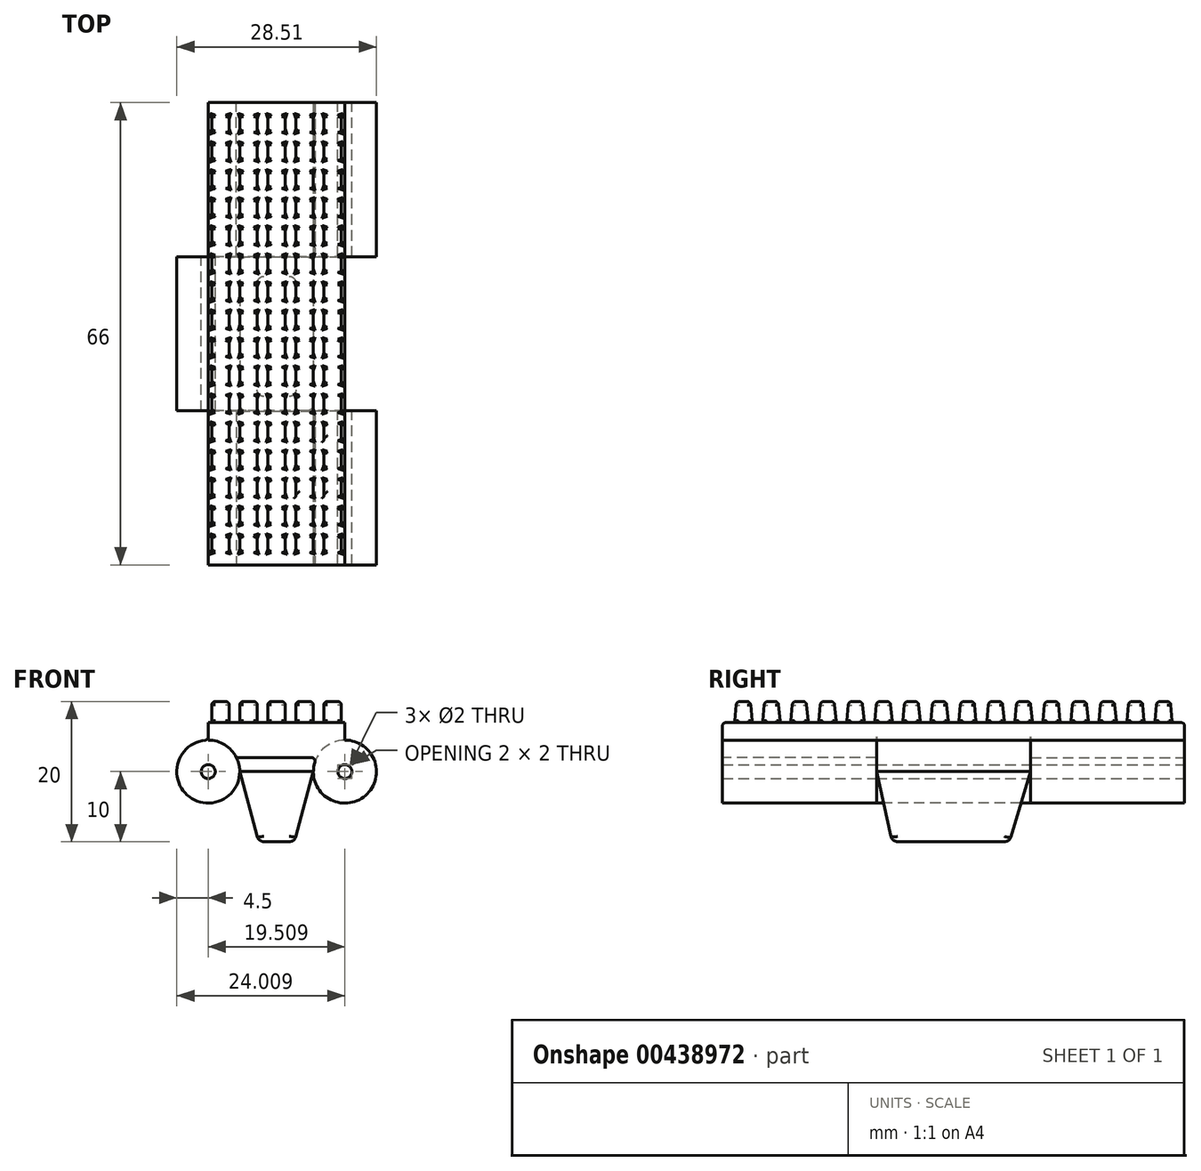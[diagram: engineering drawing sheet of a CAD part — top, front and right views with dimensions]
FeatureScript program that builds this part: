
annotation { "Feature Type Name" : "Feature", "Feature Type Description" : "" }
export const myFeature = defineFeature(function(context is Context, id is Id, definition is map)
    precondition{}
    {
        {
            var Q0;
            Q0=qCreatedBy(makeId("Front.planeOp"),FACE);
            var sketch = newSketch(context, id + "F0", { "sketchPlane" : qUnion([Q0])});
            skCircle(sketch, "E0", {"center": v(0, 0) * mm, "radius": 4.5 * mm});
            skCircle(sketch, "E1", {"center": v(19.5, 0) * mm, "radius": 4.5 * mm});
            skLineSegment(sketch, "E2.bottom", {"start": v(0, 7) * mm, "end": v(19.5, 7) * mm});
            skLineSegment(sketch, "E2.top", {"start": v(4.5, 0) * mm, "end": v(15, 0) * mm});
            skLineSegment(sketch, "E2.left", {"start": v(0, 7) * mm, "end": v(0, 4.5) * mm});
            skLineSegment(sketch, "E2.right", {"start": v(19.5, 7) * mm, "end": v(19.5, 4.5) * mm});
            skSolve(sketch);
        }
        {
            var Q0;
            {var subQ0=sQuery(id+"F0.wireOp",EDGE,"XSPy7m2Q-8Ky5-cPMg-ZX5T-lWh7BPJmsSK1");Q0=makeQuery(id+"F0.imprint","IMPRINT",FACE,{"disambiguationData":[TD([[makeQuery(id+"F0.imprint","IMPRINT",EDGE,{"derivedFrom":subQ0}),-1.0]])]});}
            var Q1;
            {var subQ3=sQuery(id+"F0.wireOp",EDGE,"E2.top");Q1=makeQuery(id+"F0.imprint","IMPRINT",FACE,{"disambiguationData":[TD([[makeQuery(id+"F0.imprint","IMPRINT",EDGE,{"derivedFrom":subQ3}),1.0]])]});}
            var Q2;
            {var subQ0=sQuery(id+"F0.wireOp",EDGE,"E1");var subQ1=makeQuery(id+"F0.imprint","INTERSECT",VERTEX,{"derivedFrom":[subQ0,sQuery(id+"F0.wireOp",EDGE,"E2.top")]});Q2=makeQuery(id+"F0.imprint","IMPRINT",FACE,{"disambiguationData":[TD([[makeQuery(id+"F0.imprint","IMPRINT",EDGE,{"disambiguationData":[TD([[subQ1,1.0]])],"derivedFrom":subQ0}),1.0]])]});}
            var Q3;
            {var subQ0=sQuery(id+"F0.wireOp",EDGE,"E0");var subQ1=makeQuery(id+"F0.imprint","INTERSECT",VERTEX,{"derivedFrom":[subQ0,sQuery(id+"F0.wireOp",EDGE,"E2.top")]});Q3=makeQuery(id+"F0.imprint","IMPRINT",FACE,{"disambiguationData":[TD([[makeQuery(id+"F0.imprint","IMPRINT",EDGE,{"disambiguationData":[TD([[subQ1,-1.0]])],"derivedFrom":subQ0}),1.0]])]});}
            extrude(context, id + "F1", {"entities" : qUnion([Q0, Q1, Q2, Q3]), "oppositeDirection" : true, "depth" : 66 * mm});
        }
        {
            var Q0;
            Q0=makeQuery(id+"F1.opExtrude","SWEPT_FACE",FACE,{"disambiguationData":[OSD([sQuery(id+"F0.wireOp",EDGE,"E2.left")])]});
            var sketch = newSketch(context, id + "F2", { "sketchPlane" : qUnion([Q0])});
            skLineSegment(sketch, "E3", {"start": v(-66, 4.5) * mm, "end": v(-44, 4.5) * mm, "construction": true});
            skLineSegment(sketch, "E4", {"start": v(-22, 4.5) * mm, "end": v(0, 4.5) * mm, "construction": true});
            skSolve(sketch);
        }
        {
            var Q0;
            Q0=makeQuery(id+"F1.opExtrude","CAP_FACE",FACE,{"disambiguationData":[OSD([sQuery(id+"F0.wireOp",EDGE,"E0"),sQuery(id+"F0.wireOp",EDGE,"E1"),sQuery(id+"F0.wireOp",EDGE,"E2.bottom"),sQuery(id+"F0.wireOp",EDGE,"E2.top"),sQuery(id+"F0.wireOp",EDGE,"E2.left"),sQuery(id+"F0.wireOp",EDGE,"E2.right"),sQuery(id+"F0.wireOp",EDGE,"XSPy7m2Q-8Ky5-cPMg-ZX5T-lWh7BPJmsSK1"),sQuery(id+"F0.wireOp",EDGE,"Qv9CYEcz-sdLX-BD8G-fHiO-GuzPuwCw1iiq"),sQuery(id+"F0.wireOp",EDGE,"SLchUEqs-7Prb-pNJw-PFLy-duSCSpJHXW3P")])],"isStart":true});
            var sketch = newSketch(context, id + "F3", { "sketchPlane" : qUnion([Q0])});
            skCircle(sketch, "E5", {"center": v(0, 0) * mm, "radius": 4.5 * mm});
            skSolve(sketch);
        }
        {
            var Q0;
            Q0=makeQuery(id+"F1.opExtrude","CAP_FACE",FACE,{"disambiguationData":[OSD([sQuery(id+"F0.wireOp",EDGE,"E0"),sQuery(id+"F0.wireOp",EDGE,"E1"),sQuery(id+"F0.wireOp",EDGE,"E2.bottom"),sQuery(id+"F0.wireOp",EDGE,"E2.top"),sQuery(id+"F0.wireOp",EDGE,"E2.left"),sQuery(id+"F0.wireOp",EDGE,"E2.right"),sQuery(id+"F0.wireOp",EDGE,"XSPy7m2Q-8Ky5-cPMg-ZX5T-lWh7BPJmsSK1"),sQuery(id+"F0.wireOp",EDGE,"Qv9CYEcz-sdLX-BD8G-fHiO-GuzPuwCw1iiq"),sQuery(id+"F0.wireOp",EDGE,"SLchUEqs-7Prb-pNJw-PFLy-duSCSpJHXW3P")])],"isStart":false});
            var sketch = newSketch(context, id + "F4", { "sketchPlane" : qUnion([Q0])});
            skCircle(sketch, "E6", {"center": v(0, 0) * mm, "radius": 4.5 * mm});
            skSolve(sketch);
        }
        {
            var Q0;
            {var subQ0=sQuery(id+"F4.wireOp",EDGE,"E6");Q0=makeQuery(id+"F4.imprint","IMPRINT",FACE,{"disambiguationData":[TD([[makeQuery(id+"F4.imprint","IMPRINT",EDGE,{"disambiguationData":[OD(0.0)],"derivedFrom":subQ0}),1.0]])]});}
            extrude(context, id + "F5", {"entities" : qUnion([Q0]), "operationType" : NewBodyOperationType.REMOVE, "oppositeDirection" : true, "depth" : 22 * mm});
        }
        {
            var Q0;
            {var subQ0=sQuery(id+"F3.wireOp",EDGE,"E5");var subQ1=makeQuery(id+"F3.imprint","INTERSECT",VERTEX,{"derivedFrom":[makeQuery(id+"F1.opExtrude","CAP_EDGE",EDGE,{"disambiguationData":[OSD([sQuery(id+"F0.wireOp",EDGE,"E2.top")])],"isStart":true}),subQ0]});Q0=makeQuery(id+"F3.imprint","IMPRINT",FACE,{"disambiguationData":[TD([[makeQuery(id+"F3.imprint","IMPRINT",EDGE,{"disambiguationData":[TD([[subQ1,-1.0]])],"derivedFrom":subQ0}),1.0]])]});}
            var Q1;
            Q1=sQuery(id+"F3.wireOp",EDGE,"E5");
            extrude(context, id + "F6", {"entities" : qUnion([Q0]), "operationType" : NewBodyOperationType.REMOVE, "surfaceEntities" : qUnion([Q1]), "oppositeDirection" : true, "depth" : 22 * mm});
        }
        {
            var Q0;
            Q0=makeQuery(id+"F6.boolean.opBoolean","COPY",FACE,{"derivedFrom":makeQuery(id+"F6.opExtrude","CAP_FACE",FACE,{"disambiguationData":[OSD([sQuery(id+"F3.wireOp",EDGE,"E5")])],"isStart":false})});
            var sketch = newSketch(context, id + "F7", { "sketchPlane" : qUnion([Q0])});
            skLineSegment(sketch, "E7", {"start": v(0, 0) * mm, "end": v(26.98, 0) * mm, "construction": true});
            skLineSegment(sketch, "E8", {"start": v(19.5, 7) * mm, "end": v(19.5, -6.27) * mm, "construction": true});
            skPoint(sketch, "E9", {"position": v(19.5, 0) * mm});
            skCircle(sketch, "E10", {"center": v(19.5, 0) * mm, "radius": 4.5 * mm});
            skSolve(sketch);
        }
        {
            var Q0;
            Q0=makeQuery(id+"F7.imprint","IMPRINT",FACE,{"disambiguationData":[TD([[makeQuery(id+"F7.imprint","IMPRINT",EDGE,{"derivedFrom":sQuery(id+"F7.wireOp",EDGE,"E10")}),1.0]])]});
            extrude(context, id + "F8", {"entities" : qUnion([Q0]), "operationType" : NewBodyOperationType.REMOVE, "oppositeDirection" : true, "depth" : 22 * mm});
        }
        {
            var Q0;
            Q0=makeQuery(id+"F1.opExtrude","CAP_FACE",FACE,{"disambiguationData":[OSD([sQuery(id+"F0.wireOp",EDGE,"E0"),sQuery(id+"F0.wireOp",EDGE,"E1"),sQuery(id+"F0.wireOp",EDGE,"E2.bottom"),sQuery(id+"F0.wireOp",EDGE,"E2.top"),sQuery(id+"F0.wireOp",EDGE,"E2.left"),sQuery(id+"F0.wireOp",EDGE,"E2.right"),sQuery(id+"F0.wireOp",EDGE,"XSPy7m2Q-8Ky5-cPMg-ZX5T-lWh7BPJmsSK1"),sQuery(id+"F0.wireOp",EDGE,"Qv9CYEcz-sdLX-BD8G-fHiO-GuzPuwCw1iiq"),sQuery(id+"F0.wireOp",EDGE,"SLchUEqs-7Prb-pNJw-PFLy-duSCSpJHXW3P")])],"isStart":false});
            var sketch = newSketch(context, id + "F9", { "sketchPlane" : qUnion([Q0])});
            skCircle(sketch, "E11", {"center": v(0, 0) * mm, "radius": 1 * mm});
            skLineSegment(sketch, "E12", {"start": v(0, 0) * mm, "end": v(-27.37, 0) * mm, "construction": true});
            skLineSegment(sketch, "E13", {"start": v(-19.5, 7) * mm, "end": v(-19.5, -5.38) * mm, "construction": true});
            skCircle(sketch, "E14", {"center": v(-19.5, 0) * mm, "radius": 1 * mm});
            skSolve(sketch);
        }
        {
            var Q0;
            Q0=makeQuery(id+"F9.imprint","IMPRINT",FACE,{"disambiguationData":[TD([[makeQuery(id+"F9.imprint","IMPRINT",EDGE,{"derivedFrom":sQuery(id+"F9.wireOp",EDGE,"E14")}),1.0]])]});
            var Q1;
            Q1=makeQuery(id+"F9.imprint","IMPRINT",FACE,{"disambiguationData":[TD([[makeQuery(id+"F9.imprint","IMPRINT",EDGE,{"derivedFrom":sQuery(id+"F9.wireOp",EDGE,"E11")}),1.0]])]});
            extrude(context, id + "F10", {"entities" : qUnion([Q0, Q1]), "operationType" : NewBodyOperationType.REMOVE, "oppositeDirection" : true, "depth" : 66 * mm});
        }
        {
            var Q0;
            Q0=makeQuery(id+"F6.boolean.opBoolean","COPY",FACE,{"derivedFrom":makeQuery(id+"F6.opExtrude","CAP_FACE",FACE,{"disambiguationData":[OSD([sQuery(id+"F3.wireOp",EDGE,"E5")])],"isStart":false})});
            var sketch = newSketch(context, id + "F11", { "sketchPlane" : qUnion([Q0])});
            skLineSegment(sketch, "E15", {"start": v(15, 0) * mm, "end": v(30.59, 0) * mm, "construction": true});
            skLineSegment(sketch, "E16", {"start": v(19.5, 6.02) * mm, "end": v(19.5, -8.46) * mm, "construction": true});
            skLineSegment(sketch, "E17", {"start": v(0, 6.05) * mm, "end": v(0, -6.6) * mm, "construction": true});
            skLineSegment(sketch, "E18", {"start": v(15, 0) * mm, "end": v(12.33, -10) * mm});
            skLineSegment(sketch, "E19", {"start": v(15, 0) * mm, "end": v(0, 0) * mm});
            skPoint(sketch, "E20", {"position": v(4.5, 0) * mm});
            skPoint(sketch, "E21", {"position": v(15, 0) * mm});
            skLineSegment(sketch, "E22", {"start": v(4.5, 0) * mm, "end": v(7.18, -10) * mm});
            skLineSegment(sketch, "E23", {"start": v(7.18, -10) * mm, "end": v(12.33, -10) * mm});
            skSolve(sketch);
        }
        {
            var Q0;
            {var subQ0=sQuery(id+"F11.wireOp",EDGE,"E18");Q0=makeQuery(id+"F11.imprint","IMPRINT",FACE,{"disambiguationData":[TD([[makeQuery(id+"F11.imprint","IMPRINT",EDGE,{"derivedFrom":subQ0}),-1.0]])]});}
            extrude(context, id + "F12", {"entities" : qUnion([Q0]), "operationType" : NewBodyOperationType.ADD, "oppositeDirection" : true, "depth" : 22 * mm});
        }
        {
            var Q0;
            {var subQ0=sQuery(id+"F0.wireOp",EDGE,"E2.left");Q0=makeQuery(id+"F2.imprint","IMPRINT",FACE,{"disambiguationData":[TD([[makeQuery(id+"F2.imprint","IMPRINT",EDGE,{"derivedFrom":makeQuery(id+"F1.opExtrude","CAP_EDGE",EDGE,{"disambiguationData":[OSD([subQ0])],"isStart":true})}),-1.0]])]});}
            cPlane(context, id + "F13", {"entities" : qUnion([Q0]), "cplaneType" : CPlaneType.OFFSET, "offset" : 4.5 * mm, "oppositeDirection" : true, "width" : 150 * mm, "height" : 150 * mm});
        }
        {
            var Q0;
            Q0=qCreatedBy(id+"F13.planeOp",FACE);
            var sketch = newSketch(context, id + "F14", { "sketchPlane" : qUnion([Q0])});
            skLineSegment(sketch, "E24", {"start": v(-44, 0) * mm, "end": v(-40.94, -10.27) * mm});
            skLineSegment(sketch, "E25", {"start": v(-22, 0) * mm, "end": v(-24.29, -10.27) * mm});
            skLineSegment(sketch, "E26", {"start": v(-44, 0) * mm, "end": v(-44, -10.27) * mm});
            skLineSegment(sketch, "E27", {"start": v(-22, 0) * mm, "end": v(-22, -10.27) * mm});
            skLineSegment(sketch, "E28", {"start": v(-44, -10.27) * mm, "end": v(-40.94, -10.27) * mm});
            skLineSegment(sketch, "E29.trimOffspring", {"start": v(-24.29, -10.27) * mm, "end": v(-22, -10.27) * mm});
            skSolve(sketch);
        }
        {
            var Q0;
            Q0=makeQuery(id+"F14.imprint","IMPRINT",FACE,{"disambiguationData":[TD([[makeQuery(id+"F14.imprint","IMPRINT",EDGE,{"derivedFrom":sQuery(id+"F14.wireOp",EDGE,"E24")}),-1.0]])]});
            var Q1;
            Q1=makeQuery(id+"F14.imprint","IMPRINT",FACE,{"disambiguationData":[TD([[makeQuery(id+"F14.imprint","IMPRINT",EDGE,{"derivedFrom":sQuery(id+"F14.wireOp",EDGE,"E25")}),1.0]])]});
            extrude(context, id + "F15", {"entities" : qUnion([Q0, Q1]), "operationType" : NewBodyOperationType.REMOVE, "oppositeDirection" : true, "depth" : 13 * mm});
        }
        {
            var Q0;
            Q0=makeQuery(id+"F1.opExtrude","CAP_FACE",FACE,{"disambiguationData":[OSD([sQuery(id+"F0.wireOp",EDGE,"E0"),sQuery(id+"F0.wireOp",EDGE,"E1"),sQuery(id+"F0.wireOp",EDGE,"E2.bottom"),sQuery(id+"F0.wireOp",EDGE,"E2.top"),sQuery(id+"F0.wireOp",EDGE,"E2.left"),sQuery(id+"F0.wireOp",EDGE,"E2.right"),sQuery(id+"F0.wireOp",EDGE,"XSPy7m2Q-8Ky5-cPMg-ZX5T-lWh7BPJmsSK1"),sQuery(id+"F0.wireOp",EDGE,"Qv9CYEcz-sdLX-BD8G-fHiO-GuzPuwCw1iiq"),sQuery(id+"F0.wireOp",EDGE,"SLchUEqs-7Prb-pNJw-PFLy-duSCSpJHXW3P")])],"isStart":false});
            var sketch = newSketch(context, id + "F16", { "sketchPlane" : qUnion([Q0])});
            skArc(sketch, "E30", {"start": v(-15, 0) * mm, "mid": v(-15.13, 1.03) * mm, "end": v(-15.48, 2) * mm});
            skLineSegment(sketch, "E31", {"start": v(-15, 0) * mm, "end": v(-4.5, 0) * mm});
            skLineSegment(sketch, "E32", {"start": v(-4.03, 2) * mm, "end": v(-15.48, 2) * mm});
            skArc(sketch, "E33", {"start": v(-4.03, 2) * mm, "mid": v(-4.38, 1.03) * mm, "end": v(-4.5, 0) * mm});
            skSolve(sketch);
        }
        {
            var Q0;
            Q0=makeQuery(id+"F16.imprint","IMPRINT",FACE,{"disambiguationData":[TD([[makeQuery(id+"F16.imprint","IMPRINT",EDGE,{"derivedFrom":sQuery(id+"F16.wireOp",EDGE,"E30")}),-1.0]])]});
            extrude(context, id + "F17", {"entities" : qUnion([Q0]), "operationType" : NewBodyOperationType.REMOVE, "oppositeDirection" : true, "depth" : 21.99 * mm});
        }
        {
            var Q0;
            Q0=makeQuery(id+"F1.opExtrude","CAP_FACE",FACE,{"disambiguationData":[OSD([sQuery(id+"F0.wireOp",EDGE,"E0"),sQuery(id+"F0.wireOp",EDGE,"E1"),sQuery(id+"F0.wireOp",EDGE,"E2.bottom"),sQuery(id+"F0.wireOp",EDGE,"E2.top"),sQuery(id+"F0.wireOp",EDGE,"E2.left"),sQuery(id+"F0.wireOp",EDGE,"E2.right"),sQuery(id+"F0.wireOp",EDGE,"XSPy7m2Q-8Ky5-cPMg-ZX5T-lWh7BPJmsSK1"),sQuery(id+"F0.wireOp",EDGE,"Qv9CYEcz-sdLX-BD8G-fHiO-GuzPuwCw1iiq"),sQuery(id+"F0.wireOp",EDGE,"SLchUEqs-7Prb-pNJw-PFLy-duSCSpJHXW3P")])],"isStart":true});
            var sketch = newSketch(context, id + "F18", { "sketchPlane" : qUnion([Q0])});
            skArc(sketch, "E34", {"start": v(4.5, 0) * mm, "mid": v(4.38, 1.03) * mm, "end": v(4.03, 2) * mm});
            skArc(sketch, "E35", {"start": v(15.48, 2) * mm, "mid": v(15.13, 1.03) * mm, "end": v(15, 0) * mm});
            skLineSegment(sketch, "E36", {"start": v(4.03, 2) * mm, "end": v(15.48, 2) * mm});
            skLineSegment(sketch, "E37", {"start": v(15, 0) * mm, "end": v(4.5, 0) * mm});
            skSolve(sketch);
        }
        {
            var Q0;
            Q0=makeQuery(id+"F18.imprint","IMPRINT",FACE,{"disambiguationData":[TD([[makeQuery(id+"F18.imprint","IMPRINT",EDGE,{"derivedFrom":sQuery(id+"F18.wireOp",EDGE,"E34")}),-1.0]])]});
            extrude(context, id + "F19", {"entities" : qUnion([Q0]), "operationType" : NewBodyOperationType.REMOVE, "oppositeDirection" : true, "depth" : 21.98 * mm});
        }
        {
            var Q0;
            Q0=makeQuery(id+"FJAbp6d8c6zq0qW_1.boolean.opBoolean","MERGE",FACE,{"derivedFrom":[makeQuery(id+"F1.opExtrude","SWEPT_FACE",FACE,{"disambiguationData":[OSD([sQuery(id+"F0.wireOp",EDGE,"E2.left")])]}),makeQuery(id+"FJAbp6d8c6zq0qW_1.opExtrude","SWEPT_FACE",FACE,{"disambiguationData":[OSD([sQuery(id+"FjXNzUCDF6skfny_1.wireOp",EDGE,"ZpUVPl6h-XxjU-j18W-hNYx-q3vLESmVbvHY")])]})]});
            var sketch = newSketch(context, id + "F20", { "sketchPlane" : qUnion([Q0])});
            skLineSegment(sketch, "E38", {"start": v(-64.23, 7.23) * mm, "end": v(-64.03, 9.54) * mm});
            skLineSegment(sketch, "E39", {"start": v(-61.77, 7.23) * mm, "end": v(-61.97, 9.54) * mm});
            skLineSegment(sketch, "E40", {"start": v(-63.53, 10) * mm, "end": v(-62.47, 10) * mm});
            skPoint(sketch, "E41.visualSharp", {"position": v(-63.99, 10) * mm});
            skArc(sketch, "E41.filletArc", {"start": v(-63.53, 10) * mm, "mid": v(-63.87, 9.87) * mm, "end": v(-64.03, 9.54) * mm});
            skPoint(sketch, "E42.visualSharp", {"position": v(-62.01, 10) * mm});
            skArc(sketch, "E42.filletArc", {"start": v(-61.97, 9.54) * mm, "mid": v(-62.13, 9.87) * mm, "end": v(-62.47, 10) * mm});
            skLineSegment(sketch, "E43", {"start": v(-66, 7) * mm, "end": v(-64.48, 7) * mm});
            skLineSegment(sketch, "E44", {"start": v(-61.52, 7) * mm, "end": v(-60.25, 7) * mm});
            skPoint(sketch, "E45.visualSharp", {"position": v(-64.25, 7) * mm});
            skArc(sketch, "E45.filletArc", {"start": v(-64.48, 7) * mm, "mid": v(-64.31, 7.07) * mm, "end": v(-64.23, 7.23) * mm});
            skPoint(sketch, "E46.visualSharp", {"position": v(-61.75, 7) * mm});
            skArc(sketch, "E46.filletArc", {"start": v(-61.77, 7.23) * mm, "mid": v(-61.69, 7.07) * mm, "end": v(-61.52, 7) * mm});
            skPoint(sketch, "E47.1.0.0", {"position": v(-59.99, 10) * mm});
            skLineSegment(sketch, "E47.1.0.1", {"start": v(-57.52, 7) * mm, "end": v(-56.25, 7) * mm});
            skLineSegment(sketch, "E47.1.0.2", {"start": v(-60.23, 7.23) * mm, "end": v(-60.03, 9.54) * mm});
            skPoint(sketch, "E47.1.0.3", {"position": v(-57.75, 7) * mm});
            skPoint(sketch, "E47.1.0.4", {"position": v(-60.25, 7) * mm});
            skLineSegment(sketch, "E47.1.0.5", {"start": v(-59.53, 10) * mm, "end": v(-58.47, 10) * mm});
            skPoint(sketch, "E47.1.0.6", {"position": v(-58.01, 10) * mm});
            skLineSegment(sketch, "E47.1.0.7", {"start": v(-57.77, 7.23) * mm, "end": v(-57.97, 9.54) * mm});
            skArc(sketch, "E47.1.0.8", {"start": v(-59.53, 10) * mm, "mid": v(-59.87, 9.87) * mm, "end": v(-60.03, 9.54) * mm});
            skArc(sketch, "E47.1.0.9", {"start": v(-57.97, 9.54) * mm, "mid": v(-58.13, 9.87) * mm, "end": v(-58.47, 10) * mm});
            skArc(sketch, "E47.1.0.10", {"start": v(-57.77, 7.23) * mm, "mid": v(-57.69, 7.07) * mm, "end": v(-57.52, 7) * mm});
            skArc(sketch, "E47.1.0.11", {"start": v(-60.48, 7) * mm, "mid": v(-60.31, 7.07) * mm, "end": v(-60.23, 7.23) * mm});
            skPoint(sketch, "E47.2.0.0", {"position": v(-55.99, 10) * mm});
            skLineSegment(sketch, "E47.2.0.1", {"start": v(-53.52, 7) * mm, "end": v(-52.25, 7) * mm});
            skLineSegment(sketch, "E47.2.0.2", {"start": v(-56.23, 7.23) * mm, "end": v(-56.03, 9.54) * mm});
            skPoint(sketch, "E47.2.0.3", {"position": v(-53.75, 7) * mm});
            skPoint(sketch, "E47.2.0.4", {"position": v(-56.25, 7) * mm});
            skLineSegment(sketch, "E47.2.0.5", {"start": v(-55.53, 10) * mm, "end": v(-54.47, 10) * mm});
            skPoint(sketch, "E47.2.0.6", {"position": v(-54.01, 10) * mm});
            skLineSegment(sketch, "E47.2.0.7", {"start": v(-53.77, 7.23) * mm, "end": v(-53.97, 9.54) * mm});
            skArc(sketch, "E47.2.0.8", {"start": v(-55.53, 10) * mm, "mid": v(-55.87, 9.87) * mm, "end": v(-56.03, 9.54) * mm});
            skArc(sketch, "E47.2.0.9", {"start": v(-53.97, 9.54) * mm, "mid": v(-54.13, 9.87) * mm, "end": v(-54.47, 10) * mm});
            skArc(sketch, "E47.2.0.10", {"start": v(-53.77, 7.23) * mm, "mid": v(-53.69, 7.07) * mm, "end": v(-53.52, 7) * mm});
            skArc(sketch, "E47.2.0.11", {"start": v(-56.48, 7) * mm, "mid": v(-56.31, 7.07) * mm, "end": v(-56.23, 7.23) * mm});
            skPoint(sketch, "E47.3.0.0", {"position": v(-51.99, 10) * mm});
            skLineSegment(sketch, "E47.3.0.1", {"start": v(-49.52, 7) * mm, "end": v(-48.25, 7) * mm});
            skLineSegment(sketch, "E47.3.0.2", {"start": v(-52.23, 7.23) * mm, "end": v(-52.03, 9.54) * mm});
            skPoint(sketch, "E47.3.0.3", {"position": v(-49.75, 7) * mm});
            skPoint(sketch, "E47.3.0.4", {"position": v(-52.25, 7) * mm});
            skLineSegment(sketch, "E47.3.0.5", {"start": v(-51.53, 10) * mm, "end": v(-50.47, 10) * mm});
            skPoint(sketch, "E47.3.0.6", {"position": v(-50.01, 10) * mm});
            skLineSegment(sketch, "E47.3.0.7", {"start": v(-49.77, 7.23) * mm, "end": v(-49.97, 9.54) * mm});
            skArc(sketch, "E47.3.0.8", {"start": v(-51.53, 10) * mm, "mid": v(-51.87, 9.87) * mm, "end": v(-52.03, 9.54) * mm});
            skArc(sketch, "E47.3.0.9", {"start": v(-49.97, 9.54) * mm, "mid": v(-50.13, 9.87) * mm, "end": v(-50.47, 10) * mm});
            skArc(sketch, "E47.3.0.10", {"start": v(-49.77, 7.23) * mm, "mid": v(-49.69, 7.07) * mm, "end": v(-49.52, 7) * mm});
            skArc(sketch, "E47.3.0.11", {"start": v(-52.48, 7) * mm, "mid": v(-52.31, 7.07) * mm, "end": v(-52.23, 7.23) * mm});
            skPoint(sketch, "E47.4.0.0", {"position": v(-47.99, 10) * mm});
            skLineSegment(sketch, "E47.4.0.1", {"start": v(-45.52, 7) * mm, "end": v(-44.25, 7) * mm});
            skLineSegment(sketch, "E47.4.0.2", {"start": v(-48.23, 7.23) * mm, "end": v(-48.03, 9.54) * mm});
            skPoint(sketch, "E47.4.0.3", {"position": v(-45.75, 7) * mm});
            skPoint(sketch, "E47.4.0.4", {"position": v(-48.25, 7) * mm});
            skLineSegment(sketch, "E47.4.0.5", {"start": v(-47.53, 10) * mm, "end": v(-46.47, 10) * mm});
            skPoint(sketch, "E47.4.0.6", {"position": v(-46.01, 10) * mm});
            skLineSegment(sketch, "E47.4.0.7", {"start": v(-45.77, 7.23) * mm, "end": v(-45.97, 9.54) * mm});
            skArc(sketch, "E47.4.0.8", {"start": v(-47.53, 10) * mm, "mid": v(-47.87, 9.87) * mm, "end": v(-48.03, 9.54) * mm});
            skArc(sketch, "E47.4.0.9", {"start": v(-45.97, 9.54) * mm, "mid": v(-46.13, 9.87) * mm, "end": v(-46.47, 10) * mm});
            skArc(sketch, "E47.4.0.10", {"start": v(-45.77, 7.23) * mm, "mid": v(-45.69, 7.07) * mm, "end": v(-45.52, 7) * mm});
            skArc(sketch, "E47.4.0.11", {"start": v(-48.48, 7) * mm, "mid": v(-48.31, 7.07) * mm, "end": v(-48.23, 7.23) * mm});
            skPoint(sketch, "E47.5.0.0", {"position": v(-43.99, 10) * mm});
            skLineSegment(sketch, "E47.5.0.1", {"start": v(-41.52, 7) * mm, "end": v(-40.25, 7) * mm});
            skLineSegment(sketch, "E47.5.0.2", {"start": v(-44.23, 7.23) * mm, "end": v(-44.03, 9.54) * mm});
            skPoint(sketch, "E47.5.0.3", {"position": v(-41.75, 7) * mm});
            skPoint(sketch, "E47.5.0.4", {"position": v(-44.25, 7) * mm});
            skLineSegment(sketch, "E47.5.0.5", {"start": v(-43.53, 10) * mm, "end": v(-42.47, 10) * mm});
            skPoint(sketch, "E47.5.0.6", {"position": v(-42.01, 10) * mm});
            skLineSegment(sketch, "E47.5.0.7", {"start": v(-41.77, 7.23) * mm, "end": v(-41.97, 9.54) * mm});
            skArc(sketch, "E47.5.0.8", {"start": v(-43.53, 10) * mm, "mid": v(-43.87, 9.87) * mm, "end": v(-44.03, 9.54) * mm});
            skArc(sketch, "E47.5.0.9", {"start": v(-41.97, 9.54) * mm, "mid": v(-42.13, 9.87) * mm, "end": v(-42.47, 10) * mm});
            skArc(sketch, "E47.5.0.10", {"start": v(-41.77, 7.23) * mm, "mid": v(-41.69, 7.07) * mm, "end": v(-41.52, 7) * mm});
            skArc(sketch, "E47.5.0.11", {"start": v(-44.48, 7) * mm, "mid": v(-44.31, 7.07) * mm, "end": v(-44.23, 7.23) * mm});
            skPoint(sketch, "E47.6.0.0", {"position": v(-39.99, 10) * mm});
            skLineSegment(sketch, "E47.6.0.1", {"start": v(-37.52, 7) * mm, "end": v(-36.25, 7) * mm});
            skLineSegment(sketch, "E47.6.0.2", {"start": v(-40.23, 7.23) * mm, "end": v(-40.03, 9.54) * mm});
            skPoint(sketch, "E47.6.0.3", {"position": v(-37.75, 7) * mm});
            skPoint(sketch, "E47.6.0.4", {"position": v(-40.25, 7) * mm});
            skLineSegment(sketch, "E47.6.0.5", {"start": v(-39.53, 10) * mm, "end": v(-38.47, 10) * mm});
            skPoint(sketch, "E47.6.0.6", {"position": v(-38.01, 10) * mm});
            skLineSegment(sketch, "E47.6.0.7", {"start": v(-37.77, 7.23) * mm, "end": v(-37.97, 9.54) * mm});
            skArc(sketch, "E47.6.0.8", {"start": v(-39.53, 10) * mm, "mid": v(-39.87, 9.87) * mm, "end": v(-40.03, 9.54) * mm});
            skArc(sketch, "E47.6.0.9", {"start": v(-37.97, 9.54) * mm, "mid": v(-38.13, 9.87) * mm, "end": v(-38.47, 10) * mm});
            skArc(sketch, "E47.6.0.10", {"start": v(-37.77, 7.23) * mm, "mid": v(-37.69, 7.07) * mm, "end": v(-37.52, 7) * mm});
            skArc(sketch, "E47.6.0.11", {"start": v(-40.48, 7) * mm, "mid": v(-40.31, 7.07) * mm, "end": v(-40.23, 7.23) * mm});
            skPoint(sketch, "E47.7.0.0", {"position": v(-35.99, 10) * mm});
            skLineSegment(sketch, "E47.7.0.1", {"start": v(-33.52, 7) * mm, "end": v(-32.25, 7) * mm});
            skLineSegment(sketch, "E47.7.0.2", {"start": v(-36.23, 7.23) * mm, "end": v(-36.03, 9.54) * mm});
            skPoint(sketch, "E47.7.0.3", {"position": v(-33.75, 7) * mm});
            skPoint(sketch, "E47.7.0.4", {"position": v(-36.25, 7) * mm});
            skLineSegment(sketch, "E47.7.0.5", {"start": v(-35.53, 10) * mm, "end": v(-34.47, 10) * mm});
            skPoint(sketch, "E47.7.0.6", {"position": v(-34.01, 10) * mm});
            skLineSegment(sketch, "E47.7.0.7", {"start": v(-33.77, 7.23) * mm, "end": v(-33.97, 9.54) * mm});
            skArc(sketch, "E47.7.0.8", {"start": v(-35.53, 10) * mm, "mid": v(-35.87, 9.87) * mm, "end": v(-36.03, 9.54) * mm});
            skArc(sketch, "E47.7.0.9", {"start": v(-33.97, 9.54) * mm, "mid": v(-34.13, 9.87) * mm, "end": v(-34.47, 10) * mm});
            skArc(sketch, "E47.7.0.10", {"start": v(-33.77, 7.23) * mm, "mid": v(-33.69, 7.07) * mm, "end": v(-33.52, 7) * mm});
            skArc(sketch, "E47.7.0.11", {"start": v(-36.48, 7) * mm, "mid": v(-36.31, 7.07) * mm, "end": v(-36.23, 7.23) * mm});
            skPoint(sketch, "E47.8.0.0", {"position": v(-31.99, 10) * mm});
            skLineSegment(sketch, "E47.8.0.1", {"start": v(-29.52, 7) * mm, "end": v(-28.25, 7) * mm});
            skLineSegment(sketch, "E47.8.0.2", {"start": v(-32.23, 7.23) * mm, "end": v(-32.03, 9.54) * mm});
            skPoint(sketch, "E47.8.0.3", {"position": v(-29.75, 7) * mm});
            skPoint(sketch, "E47.8.0.4", {"position": v(-32.25, 7) * mm});
            skLineSegment(sketch, "E47.8.0.5", {"start": v(-31.53, 10) * mm, "end": v(-30.47, 10) * mm});
            skPoint(sketch, "E47.8.0.6", {"position": v(-30.01, 10) * mm});
            skLineSegment(sketch, "E47.8.0.7", {"start": v(-29.77, 7.23) * mm, "end": v(-29.97, 9.54) * mm});
            skArc(sketch, "E47.8.0.8", {"start": v(-31.53, 10) * mm, "mid": v(-31.87, 9.87) * mm, "end": v(-32.03, 9.54) * mm});
            skArc(sketch, "E47.8.0.9", {"start": v(-29.97, 9.54) * mm, "mid": v(-30.13, 9.87) * mm, "end": v(-30.47, 10) * mm});
            skArc(sketch, "E47.8.0.10", {"start": v(-29.77, 7.23) * mm, "mid": v(-29.69, 7.07) * mm, "end": v(-29.52, 7) * mm});
            skArc(sketch, "E47.8.0.11", {"start": v(-32.48, 7) * mm, "mid": v(-32.31, 7.07) * mm, "end": v(-32.23, 7.23) * mm});
            skPoint(sketch, "E47.9.0.0", {"position": v(-27.99, 10) * mm});
            skLineSegment(sketch, "E47.9.0.1", {"start": v(-25.52, 7) * mm, "end": v(-24.25, 7) * mm});
            skLineSegment(sketch, "E47.9.0.2", {"start": v(-28.23, 7.23) * mm, "end": v(-28.03, 9.54) * mm});
            skPoint(sketch, "E47.9.0.3", {"position": v(-25.75, 7) * mm});
            skPoint(sketch, "E47.9.0.4", {"position": v(-28.25, 7) * mm});
            skLineSegment(sketch, "E47.9.0.5", {"start": v(-27.53, 10) * mm, "end": v(-26.47, 10) * mm});
            skPoint(sketch, "E47.9.0.6", {"position": v(-26.01, 10) * mm});
            skLineSegment(sketch, "E47.9.0.7", {"start": v(-25.77, 7.23) * mm, "end": v(-25.97, 9.54) * mm});
            skArc(sketch, "E47.9.0.8", {"start": v(-27.53, 10) * mm, "mid": v(-27.87, 9.87) * mm, "end": v(-28.03, 9.54) * mm});
            skArc(sketch, "E47.9.0.9", {"start": v(-25.97, 9.54) * mm, "mid": v(-26.13, 9.87) * mm, "end": v(-26.47, 10) * mm});
            skArc(sketch, "E47.9.0.10", {"start": v(-25.77, 7.23) * mm, "mid": v(-25.69, 7.07) * mm, "end": v(-25.52, 7) * mm});
            skArc(sketch, "E47.9.0.11", {"start": v(-28.48, 7) * mm, "mid": v(-28.31, 7.07) * mm, "end": v(-28.23, 7.23) * mm});
            skPoint(sketch, "E47.10.0.0", {"position": v(-23.99, 10) * mm});
            skLineSegment(sketch, "E47.10.0.1", {"start": v(-21.52, 7) * mm, "end": v(-20.25, 7) * mm});
            skLineSegment(sketch, "E47.10.0.2", {"start": v(-24.23, 7.23) * mm, "end": v(-24.03, 9.54) * mm});
            skPoint(sketch, "E47.10.0.3", {"position": v(-21.75, 7) * mm});
            skPoint(sketch, "E47.10.0.4", {"position": v(-24.25, 7) * mm});
            skLineSegment(sketch, "E47.10.0.5", {"start": v(-23.53, 10) * mm, "end": v(-22.47, 10) * mm});
            skPoint(sketch, "E47.10.0.6", {"position": v(-22.01, 10) * mm});
            skLineSegment(sketch, "E47.10.0.7", {"start": v(-21.77, 7.23) * mm, "end": v(-21.97, 9.54) * mm});
            skArc(sketch, "E47.10.0.8", {"start": v(-23.53, 10) * mm, "mid": v(-23.87, 9.87) * mm, "end": v(-24.03, 9.54) * mm});
            skArc(sketch, "E47.10.0.9", {"start": v(-21.97, 9.54) * mm, "mid": v(-22.13, 9.87) * mm, "end": v(-22.47, 10) * mm});
            skArc(sketch, "E47.10.0.10", {"start": v(-21.77, 7.23) * mm, "mid": v(-21.69, 7.07) * mm, "end": v(-21.52, 7) * mm});
            skArc(sketch, "E47.10.0.11", {"start": v(-24.48, 7) * mm, "mid": v(-24.31, 7.07) * mm, "end": v(-24.23, 7.23) * mm});
            skPoint(sketch, "E47.11.0.0", {"position": v(-19.99, 10) * mm});
            skLineSegment(sketch, "E47.11.0.1", {"start": v(-17.52, 7) * mm, "end": v(-16.25, 7) * mm});
            skLineSegment(sketch, "E47.11.0.2", {"start": v(-20.23, 7.23) * mm, "end": v(-20.03, 9.54) * mm});
            skPoint(sketch, "E47.11.0.3", {"position": v(-17.75, 7) * mm});
            skPoint(sketch, "E47.11.0.4", {"position": v(-20.25, 7) * mm});
            skLineSegment(sketch, "E47.11.0.5", {"start": v(-19.53, 10) * mm, "end": v(-18.47, 10) * mm});
            skPoint(sketch, "E47.11.0.6", {"position": v(-18.01, 10) * mm});
            skLineSegment(sketch, "E47.11.0.7", {"start": v(-17.77, 7.23) * mm, "end": v(-17.97, 9.54) * mm});
            skArc(sketch, "E47.11.0.8", {"start": v(-19.53, 10) * mm, "mid": v(-19.87, 9.87) * mm, "end": v(-20.03, 9.54) * mm});
            skArc(sketch, "E47.11.0.9", {"start": v(-17.97, 9.54) * mm, "mid": v(-18.13, 9.87) * mm, "end": v(-18.47, 10) * mm});
            skArc(sketch, "E47.11.0.10", {"start": v(-17.77, 7.23) * mm, "mid": v(-17.69, 7.07) * mm, "end": v(-17.52, 7) * mm});
            skArc(sketch, "E47.11.0.11", {"start": v(-20.48, 7) * mm, "mid": v(-20.31, 7.07) * mm, "end": v(-20.23, 7.23) * mm});
            skPoint(sketch, "E47.12.0.0", {"position": v(-15.99, 10) * mm});
            skLineSegment(sketch, "E47.12.0.1", {"start": v(-13.52, 7) * mm, "end": v(-12.25, 7) * mm});
            skLineSegment(sketch, "E47.12.0.2", {"start": v(-16.23, 7.23) * mm, "end": v(-16.03, 9.54) * mm});
            skPoint(sketch, "E47.12.0.3", {"position": v(-13.75, 7) * mm});
            skPoint(sketch, "E47.12.0.4", {"position": v(-16.25, 7) * mm});
            skLineSegment(sketch, "E47.12.0.5", {"start": v(-15.53, 10) * mm, "end": v(-14.47, 10) * mm});
            skPoint(sketch, "E47.12.0.6", {"position": v(-14.01, 10) * mm});
            skLineSegment(sketch, "E47.12.0.7", {"start": v(-13.77, 7.23) * mm, "end": v(-13.97, 9.54) * mm});
            skArc(sketch, "E47.12.0.8", {"start": v(-15.53, 10) * mm, "mid": v(-15.87, 9.87) * mm, "end": v(-16.03, 9.54) * mm});
            skArc(sketch, "E47.12.0.9", {"start": v(-13.97, 9.54) * mm, "mid": v(-14.13, 9.87) * mm, "end": v(-14.47, 10) * mm});
            skArc(sketch, "E47.12.0.10", {"start": v(-13.77, 7.23) * mm, "mid": v(-13.69, 7.07) * mm, "end": v(-13.52, 7) * mm});
            skArc(sketch, "E47.12.0.11", {"start": v(-16.48, 7) * mm, "mid": v(-16.31, 7.07) * mm, "end": v(-16.23, 7.23) * mm});
            skPoint(sketch, "E47.13.0.0", {"position": v(-11.99, 10) * mm});
            skLineSegment(sketch, "E47.13.0.1", {"start": v(-9.52, 7) * mm, "end": v(-8.25, 7) * mm});
            skLineSegment(sketch, "E47.13.0.2", {"start": v(-12.23, 7.23) * mm, "end": v(-12.03, 9.54) * mm});
            skPoint(sketch, "E47.13.0.3", {"position": v(-9.75, 7) * mm});
            skPoint(sketch, "E47.13.0.4", {"position": v(-12.25, 7) * mm});
            skLineSegment(sketch, "E47.13.0.5", {"start": v(-11.53, 10) * mm, "end": v(-10.47, 10) * mm});
            skPoint(sketch, "E47.13.0.6", {"position": v(-10.01, 10) * mm});
            skLineSegment(sketch, "E47.13.0.7", {"start": v(-9.77, 7.23) * mm, "end": v(-9.97, 9.54) * mm});
            skArc(sketch, "E47.13.0.8", {"start": v(-11.53, 10) * mm, "mid": v(-11.87, 9.87) * mm, "end": v(-12.03, 9.54) * mm});
            skArc(sketch, "E47.13.0.9", {"start": v(-9.97, 9.54) * mm, "mid": v(-10.13, 9.87) * mm, "end": v(-10.47, 10) * mm});
            skArc(sketch, "E47.13.0.10", {"start": v(-9.77, 7.23) * mm, "mid": v(-9.69, 7.07) * mm, "end": v(-9.52, 7) * mm});
            skArc(sketch, "E47.13.0.11", {"start": v(-12.48, 7) * mm, "mid": v(-12.31, 7.07) * mm, "end": v(-12.23, 7.23) * mm});
            skPoint(sketch, "E47.14.0.0", {"position": v(-7.99, 10) * mm});
            skLineSegment(sketch, "E47.14.0.1", {"start": v(-5.52, 7) * mm, "end": v(-4.25, 7) * mm});
            skLineSegment(sketch, "E47.14.0.2", {"start": v(-8.23, 7.23) * mm, "end": v(-8.03, 9.54) * mm});
            skPoint(sketch, "E47.14.0.3", {"position": v(-5.75, 7) * mm});
            skPoint(sketch, "E47.14.0.4", {"position": v(-8.25, 7) * mm});
            skLineSegment(sketch, "E47.14.0.5", {"start": v(-7.53, 10) * mm, "end": v(-6.47, 10) * mm});
            skPoint(sketch, "E47.14.0.6", {"position": v(-6.01, 10) * mm});
            skLineSegment(sketch, "E47.14.0.7", {"start": v(-5.77, 7.23) * mm, "end": v(-5.97, 9.54) * mm});
            skArc(sketch, "E47.14.0.8", {"start": v(-7.53, 10) * mm, "mid": v(-7.87, 9.87) * mm, "end": v(-8.03, 9.54) * mm});
            skArc(sketch, "E47.14.0.9", {"start": v(-5.97, 9.54) * mm, "mid": v(-6.13, 9.87) * mm, "end": v(-6.47, 10) * mm});
            skArc(sketch, "E47.14.0.10", {"start": v(-5.77, 7.23) * mm, "mid": v(-5.69, 7.07) * mm, "end": v(-5.52, 7) * mm});
            skArc(sketch, "E47.14.0.11", {"start": v(-8.48, 7) * mm, "mid": v(-8.31, 7.07) * mm, "end": v(-8.23, 7.23) * mm});
            skPoint(sketch, "E47.15.0.0", {"position": v(-3.99, 10) * mm});
            skLineSegment(sketch, "E47.15.0.2", {"start": v(-4.23, 7.23) * mm, "end": v(-4.03, 9.54) * mm});
            skPoint(sketch, "E47.15.0.3", {"position": v(-1.75, 7) * mm});
            skPoint(sketch, "E47.15.0.4", {"position": v(-4.25, 7) * mm});
            skLineSegment(sketch, "E47.15.0.5", {"start": v(-3.53, 10) * mm, "end": v(-2.47, 10) * mm});
            skPoint(sketch, "E47.15.0.6", {"position": v(-2.01, 10) * mm});
            skLineSegment(sketch, "E47.15.0.7", {"start": v(-1.77, 7.23) * mm, "end": v(-1.97, 9.54) * mm});
            skArc(sketch, "E47.15.0.8", {"start": v(-3.53, 10) * mm, "mid": v(-3.87, 9.87) * mm, "end": v(-4.03, 9.54) * mm});
            skArc(sketch, "E47.15.0.9", {"start": v(-1.97, 9.54) * mm, "mid": v(-2.13, 9.87) * mm, "end": v(-2.47, 10) * mm});
            skArc(sketch, "E47.15.0.10", {"start": v(-1.77, 7.23) * mm, "mid": v(-1.69, 7.07) * mm, "end": v(-1.52, 7) * mm});
            skArc(sketch, "E47.15.0.11", {"start": v(-4.48, 7) * mm, "mid": v(-4.31, 7.07) * mm, "end": v(-4.23, 7.23) * mm});
            skLineSegment(sketch, "E47.direction1", {"start": v(-64.48, 7) * mm, "end": v(-60.48, 7) * mm, "construction": true});
            skSolve(sketch);
        }
        {
            var Q0;
            Q0=makeQuery(id+"F20.imprint","IMPRINT",FACE,{"disambiguationData":[TD([[makeQuery(id+"F20.imprint","IMPRINT",EDGE,{"derivedFrom":sQuery(id+"F20.wireOp",EDGE,"E38")}),-1.0]])]});
            var Q1;
            Q1=makeQuery(id+"F20.imprint","IMPRINT",FACE,{"disambiguationData":[TD([[makeQuery(id+"F20.imprint","IMPRINT",EDGE,{"derivedFrom":sQuery(id+"F20.wireOp",EDGE,"E47.1.0.2")}),-1.0]])]});
            var Q2;
            Q2=makeQuery(id+"F20.imprint","IMPRINT",FACE,{"disambiguationData":[TD([[makeQuery(id+"F20.imprint","IMPRINT",EDGE,{"derivedFrom":sQuery(id+"F20.wireOp",EDGE,"E47.2.0.2")}),-1.0]])]});
            var Q3;
            Q3=makeQuery(id+"F20.imprint","IMPRINT",FACE,{"disambiguationData":[TD([[makeQuery(id+"F20.imprint","IMPRINT",EDGE,{"derivedFrom":sQuery(id+"F20.wireOp",EDGE,"E47.3.0.2")}),-1.0]])]});
            var Q4;
            Q4=makeQuery(id+"F20.imprint","IMPRINT",FACE,{"disambiguationData":[TD([[makeQuery(id+"F20.imprint","IMPRINT",EDGE,{"derivedFrom":sQuery(id+"F20.wireOp",EDGE,"E47.4.0.2")}),-1.0]])]});
            var Q5;
            Q5=makeQuery(id+"F20.imprint","IMPRINT",FACE,{"disambiguationData":[TD([[makeQuery(id+"F20.imprint","IMPRINT",EDGE,{"derivedFrom":sQuery(id+"F20.wireOp",EDGE,"E47.5.0.2")}),-1.0]])]});
            var Q6;
            Q6=makeQuery(id+"F20.imprint","IMPRINT",FACE,{"disambiguationData":[TD([[makeQuery(id+"F20.imprint","IMPRINT",EDGE,{"derivedFrom":sQuery(id+"F20.wireOp",EDGE,"E47.6.0.2")}),-1.0]])]});
            var Q7;
            Q7=makeQuery(id+"F20.imprint","IMPRINT",FACE,{"disambiguationData":[TD([[makeQuery(id+"F20.imprint","IMPRINT",EDGE,{"derivedFrom":sQuery(id+"F20.wireOp",EDGE,"E47.7.0.2")}),-1.0]])]});
            var Q8;
            Q8=makeQuery(id+"F20.imprint","IMPRINT",FACE,{"disambiguationData":[TD([[makeQuery(id+"F20.imprint","IMPRINT",EDGE,{"derivedFrom":sQuery(id+"F20.wireOp",EDGE,"E47.8.0.2")}),-1.0]])]});
            var Q9;
            Q9=makeQuery(id+"F20.imprint","IMPRINT",FACE,{"disambiguationData":[TD([[makeQuery(id+"F20.imprint","IMPRINT",EDGE,{"derivedFrom":sQuery(id+"F20.wireOp",EDGE,"E47.9.0.2")}),-1.0]])]});
            var Q10;
            Q10=makeQuery(id+"F20.imprint","IMPRINT",FACE,{"disambiguationData":[TD([[makeQuery(id+"F20.imprint","IMPRINT",EDGE,{"derivedFrom":sQuery(id+"F20.wireOp",EDGE,"E47.10.0.2")}),-1.0]])]});
            var Q11;
            Q11=makeQuery(id+"F20.imprint","IMPRINT",FACE,{"disambiguationData":[TD([[makeQuery(id+"F20.imprint","IMPRINT",EDGE,{"derivedFrom":sQuery(id+"F20.wireOp",EDGE,"E47.11.0.2")}),-1.0]])]});
            var Q12;
            Q12=makeQuery(id+"F20.imprint","IMPRINT",FACE,{"disambiguationData":[TD([[makeQuery(id+"F20.imprint","IMPRINT",EDGE,{"derivedFrom":sQuery(id+"F20.wireOp",EDGE,"E47.12.0.2")}),-1.0]])]});
            var Q13;
            Q13=makeQuery(id+"F20.imprint","IMPRINT",FACE,{"disambiguationData":[TD([[makeQuery(id+"F20.imprint","IMPRINT",EDGE,{"derivedFrom":sQuery(id+"F20.wireOp",EDGE,"E47.13.0.2")}),-1.0]])]});
            var Q14;
            Q14=makeQuery(id+"F20.imprint","IMPRINT",FACE,{"disambiguationData":[TD([[makeQuery(id+"F20.imprint","IMPRINT",EDGE,{"derivedFrom":sQuery(id+"F20.wireOp",EDGE,"E47.14.0.2")}),-1.0]])]});
            var Q15;
            Q15=makeQuery(id+"F20.imprint","IMPRINT",FACE,{"disambiguationData":[TD([[makeQuery(id+"F20.imprint","IMPRINT",EDGE,{"derivedFrom":sQuery(id+"F20.wireOp",EDGE,"E47.15.0.2")}),-1.0]])]});
            extrude(context, id + "F21", {"entities" : qUnion([Q0, Q1, Q2, Q3, Q4, Q5, Q6, Q7, Q8, Q9, Q10, Q11, Q12, Q13, Q14, Q15]), "operationType" : NewBodyOperationType.ADD, "oppositeDirection" : true, "depth" : 19.5 * mm});
        }
        {
            var Q0;
            Q0=makeQuery(id+"F1.opExtrude","CAP_FACE",FACE,{"disambiguationData":[OSD([sQuery(id+"F0.wireOp",EDGE,"E0"),sQuery(id+"F0.wireOp",EDGE,"E1"),sQuery(id+"F0.wireOp",EDGE,"E2.bottom"),sQuery(id+"F0.wireOp",EDGE,"E2.top"),sQuery(id+"F0.wireOp",EDGE,"E2.left"),sQuery(id+"F0.wireOp",EDGE,"E2.right")])],"isStart":true});
            var sketch = newSketch(context, id + "F22", { "sketchPlane" : qUnion([Q0])});
            skLineSegment(sketch, "E48", {"start": v(0.5, 7.25) * mm, "end": v(0.5, 9.5) * mm});
            skLineSegment(sketch, "E49", {"start": v(3, 7.25) * mm, "end": v(3, 9.5) * mm});
            skPoint(sketch, "E50.visualSharp", {"position": v(0.5, 10) * mm});
            skArc(sketch, "E50.filletArc", {"start": v(1, 10) * mm, "mid": v(0.65, 9.85) * mm, "end": v(0.5, 9.5) * mm});
            skPoint(sketch, "E51.visualSharp", {"position": v(3, 10) * mm});
            skArc(sketch, "E51.filletArc", {"start": v(3, 9.5) * mm, "mid": v(2.86, 9.85) * mm, "end": v(2.5, 10) * mm});
            skPoint(sketch, "E52.visualSharp", {"position": v(0.5, 7) * mm});
            skArc(sketch, "E52.filletArc", {"start": v(0.25, 7) * mm, "mid": v(0.43, 7.07) * mm, "end": v(0.5, 7.25) * mm});
            skPoint(sketch, "E53.visualSharp", {"position": v(3, 7) * mm});
            skArc(sketch, "E53.filletArc", {"start": v(3, 7.25) * mm, "mid": v(3.08, 7.07) * mm, "end": v(3.25, 7) * mm});
            skLineSegment(sketch, "E54", {"start": v(1, 10) * mm, "end": v(0, 10) * mm});
            skLineSegment(sketch, "E55", {"start": v(0, 10) * mm, "end": v(0, 7) * mm});
            skLineSegment(sketch, "E56", {"start": v(4.5, 7.25) * mm, "end": v(4.5, 9.5) * mm});
            skLineSegment(sketch, "E57", {"start": v(7, 7.25) * mm, "end": v(7, 9.5) * mm});
            skArc(sketch, "E58.filletArc", {"start": v(5, 10) * mm, "mid": v(4.65, 9.85) * mm, "end": v(4.5, 9.5) * mm});
            skArc(sketch, "E59.filletArc", {"start": v(7, 9.5) * mm, "mid": v(6.86, 9.85) * mm, "end": v(6.5, 10) * mm});
            skArc(sketch, "E60.filletArc", {"start": v(7, 7.25) * mm, "mid": v(7.08, 7.07) * mm, "end": v(7.25, 7) * mm});
            skLineSegment(sketch, "E61", {"start": v(8.5, 7.25) * mm, "end": v(8.5, 9.5) * mm});
            skLineSegment(sketch, "E62", {"start": v(11, 7.25) * mm, "end": v(11, 9.5) * mm});
            skArc(sketch, "E63.filletArc", {"start": v(9, 10) * mm, "mid": v(8.65, 9.85) * mm, "end": v(8.5, 9.5) * mm});
            skArc(sketch, "E64.filletArc", {"start": v(11, 9.5) * mm, "mid": v(10.86, 9.85) * mm, "end": v(10.5, 10) * mm});
            skArc(sketch, "E65.filletArc", {"start": v(8.25, 7) * mm, "mid": v(8.43, 7.07) * mm, "end": v(8.5, 7.25) * mm});
            skArc(sketch, "E66.filletArc", {"start": v(11, 7.25) * mm, "mid": v(11.08, 7.07) * mm, "end": v(11.25, 7) * mm});
            skLineSegment(sketch, "E67", {"start": v(12.5, 7.25) * mm, "end": v(12.5, 9.5) * mm});
            skLineSegment(sketch, "E68", {"start": v(15, 7.25) * mm, "end": v(15, 9.5) * mm});
            skArc(sketch, "E69.filletArc", {"start": v(13, 10) * mm, "mid": v(12.65, 9.85) * mm, "end": v(12.5, 9.5) * mm});
            skArc(sketch, "E70.filletArc", {"start": v(15, 9.5) * mm, "mid": v(14.86, 9.85) * mm, "end": v(14.5, 10) * mm});
            skArc(sketch, "E71.filletArc", {"start": v(12.25, 7) * mm, "mid": v(12.43, 7.07) * mm, "end": v(12.5, 7.25) * mm});
            skArc(sketch, "E72.filletArc", {"start": v(15, 7.25) * mm, "mid": v(15.08, 7.07) * mm, "end": v(15.25, 7) * mm});
            skLineSegment(sketch, "E73", {"start": v(16.5, 7.25) * mm, "end": v(16.5, 9.5) * mm});
            skLineSegment(sketch, "E74", {"start": v(19, 7.25) * mm, "end": v(19, 9.5) * mm});
            skArc(sketch, "E75.filletArc", {"start": v(17, 10) * mm, "mid": v(16.65, 9.85) * mm, "end": v(16.5, 9.5) * mm});
            skArc(sketch, "E76.filletArc", {"start": v(19, 9.5) * mm, "mid": v(18.86, 9.85) * mm, "end": v(18.5, 10) * mm});
            skArc(sketch, "E77.filletArc", {"start": v(16.25, 7) * mm, "mid": v(16.43, 7.07) * mm, "end": v(16.5, 7.25) * mm});
            skArc(sketch, "E78.filletArc", {"start": v(19, 7.25) * mm, "mid": v(19.08, 7.07) * mm, "end": v(19.25, 7) * mm});
            skLineSegment(sketch, "E79", {"start": v(2.5, 10) * mm, "end": v(5, 10) * mm});
            skLineSegment(sketch, "E80", {"start": v(6.5, 10) * mm, "end": v(9, 10) * mm});
            skLineSegment(sketch, "E81", {"start": v(10.5, 10) * mm, "end": v(13, 10) * mm});
            skLineSegment(sketch, "E82", {"start": v(14.5, 10) * mm, "end": v(17, 10) * mm});
            skLineSegment(sketch, "E83", {"start": v(19.5, 7) * mm, "end": v(19.5, 10) * mm});
            skLineSegment(sketch, "E84", {"start": v(18.5, 10) * mm, "end": v(19.5, 10) * mm});
            skLineSegment(sketch, "E85", {"start": v(-1.4, 7.25) * mm, "end": v(21.71, 7.25) * mm, "construction": true});
            skLineSegment(sketch, "E86", {"start": v(-1.48, 9.75) * mm, "end": v(21.6, 9.75) * mm, "construction": true});
            skLineSegment(sketch, "E87", {"start": v(-1.56, 9.5) * mm, "end": v(21.61, 9.5) * mm, "construction": true});
            skArc(sketch, "E88.filletArc", {"start": v(4.25, 7) * mm, "mid": v(4.43, 7.07) * mm, "end": v(4.5, 7.25) * mm});
            skLineSegment(sketch, "E89", {"start": v(-3.66, 10) * mm, "end": v(23.53, 10) * mm, "construction": true});
            skSolve(sketch);
        }
        {
            var Q0;
            Q0=makeQuery(id+"F22.imprint","IMPRINT",FACE,{"disambiguationData":[TD([[makeQuery(id+"F22.imprint","IMPRINT",EDGE,{"derivedFrom":sQuery(id+"F22.wireOp",EDGE,"E48")}),1.0]])]});
            var Q1;
            Q1=makeQuery(id+"F22.imprint","IMPRINT",FACE,{"disambiguationData":[TD([[makeQuery(id+"F22.imprint","IMPRINT",EDGE,{"derivedFrom":sQuery(id+"F22.wireOp",EDGE,"E49")}),-1.0]])]});
            var Q2;
            {var subQ1=sQuery(id+"F22.wireOp",EDGE,"E57");Q2=makeQuery(id+"F22.imprint","IMPRINT",FACE,{"disambiguationData":[TD([[makeQuery(id+"F22.imprint","IMPRINT",EDGE,{"derivedFrom":subQ1}),-1.0]])]});}
            var Q3;
            Q3=makeQuery(id+"F22.imprint","IMPRINT",FACE,{"disambiguationData":[TD([[makeQuery(id+"F22.imprint","IMPRINT",EDGE,{"derivedFrom":sQuery(id+"F22.wireOp",EDGE,"E62")}),-1.0]])]});
            var Q4;
            Q4=makeQuery(id+"F22.imprint","IMPRINT",FACE,{"disambiguationData":[TD([[makeQuery(id+"F22.imprint","IMPRINT",EDGE,{"derivedFrom":sQuery(id+"F22.wireOp",EDGE,"E68")}),-1.0]])]});
            var Q5;
            Q5=makeQuery(id+"F22.imprint","IMPRINT",FACE,{"disambiguationData":[TD([[makeQuery(id+"F22.imprint","IMPRINT",EDGE,{"derivedFrom":sQuery(id+"F22.wireOp",EDGE,"E74")}),-1.0]])]});
            extrude(context, id + "F23", {"entities" : qUnion([Q0, Q1, Q2, Q3, Q4, Q5]), "operationType" : NewBodyOperationType.REMOVE, "oppositeDirection" : true, "depth" : 66 * mm});
        }
        {
            var Q0;
            Q0=makeQuery(id+"F23.boolean.opBoolean","INTERSECT",EDGE,{"derivedFrom":[makeQuery(id+"F21.opExtrude","SWEPT_FACE",FACE,{"disambiguationData":[OSD([sQuery(id+"F20.wireOp",EDGE,"E47.15.0.7")])]}),makeQuery(id+"F23.opExtrude","SWEPT_FACE",FACE,{"disambiguationData":[OSD([sQuery(id+"F22.wireOp",EDGE,"E48")])]})]});
            var Q1;
            Q1=makeQuery(id+"F23.boolean.opBoolean","INTERSECT",EDGE,{"derivedFrom":[makeQuery(id+"F21.opExtrude","SWEPT_FACE",FACE,{"disambiguationData":[OSD([sQuery(id+"F20.wireOp",EDGE,"E47.15.0.7")])]}),makeQuery(id+"F23.opExtrude","SWEPT_FACE",FACE,{"disambiguationData":[OSD([sQuery(id+"F22.wireOp",EDGE,"E49")])]})]});
            var Q2;
            Q2=makeQuery(id+"F23.boolean.opBoolean","INTERSECT",EDGE,{"derivedFrom":[makeQuery(id+"F21.opExtrude","SWEPT_FACE",FACE,{"disambiguationData":[OSD([sQuery(id+"F20.wireOp",EDGE,"E47.15.0.7")])]}),makeQuery(id+"F23.opExtrude","SWEPT_FACE",FACE,{"disambiguationData":[OSD([sQuery(id+"F22.wireOp",EDGE,"E56")])]})]});
            var Q3;
            Q3=makeQuery(id+"F23.boolean.opBoolean","INTERSECT",EDGE,{"derivedFrom":[makeQuery(id+"F21.opExtrude","SWEPT_FACE",FACE,{"disambiguationData":[OSD([sQuery(id+"F20.wireOp",EDGE,"E47.15.0.7")])]}),makeQuery(id+"F23.opExtrude","SWEPT_FACE",FACE,{"disambiguationData":[OSD([sQuery(id+"F22.wireOp",EDGE,"E57")])]})]});
            var Q4;
            Q4=makeQuery(id+"F23.boolean.opBoolean","INTERSECT",EDGE,{"derivedFrom":[makeQuery(id+"F21.opExtrude","SWEPT_FACE",FACE,{"disambiguationData":[OSD([sQuery(id+"F20.wireOp",EDGE,"E47.15.0.7")])]}),makeQuery(id+"F23.opExtrude","SWEPT_FACE",FACE,{"disambiguationData":[OSD([sQuery(id+"F22.wireOp",EDGE,"E61")])]})]});
            var Q5;
            Q5=makeQuery(id+"F23.boolean.opBoolean","INTERSECT",EDGE,{"derivedFrom":[makeQuery(id+"F21.opExtrude","SWEPT_FACE",FACE,{"disambiguationData":[OSD([sQuery(id+"F20.wireOp",EDGE,"E47.15.0.7")])]}),makeQuery(id+"F23.opExtrude","SWEPT_FACE",FACE,{"disambiguationData":[OSD([sQuery(id+"F22.wireOp",EDGE,"E62")])]})]});
            var Q6;
            Q6=makeQuery(id+"F23.boolean.opBoolean","INTERSECT",EDGE,{"derivedFrom":[makeQuery(id+"F21.opExtrude","SWEPT_FACE",FACE,{"disambiguationData":[OSD([sQuery(id+"F20.wireOp",EDGE,"E47.15.0.7")])]}),makeQuery(id+"F23.opExtrude","SWEPT_FACE",FACE,{"disambiguationData":[OSD([sQuery(id+"F22.wireOp",EDGE,"E67")])]})]});
            var Q7;
            Q7=makeQuery(id+"F23.boolean.opBoolean","INTERSECT",EDGE,{"derivedFrom":[makeQuery(id+"F21.opExtrude","SWEPT_FACE",FACE,{"disambiguationData":[OSD([sQuery(id+"F20.wireOp",EDGE,"E47.15.0.7")])]}),makeQuery(id+"F23.opExtrude","SWEPT_FACE",FACE,{"disambiguationData":[OSD([sQuery(id+"F22.wireOp",EDGE,"E68")])]})]});
            var Q8;
            Q8=makeQuery(id+"F23.boolean.opBoolean","INTERSECT",EDGE,{"derivedFrom":[makeQuery(id+"F21.opExtrude","SWEPT_FACE",FACE,{"disambiguationData":[OSD([sQuery(id+"F20.wireOp",EDGE,"E47.15.0.7")])]}),makeQuery(id+"F23.opExtrude","SWEPT_FACE",FACE,{"disambiguationData":[OSD([sQuery(id+"F22.wireOp",EDGE,"E73")])]})]});
            var Q9;
            Q9=makeQuery(id+"F23.boolean.opBoolean","INTERSECT",EDGE,{"derivedFrom":[makeQuery(id+"F21.opExtrude","SWEPT_FACE",FACE,{"disambiguationData":[OSD([sQuery(id+"F20.wireOp",EDGE,"E47.15.0.7")])]}),makeQuery(id+"F23.opExtrude","SWEPT_FACE",FACE,{"disambiguationData":[OSD([sQuery(id+"F22.wireOp",EDGE,"E74")])]})]});
            var Q10;
            Q10=makeQuery(id+"F23.boolean.opBoolean","INTERSECT",EDGE,{"derivedFrom":[makeQuery(id+"F21.opExtrude","SWEPT_FACE",FACE,{"disambiguationData":[OSD([sQuery(id+"F20.wireOp",EDGE,"E47.15.0.2")])]}),makeQuery(id+"F23.opExtrude","SWEPT_FACE",FACE,{"disambiguationData":[OSD([sQuery(id+"F22.wireOp",EDGE,"E48")])]})]});
            var Q11;
            Q11=makeQuery(id+"F23.boolean.opBoolean","INTERSECT",EDGE,{"derivedFrom":[makeQuery(id+"F21.opExtrude","SWEPT_FACE",FACE,{"disambiguationData":[OSD([sQuery(id+"F20.wireOp",EDGE,"E47.15.0.2")])]}),makeQuery(id+"F23.opExtrude","SWEPT_FACE",FACE,{"disambiguationData":[OSD([sQuery(id+"F22.wireOp",EDGE,"E56")])]})]});
            var Q12;
            Q12=makeQuery(id+"F23.boolean.opBoolean","INTERSECT",EDGE,{"derivedFrom":[makeQuery(id+"F21.opExtrude","SWEPT_FACE",FACE,{"disambiguationData":[OSD([sQuery(id+"F20.wireOp",EDGE,"E47.15.0.2")])]}),makeQuery(id+"F23.opExtrude","SWEPT_FACE",FACE,{"disambiguationData":[OSD([sQuery(id+"F22.wireOp",EDGE,"E61")])]})]});
            var Q13;
            Q13=makeQuery(id+"F23.boolean.opBoolean","INTERSECT",EDGE,{"derivedFrom":[makeQuery(id+"F21.opExtrude","SWEPT_FACE",FACE,{"disambiguationData":[OSD([sQuery(id+"F20.wireOp",EDGE,"E47.15.0.2")])]}),makeQuery(id+"F23.opExtrude","SWEPT_FACE",FACE,{"disambiguationData":[OSD([sQuery(id+"F22.wireOp",EDGE,"E67")])]})]});
            var Q14;
            Q14=makeQuery(id+"F23.boolean.opBoolean","INTERSECT",EDGE,{"derivedFrom":[makeQuery(id+"F21.opExtrude","SWEPT_FACE",FACE,{"disambiguationData":[OSD([sQuery(id+"F20.wireOp",EDGE,"E47.15.0.2")])]}),makeQuery(id+"F23.opExtrude","SWEPT_FACE",FACE,{"disambiguationData":[OSD([sQuery(id+"F22.wireOp",EDGE,"E73")])]})]});
            var Q15;
            Q15=makeQuery(id+"F23.boolean.opBoolean","INTERSECT",EDGE,{"derivedFrom":[makeQuery(id+"F21.opExtrude","SWEPT_FACE",FACE,{"disambiguationData":[OSD([sQuery(id+"F20.wireOp",EDGE,"E47.15.0.2")])]}),makeQuery(id+"F23.opExtrude","SWEPT_FACE",FACE,{"disambiguationData":[OSD([sQuery(id+"F22.wireOp",EDGE,"E74")])]})]});
            var Q16;
            Q16=makeQuery(id+"F23.boolean.opBoolean","INTERSECT",EDGE,{"derivedFrom":[makeQuery(id+"F21.opExtrude","SWEPT_FACE",FACE,{"disambiguationData":[OSD([sQuery(id+"F20.wireOp",EDGE,"E47.15.0.2")])]}),makeQuery(id+"F23.opExtrude","SWEPT_FACE",FACE,{"disambiguationData":[OSD([sQuery(id+"F22.wireOp",EDGE,"E68")])]})]});
            var Q17;
            Q17=makeQuery(id+"F23.boolean.opBoolean","INTERSECT",EDGE,{"derivedFrom":[makeQuery(id+"F21.opExtrude","SWEPT_FACE",FACE,{"disambiguationData":[OSD([sQuery(id+"F20.wireOp",EDGE,"E47.15.0.2")])]}),makeQuery(id+"F23.opExtrude","SWEPT_FACE",FACE,{"disambiguationData":[OSD([sQuery(id+"F22.wireOp",EDGE,"E62")])]})]});
            var Q18;
            Q18=makeQuery(id+"F23.boolean.opBoolean","INTERSECT",EDGE,{"derivedFrom":[makeQuery(id+"F21.opExtrude","SWEPT_FACE",FACE,{"disambiguationData":[OSD([sQuery(id+"F20.wireOp",EDGE,"E47.15.0.2")])]}),makeQuery(id+"F23.opExtrude","SWEPT_FACE",FACE,{"disambiguationData":[OSD([sQuery(id+"F22.wireOp",EDGE,"E57")])]})]});
            var Q19;
            Q19=makeQuery(id+"F23.boolean.opBoolean","INTERSECT",EDGE,{"derivedFrom":[makeQuery(id+"F21.opExtrude","SWEPT_FACE",FACE,{"disambiguationData":[OSD([sQuery(id+"F20.wireOp",EDGE,"E47.15.0.2")])]}),makeQuery(id+"F23.opExtrude","SWEPT_FACE",FACE,{"disambiguationData":[OSD([sQuery(id+"F22.wireOp",EDGE,"E49")])]})]});
            var Q20;
            Q20=makeQuery(id+"F23.boolean.opBoolean","INTERSECT",EDGE,{"derivedFrom":[makeQuery(id+"F21.opExtrude","SWEPT_FACE",FACE,{"disambiguationData":[OSD([sQuery(id+"F20.wireOp",EDGE,"E47.14.0.7")])]}),makeQuery(id+"F23.opExtrude","SWEPT_FACE",FACE,{"disambiguationData":[OSD([sQuery(id+"F22.wireOp",EDGE,"E74")])]})]});
            var Q21;
            Q21=makeQuery(id+"F23.boolean.opBoolean","INTERSECT",EDGE,{"derivedFrom":[makeQuery(id+"F21.opExtrude","SWEPT_FACE",FACE,{"disambiguationData":[OSD([sQuery(id+"F20.wireOp",EDGE,"E47.14.0.7")])]}),makeQuery(id+"F23.opExtrude","SWEPT_FACE",FACE,{"disambiguationData":[OSD([sQuery(id+"F22.wireOp",EDGE,"E73")])]})]});
            var Q22;
            Q22=makeQuery(id+"F23.boolean.opBoolean","INTERSECT",EDGE,{"derivedFrom":[makeQuery(id+"F21.opExtrude","SWEPT_FACE",FACE,{"disambiguationData":[OSD([sQuery(id+"F20.wireOp",EDGE,"E47.14.0.7")])]}),makeQuery(id+"F23.opExtrude","SWEPT_FACE",FACE,{"disambiguationData":[OSD([sQuery(id+"F22.wireOp",EDGE,"E68")])]})]});
            var Q23;
            Q23=makeQuery(id+"F23.boolean.opBoolean","INTERSECT",EDGE,{"derivedFrom":[makeQuery(id+"F21.opExtrude","SWEPT_FACE",FACE,{"disambiguationData":[OSD([sQuery(id+"F20.wireOp",EDGE,"E47.14.0.7")])]}),makeQuery(id+"F23.opExtrude","SWEPT_FACE",FACE,{"disambiguationData":[OSD([sQuery(id+"F22.wireOp",EDGE,"E67")])]})]});
            var Q24;
            Q24=makeQuery(id+"F23.boolean.opBoolean","INTERSECT",EDGE,{"derivedFrom":[makeQuery(id+"F21.opExtrude","SWEPT_FACE",FACE,{"disambiguationData":[OSD([sQuery(id+"F20.wireOp",EDGE,"E47.14.0.7")])]}),makeQuery(id+"F23.opExtrude","SWEPT_FACE",FACE,{"disambiguationData":[OSD([sQuery(id+"F22.wireOp",EDGE,"E62")])]})]});
            var Q25;
            Q25=makeQuery(id+"F23.boolean.opBoolean","INTERSECT",EDGE,{"derivedFrom":[makeQuery(id+"F21.opExtrude","SWEPT_FACE",FACE,{"disambiguationData":[OSD([sQuery(id+"F20.wireOp",EDGE,"E47.14.0.7")])]}),makeQuery(id+"F23.opExtrude","SWEPT_FACE",FACE,{"disambiguationData":[OSD([sQuery(id+"F22.wireOp",EDGE,"E61")])]})]});
            var Q26;
            Q26=makeQuery(id+"F23.boolean.opBoolean","INTERSECT",EDGE,{"derivedFrom":[makeQuery(id+"F21.opExtrude","SWEPT_FACE",FACE,{"disambiguationData":[OSD([sQuery(id+"F20.wireOp",EDGE,"E47.14.0.7")])]}),makeQuery(id+"F23.opExtrude","SWEPT_FACE",FACE,{"disambiguationData":[OSD([sQuery(id+"F22.wireOp",EDGE,"E57")])]})]});
            var Q27;
            Q27=makeQuery(id+"F23.boolean.opBoolean","INTERSECT",EDGE,{"derivedFrom":[makeQuery(id+"F21.opExtrude","SWEPT_FACE",FACE,{"disambiguationData":[OSD([sQuery(id+"F20.wireOp",EDGE,"E47.14.0.7")])]}),makeQuery(id+"F23.opExtrude","SWEPT_FACE",FACE,{"disambiguationData":[OSD([sQuery(id+"F22.wireOp",EDGE,"E56")])]})]});
            var Q28;
            Q28=makeQuery(id+"F23.boolean.opBoolean","INTERSECT",EDGE,{"derivedFrom":[makeQuery(id+"F21.opExtrude","SWEPT_FACE",FACE,{"disambiguationData":[OSD([sQuery(id+"F20.wireOp",EDGE,"E47.14.0.7")])]}),makeQuery(id+"F23.opExtrude","SWEPT_FACE",FACE,{"disambiguationData":[OSD([sQuery(id+"F22.wireOp",EDGE,"E49")])]})]});
            var Q29;
            Q29=makeQuery(id+"F23.boolean.opBoolean","INTERSECT",EDGE,{"derivedFrom":[makeQuery(id+"F21.opExtrude","SWEPT_FACE",FACE,{"disambiguationData":[OSD([sQuery(id+"F20.wireOp",EDGE,"E47.14.0.7")])]}),makeQuery(id+"F23.opExtrude","SWEPT_FACE",FACE,{"disambiguationData":[OSD([sQuery(id+"F22.wireOp",EDGE,"E48")])]})]});
            var Q30;
            Q30=makeQuery(id+"F23.boolean.opBoolean","INTERSECT",EDGE,{"derivedFrom":[makeQuery(id+"F21.opExtrude","SWEPT_FACE",FACE,{"disambiguationData":[OSD([sQuery(id+"F20.wireOp",EDGE,"E47.13.0.7")])]}),makeQuery(id+"F23.opExtrude","SWEPT_FACE",FACE,{"disambiguationData":[OSD([sQuery(id+"F22.wireOp",EDGE,"E74")])]})]});
            var Q31;
            Q31=makeQuery(id+"F23.boolean.opBoolean","INTERSECT",EDGE,{"derivedFrom":[makeQuery(id+"F21.opExtrude","SWEPT_FACE",FACE,{"disambiguationData":[OSD([sQuery(id+"F20.wireOp",EDGE,"E47.13.0.7")])]}),makeQuery(id+"F23.opExtrude","SWEPT_FACE",FACE,{"disambiguationData":[OSD([sQuery(id+"F22.wireOp",EDGE,"E68")])]})]});
            var Q32;
            Q32=makeQuery(id+"F23.boolean.opBoolean","INTERSECT",EDGE,{"derivedFrom":[makeQuery(id+"F21.opExtrude","SWEPT_FACE",FACE,{"disambiguationData":[OSD([sQuery(id+"F20.wireOp",EDGE,"E47.13.0.7")])]}),makeQuery(id+"F23.opExtrude","SWEPT_FACE",FACE,{"disambiguationData":[OSD([sQuery(id+"F22.wireOp",EDGE,"E62")])]})]});
            var Q33;
            Q33=makeQuery(id+"F23.boolean.opBoolean","INTERSECT",EDGE,{"derivedFrom":[makeQuery(id+"F21.opExtrude","SWEPT_FACE",FACE,{"disambiguationData":[OSD([sQuery(id+"F20.wireOp",EDGE,"E47.13.0.7")])]}),makeQuery(id+"F23.opExtrude","SWEPT_FACE",FACE,{"disambiguationData":[OSD([sQuery(id+"F22.wireOp",EDGE,"E61")])]})]});
            var Q34;
            Q34=makeQuery(id+"F23.boolean.opBoolean","INTERSECT",EDGE,{"derivedFrom":[makeQuery(id+"F21.opExtrude","SWEPT_FACE",FACE,{"disambiguationData":[OSD([sQuery(id+"F20.wireOp",EDGE,"E47.13.0.7")])]}),makeQuery(id+"F23.opExtrude","SWEPT_FACE",FACE,{"disambiguationData":[OSD([sQuery(id+"F22.wireOp",EDGE,"E57")])]})]});
            var Q35;
            Q35=makeQuery(id+"F23.boolean.opBoolean","INTERSECT",EDGE,{"derivedFrom":[makeQuery(id+"F21.opExtrude","SWEPT_FACE",FACE,{"disambiguationData":[OSD([sQuery(id+"F20.wireOp",EDGE,"E47.13.0.7")])]}),makeQuery(id+"F23.opExtrude","SWEPT_FACE",FACE,{"disambiguationData":[OSD([sQuery(id+"F22.wireOp",EDGE,"E56")])]})]});
            var Q36;
            Q36=makeQuery(id+"F23.boolean.opBoolean","INTERSECT",EDGE,{"derivedFrom":[makeQuery(id+"F21.opExtrude","SWEPT_FACE",FACE,{"disambiguationData":[OSD([sQuery(id+"F20.wireOp",EDGE,"E47.13.0.7")])]}),makeQuery(id+"F23.opExtrude","SWEPT_FACE",FACE,{"disambiguationData":[OSD([sQuery(id+"F22.wireOp",EDGE,"E49")])]})]});
            var Q37;
            Q37=makeQuery(id+"F23.boolean.opBoolean","INTERSECT",EDGE,{"derivedFrom":[makeQuery(id+"F21.opExtrude","SWEPT_FACE",FACE,{"disambiguationData":[OSD([sQuery(id+"F20.wireOp",EDGE,"E47.13.0.7")])]}),makeQuery(id+"F23.opExtrude","SWEPT_FACE",FACE,{"disambiguationData":[OSD([sQuery(id+"F22.wireOp",EDGE,"E48")])]})]});
            var Q38;
            Q38=makeQuery(id+"F23.boolean.opBoolean","INTERSECT",EDGE,{"derivedFrom":[makeQuery(id+"F21.opExtrude","SWEPT_FACE",FACE,{"disambiguationData":[OSD([sQuery(id+"F20.wireOp",EDGE,"E47.12.0.7")])]}),makeQuery(id+"F23.opExtrude","SWEPT_FACE",FACE,{"disambiguationData":[OSD([sQuery(id+"F22.wireOp",EDGE,"E48")])]})]});
            var Q39;
            Q39=makeQuery(id+"F23.boolean.opBoolean","INTERSECT",EDGE,{"derivedFrom":[makeQuery(id+"F21.opExtrude","SWEPT_FACE",FACE,{"disambiguationData":[OSD([sQuery(id+"F20.wireOp",EDGE,"E47.12.0.7")])]}),makeQuery(id+"F23.opExtrude","SWEPT_FACE",FACE,{"disambiguationData":[OSD([sQuery(id+"F22.wireOp",EDGE,"E49")])]})]});
            var Q40;
            Q40=makeQuery(id+"F23.boolean.opBoolean","INTERSECT",EDGE,{"derivedFrom":[makeQuery(id+"F21.opExtrude","SWEPT_FACE",FACE,{"disambiguationData":[OSD([sQuery(id+"F20.wireOp",EDGE,"E47.12.0.7")])]}),makeQuery(id+"F23.opExtrude","SWEPT_FACE",FACE,{"disambiguationData":[OSD([sQuery(id+"F22.wireOp",EDGE,"E56")])]})]});
            var Q41;
            Q41=makeQuery(id+"F23.boolean.opBoolean","INTERSECT",EDGE,{"derivedFrom":[makeQuery(id+"F21.opExtrude","SWEPT_FACE",FACE,{"disambiguationData":[OSD([sQuery(id+"F20.wireOp",EDGE,"E47.12.0.7")])]}),makeQuery(id+"F23.opExtrude","SWEPT_FACE",FACE,{"disambiguationData":[OSD([sQuery(id+"F22.wireOp",EDGE,"E57")])]})]});
            var Q42;
            Q42=makeQuery(id+"F23.boolean.opBoolean","INTERSECT",EDGE,{"derivedFrom":[makeQuery(id+"F21.opExtrude","SWEPT_FACE",FACE,{"disambiguationData":[OSD([sQuery(id+"F20.wireOp",EDGE,"E47.12.0.7")])]}),makeQuery(id+"F23.opExtrude","SWEPT_FACE",FACE,{"disambiguationData":[OSD([sQuery(id+"F22.wireOp",EDGE,"E61")])]})]});
            var Q43;
            Q43=makeQuery(id+"F23.boolean.opBoolean","INTERSECT",EDGE,{"derivedFrom":[makeQuery(id+"F21.opExtrude","SWEPT_FACE",FACE,{"disambiguationData":[OSD([sQuery(id+"F20.wireOp",EDGE,"E47.12.0.7")])]}),makeQuery(id+"F23.opExtrude","SWEPT_FACE",FACE,{"disambiguationData":[OSD([sQuery(id+"F22.wireOp",EDGE,"E62")])]})]});
            var Q44;
            Q44=makeQuery(id+"F23.boolean.opBoolean","INTERSECT",EDGE,{"derivedFrom":[makeQuery(id+"F21.opExtrude","SWEPT_FACE",FACE,{"disambiguationData":[OSD([sQuery(id+"F20.wireOp",EDGE,"E47.12.0.7")])]}),makeQuery(id+"F23.opExtrude","SWEPT_FACE",FACE,{"disambiguationData":[OSD([sQuery(id+"F22.wireOp",EDGE,"E67")])]})]});
            var Q45;
            Q45=makeQuery(id+"F23.boolean.opBoolean","INTERSECT",EDGE,{"derivedFrom":[makeQuery(id+"F21.opExtrude","SWEPT_FACE",FACE,{"disambiguationData":[OSD([sQuery(id+"F20.wireOp",EDGE,"E47.12.0.7")])]}),makeQuery(id+"F23.opExtrude","SWEPT_FACE",FACE,{"disambiguationData":[OSD([sQuery(id+"F22.wireOp",EDGE,"E68")])]})]});
            var Q46;
            Q46=makeQuery(id+"F23.boolean.opBoolean","INTERSECT",EDGE,{"derivedFrom":[makeQuery(id+"F21.opExtrude","SWEPT_FACE",FACE,{"disambiguationData":[OSD([sQuery(id+"F20.wireOp",EDGE,"E47.12.0.7")])]}),makeQuery(id+"F23.opExtrude","SWEPT_FACE",FACE,{"disambiguationData":[OSD([sQuery(id+"F22.wireOp",EDGE,"E73")])]})]});
            var Q47;
            Q47=makeQuery(id+"F23.boolean.opBoolean","INTERSECT",EDGE,{"derivedFrom":[makeQuery(id+"F21.opExtrude","SWEPT_FACE",FACE,{"disambiguationData":[OSD([sQuery(id+"F20.wireOp",EDGE,"E47.12.0.7")])]}),makeQuery(id+"F23.opExtrude","SWEPT_FACE",FACE,{"disambiguationData":[OSD([sQuery(id+"F22.wireOp",EDGE,"E74")])]})]});
            var Q48;
            Q48=makeQuery(id+"F23.boolean.opBoolean","INTERSECT",EDGE,{"derivedFrom":[makeQuery(id+"F21.opExtrude","SWEPT_FACE",FACE,{"disambiguationData":[OSD([sQuery(id+"F20.wireOp",EDGE,"E47.11.0.7")])]}),makeQuery(id+"F23.opExtrude","SWEPT_FACE",FACE,{"disambiguationData":[OSD([sQuery(id+"F22.wireOp",EDGE,"E74")])]})]});
            var Q49;
            Q49=makeQuery(id+"F23.boolean.opBoolean","INTERSECT",EDGE,{"derivedFrom":[makeQuery(id+"F21.opExtrude","SWEPT_FACE",FACE,{"disambiguationData":[OSD([sQuery(id+"F20.wireOp",EDGE,"E47.11.0.7")])]}),makeQuery(id+"F23.opExtrude","SWEPT_FACE",FACE,{"disambiguationData":[OSD([sQuery(id+"F22.wireOp",EDGE,"E68")])]})]});
            var Q50;
            Q50=makeQuery(id+"F23.boolean.opBoolean","INTERSECT",EDGE,{"derivedFrom":[makeQuery(id+"F21.opExtrude","SWEPT_FACE",FACE,{"disambiguationData":[OSD([sQuery(id+"F20.wireOp",EDGE,"E47.11.0.7")])]}),makeQuery(id+"F23.opExtrude","SWEPT_FACE",FACE,{"disambiguationData":[OSD([sQuery(id+"F22.wireOp",EDGE,"E67")])]})]});
            var Q51;
            Q51=makeQuery(id+"F23.boolean.opBoolean","INTERSECT",EDGE,{"derivedFrom":[makeQuery(id+"F21.opExtrude","SWEPT_FACE",FACE,{"disambiguationData":[OSD([sQuery(id+"F20.wireOp",EDGE,"E47.11.0.7")])]}),makeQuery(id+"F23.opExtrude","SWEPT_FACE",FACE,{"disambiguationData":[OSD([sQuery(id+"F22.wireOp",EDGE,"E62")])]})]});
            var Q52;
            Q52=makeQuery(id+"F23.boolean.opBoolean","INTERSECT",EDGE,{"derivedFrom":[makeQuery(id+"F21.opExtrude","SWEPT_FACE",FACE,{"disambiguationData":[OSD([sQuery(id+"F20.wireOp",EDGE,"E47.11.0.7")])]}),makeQuery(id+"F23.opExtrude","SWEPT_FACE",FACE,{"disambiguationData":[OSD([sQuery(id+"F22.wireOp",EDGE,"E61")])]})]});
            var Q53;
            Q53=makeQuery(id+"F23.boolean.opBoolean","INTERSECT",EDGE,{"derivedFrom":[makeQuery(id+"F21.opExtrude","SWEPT_FACE",FACE,{"disambiguationData":[OSD([sQuery(id+"F20.wireOp",EDGE,"E47.11.0.7")])]}),makeQuery(id+"F23.opExtrude","SWEPT_FACE",FACE,{"disambiguationData":[OSD([sQuery(id+"F22.wireOp",EDGE,"E57")])]})]});
            var Q54;
            Q54=makeQuery(id+"F23.boolean.opBoolean","INTERSECT",EDGE,{"derivedFrom":[makeQuery(id+"F21.opExtrude","SWEPT_FACE",FACE,{"disambiguationData":[OSD([sQuery(id+"F20.wireOp",EDGE,"E47.11.0.7")])]}),makeQuery(id+"F23.opExtrude","SWEPT_FACE",FACE,{"disambiguationData":[OSD([sQuery(id+"F22.wireOp",EDGE,"E56")])]})]});
            var Q55;
            Q55=makeQuery(id+"F23.boolean.opBoolean","INTERSECT",EDGE,{"derivedFrom":[makeQuery(id+"F21.opExtrude","SWEPT_FACE",FACE,{"disambiguationData":[OSD([sQuery(id+"F20.wireOp",EDGE,"E47.11.0.7")])]}),makeQuery(id+"F23.opExtrude","SWEPT_FACE",FACE,{"disambiguationData":[OSD([sQuery(id+"F22.wireOp",EDGE,"E49")])]})]});
            var Q56;
            Q56=makeQuery(id+"F23.boolean.opBoolean","INTERSECT",EDGE,{"derivedFrom":[makeQuery(id+"F21.opExtrude","SWEPT_FACE",FACE,{"disambiguationData":[OSD([sQuery(id+"F20.wireOp",EDGE,"E47.11.0.7")])]}),makeQuery(id+"F23.opExtrude","SWEPT_FACE",FACE,{"disambiguationData":[OSD([sQuery(id+"F22.wireOp",EDGE,"E48")])]})]});
            var Q57;
            Q57=makeQuery(id+"F23.boolean.opBoolean","INTERSECT",EDGE,{"derivedFrom":[makeQuery(id+"F21.opExtrude","SWEPT_FACE",FACE,{"disambiguationData":[OSD([sQuery(id+"F20.wireOp",EDGE,"E47.10.0.7")])]}),makeQuery(id+"F23.opExtrude","SWEPT_FACE",FACE,{"disambiguationData":[OSD([sQuery(id+"F22.wireOp",EDGE,"E48")])]})]});
            var Q58;
            Q58=makeQuery(id+"F23.boolean.opBoolean","INTERSECT",EDGE,{"derivedFrom":[makeQuery(id+"F21.opExtrude","SWEPT_FACE",FACE,{"disambiguationData":[OSD([sQuery(id+"F20.wireOp",EDGE,"E47.10.0.7")])]}),makeQuery(id+"F23.opExtrude","SWEPT_FACE",FACE,{"disambiguationData":[OSD([sQuery(id+"F22.wireOp",EDGE,"E49")])]})]});
            var Q59;
            Q59=makeQuery(id+"F23.boolean.opBoolean","INTERSECT",EDGE,{"derivedFrom":[makeQuery(id+"F21.opExtrude","SWEPT_FACE",FACE,{"disambiguationData":[OSD([sQuery(id+"F20.wireOp",EDGE,"E47.10.0.7")])]}),makeQuery(id+"F23.opExtrude","SWEPT_FACE",FACE,{"disambiguationData":[OSD([sQuery(id+"F22.wireOp",EDGE,"E56")])]})]});
            var Q60;
            Q60=makeQuery(id+"F23.boolean.opBoolean","INTERSECT",EDGE,{"derivedFrom":[makeQuery(id+"F21.opExtrude","SWEPT_FACE",FACE,{"disambiguationData":[OSD([sQuery(id+"F20.wireOp",EDGE,"E47.10.0.7")])]}),makeQuery(id+"F23.opExtrude","SWEPT_FACE",FACE,{"disambiguationData":[OSD([sQuery(id+"F22.wireOp",EDGE,"E57")])]})]});
            var Q61;
            Q61=makeQuery(id+"F23.boolean.opBoolean","INTERSECT",EDGE,{"derivedFrom":[makeQuery(id+"F21.opExtrude","SWEPT_FACE",FACE,{"disambiguationData":[OSD([sQuery(id+"F20.wireOp",EDGE,"E47.10.0.7")])]}),makeQuery(id+"F23.opExtrude","SWEPT_FACE",FACE,{"disambiguationData":[OSD([sQuery(id+"F22.wireOp",EDGE,"E61")])]})]});
            var Q62;
            Q62=makeQuery(id+"F23.boolean.opBoolean","INTERSECT",EDGE,{"derivedFrom":[makeQuery(id+"F21.opExtrude","SWEPT_FACE",FACE,{"disambiguationData":[OSD([sQuery(id+"F20.wireOp",EDGE,"E47.10.0.7")])]}),makeQuery(id+"F23.opExtrude","SWEPT_FACE",FACE,{"disambiguationData":[OSD([sQuery(id+"F22.wireOp",EDGE,"E62")])]})]});
            var Q63;
            Q63=makeQuery(id+"F23.boolean.opBoolean","INTERSECT",EDGE,{"derivedFrom":[makeQuery(id+"F21.opExtrude","SWEPT_FACE",FACE,{"disambiguationData":[OSD([sQuery(id+"F20.wireOp",EDGE,"E47.10.0.7")])]}),makeQuery(id+"F23.opExtrude","SWEPT_FACE",FACE,{"disambiguationData":[OSD([sQuery(id+"F22.wireOp",EDGE,"E67")])]})]});
            var Q64;
            Q64=makeQuery(id+"F23.boolean.opBoolean","INTERSECT",EDGE,{"derivedFrom":[makeQuery(id+"F21.opExtrude","SWEPT_FACE",FACE,{"disambiguationData":[OSD([sQuery(id+"F20.wireOp",EDGE,"E47.10.0.7")])]}),makeQuery(id+"F23.opExtrude","SWEPT_FACE",FACE,{"disambiguationData":[OSD([sQuery(id+"F22.wireOp",EDGE,"E68")])]})]});
            var Q65;
            Q65=makeQuery(id+"F23.boolean.opBoolean","INTERSECT",EDGE,{"derivedFrom":[makeQuery(id+"F21.opExtrude","SWEPT_FACE",FACE,{"disambiguationData":[OSD([sQuery(id+"F20.wireOp",EDGE,"E47.10.0.7")])]}),makeQuery(id+"F23.opExtrude","SWEPT_FACE",FACE,{"disambiguationData":[OSD([sQuery(id+"F22.wireOp",EDGE,"E73")])]})]});
            var Q66;
            Q66=makeQuery(id+"F23.boolean.opBoolean","INTERSECT",EDGE,{"derivedFrom":[makeQuery(id+"F21.opExtrude","SWEPT_FACE",FACE,{"disambiguationData":[OSD([sQuery(id+"F20.wireOp",EDGE,"E47.10.0.7")])]}),makeQuery(id+"F23.opExtrude","SWEPT_FACE",FACE,{"disambiguationData":[OSD([sQuery(id+"F22.wireOp",EDGE,"E74")])]})]});
            var Q67;
            Q67=makeQuery(id+"F23.boolean.opBoolean","INTERSECT",EDGE,{"derivedFrom":[makeQuery(id+"F21.opExtrude","SWEPT_FACE",FACE,{"disambiguationData":[OSD([sQuery(id+"F20.wireOp",EDGE,"E47.9.0.7")])]}),makeQuery(id+"F23.opExtrude","SWEPT_FACE",FACE,{"disambiguationData":[OSD([sQuery(id+"F22.wireOp",EDGE,"E74")])]})]});
            var Q68;
            Q68=makeQuery(id+"F23.boolean.opBoolean","INTERSECT",EDGE,{"derivedFrom":[makeQuery(id+"F21.opExtrude","SWEPT_FACE",FACE,{"disambiguationData":[OSD([sQuery(id+"F20.wireOp",EDGE,"E47.9.0.7")])]}),makeQuery(id+"F23.opExtrude","SWEPT_FACE",FACE,{"disambiguationData":[OSD([sQuery(id+"F22.wireOp",EDGE,"E73")])]})]});
            var Q69;
            Q69=makeQuery(id+"F23.boolean.opBoolean","INTERSECT",EDGE,{"derivedFrom":[makeQuery(id+"F21.opExtrude","SWEPT_FACE",FACE,{"disambiguationData":[OSD([sQuery(id+"F20.wireOp",EDGE,"E47.9.0.7")])]}),makeQuery(id+"F23.opExtrude","SWEPT_FACE",FACE,{"disambiguationData":[OSD([sQuery(id+"F22.wireOp",EDGE,"E68")])]})]});
            var Q70;
            Q70=makeQuery(id+"F23.boolean.opBoolean","INTERSECT",EDGE,{"derivedFrom":[makeQuery(id+"F21.opExtrude","SWEPT_FACE",FACE,{"disambiguationData":[OSD([sQuery(id+"F20.wireOp",EDGE,"E47.9.0.7")])]}),makeQuery(id+"F23.opExtrude","SWEPT_FACE",FACE,{"disambiguationData":[OSD([sQuery(id+"F22.wireOp",EDGE,"E67")])]})]});
            var Q71;
            Q71=makeQuery(id+"F23.boolean.opBoolean","INTERSECT",EDGE,{"derivedFrom":[makeQuery(id+"F21.opExtrude","SWEPT_FACE",FACE,{"disambiguationData":[OSD([sQuery(id+"F20.wireOp",EDGE,"E47.9.0.7")])]}),makeQuery(id+"F23.opExtrude","SWEPT_FACE",FACE,{"disambiguationData":[OSD([sQuery(id+"F22.wireOp",EDGE,"E62")])]})]});
            var Q72;
            Q72=makeQuery(id+"F23.boolean.opBoolean","INTERSECT",EDGE,{"derivedFrom":[makeQuery(id+"F21.opExtrude","SWEPT_FACE",FACE,{"disambiguationData":[OSD([sQuery(id+"F20.wireOp",EDGE,"E47.9.0.7")])]}),makeQuery(id+"F23.opExtrude","SWEPT_FACE",FACE,{"disambiguationData":[OSD([sQuery(id+"F22.wireOp",EDGE,"E61")])]})]});
            var Q73;
            Q73=makeQuery(id+"F23.boolean.opBoolean","INTERSECT",EDGE,{"derivedFrom":[makeQuery(id+"F21.opExtrude","SWEPT_FACE",FACE,{"disambiguationData":[OSD([sQuery(id+"F20.wireOp",EDGE,"E47.9.0.7")])]}),makeQuery(id+"F23.opExtrude","SWEPT_FACE",FACE,{"disambiguationData":[OSD([sQuery(id+"F22.wireOp",EDGE,"E57")])]})]});
            var Q74;
            Q74=makeQuery(id+"F23.boolean.opBoolean","INTERSECT",EDGE,{"derivedFrom":[makeQuery(id+"F21.opExtrude","SWEPT_FACE",FACE,{"disambiguationData":[OSD([sQuery(id+"F20.wireOp",EDGE,"E47.9.0.7")])]}),makeQuery(id+"F23.opExtrude","SWEPT_FACE",FACE,{"disambiguationData":[OSD([sQuery(id+"F22.wireOp",EDGE,"E56")])]})]});
            var Q75;
            Q75=makeQuery(id+"F23.boolean.opBoolean","INTERSECT",EDGE,{"derivedFrom":[makeQuery(id+"F21.opExtrude","SWEPT_FACE",FACE,{"disambiguationData":[OSD([sQuery(id+"F20.wireOp",EDGE,"E47.9.0.7")])]}),makeQuery(id+"F23.opExtrude","SWEPT_FACE",FACE,{"disambiguationData":[OSD([sQuery(id+"F22.wireOp",EDGE,"E49")])]})]});
            var Q76;
            Q76=makeQuery(id+"F23.boolean.opBoolean","INTERSECT",EDGE,{"derivedFrom":[makeQuery(id+"F21.opExtrude","SWEPT_FACE",FACE,{"disambiguationData":[OSD([sQuery(id+"F20.wireOp",EDGE,"E47.9.0.7")])]}),makeQuery(id+"F23.opExtrude","SWEPT_FACE",FACE,{"disambiguationData":[OSD([sQuery(id+"F22.wireOp",EDGE,"E48")])]})]});
            var Q77;
            Q77=makeQuery(id+"F23.boolean.opBoolean","INTERSECT",EDGE,{"derivedFrom":[makeQuery(id+"F21.opExtrude","SWEPT_FACE",FACE,{"disambiguationData":[OSD([sQuery(id+"F20.wireOp",EDGE,"E47.8.0.7")])]}),makeQuery(id+"F23.opExtrude","SWEPT_FACE",FACE,{"disambiguationData":[OSD([sQuery(id+"F22.wireOp",EDGE,"E48")])]})]});
            var Q78;
            Q78=makeQuery(id+"F23.boolean.opBoolean","INTERSECT",EDGE,{"derivedFrom":[makeQuery(id+"F21.opExtrude","SWEPT_FACE",FACE,{"disambiguationData":[OSD([sQuery(id+"F20.wireOp",EDGE,"E47.8.0.7")])]}),makeQuery(id+"F23.opExtrude","SWEPT_FACE",FACE,{"disambiguationData":[OSD([sQuery(id+"F22.wireOp",EDGE,"E49")])]})]});
            var Q79;
            Q79=makeQuery(id+"F23.boolean.opBoolean","INTERSECT",EDGE,{"derivedFrom":[makeQuery(id+"F21.opExtrude","SWEPT_FACE",FACE,{"disambiguationData":[OSD([sQuery(id+"F20.wireOp",EDGE,"E47.8.0.7")])]}),makeQuery(id+"F23.opExtrude","SWEPT_FACE",FACE,{"disambiguationData":[OSD([sQuery(id+"F22.wireOp",EDGE,"E56")])]})]});
            var Q80;
            Q80=makeQuery(id+"F23.boolean.opBoolean","INTERSECT",EDGE,{"derivedFrom":[makeQuery(id+"F21.opExtrude","SWEPT_FACE",FACE,{"disambiguationData":[OSD([sQuery(id+"F20.wireOp",EDGE,"E47.8.0.7")])]}),makeQuery(id+"F23.opExtrude","SWEPT_FACE",FACE,{"disambiguationData":[OSD([sQuery(id+"F22.wireOp",EDGE,"E57")])]})]});
            var Q81;
            Q81=makeQuery(id+"F23.boolean.opBoolean","INTERSECT",EDGE,{"derivedFrom":[makeQuery(id+"F21.opExtrude","SWEPT_FACE",FACE,{"disambiguationData":[OSD([sQuery(id+"F20.wireOp",EDGE,"E47.8.0.7")])]}),makeQuery(id+"F23.opExtrude","SWEPT_FACE",FACE,{"disambiguationData":[OSD([sQuery(id+"F22.wireOp",EDGE,"E61")])]})]});
            var Q82;
            Q82=makeQuery(id+"F23.boolean.opBoolean","INTERSECT",EDGE,{"derivedFrom":[makeQuery(id+"F21.opExtrude","SWEPT_FACE",FACE,{"disambiguationData":[OSD([sQuery(id+"F20.wireOp",EDGE,"E47.8.0.7")])]}),makeQuery(id+"F23.opExtrude","SWEPT_FACE",FACE,{"disambiguationData":[OSD([sQuery(id+"F22.wireOp",EDGE,"E62")])]})]});
            var Q83;
            Q83=makeQuery(id+"F23.boolean.opBoolean","INTERSECT",EDGE,{"derivedFrom":[makeQuery(id+"F21.opExtrude","SWEPT_FACE",FACE,{"disambiguationData":[OSD([sQuery(id+"F20.wireOp",EDGE,"E47.8.0.7")])]}),makeQuery(id+"F23.opExtrude","SWEPT_FACE",FACE,{"disambiguationData":[OSD([sQuery(id+"F22.wireOp",EDGE,"E67")])]})]});
            var Q84;
            Q84=makeQuery(id+"F23.boolean.opBoolean","INTERSECT",EDGE,{"derivedFrom":[makeQuery(id+"F21.opExtrude","SWEPT_FACE",FACE,{"disambiguationData":[OSD([sQuery(id+"F20.wireOp",EDGE,"E47.8.0.7")])]}),makeQuery(id+"F23.opExtrude","SWEPT_FACE",FACE,{"disambiguationData":[OSD([sQuery(id+"F22.wireOp",EDGE,"E68")])]})]});
            var Q85;
            Q85=makeQuery(id+"F23.boolean.opBoolean","INTERSECT",EDGE,{"derivedFrom":[makeQuery(id+"F21.opExtrude","SWEPT_FACE",FACE,{"disambiguationData":[OSD([sQuery(id+"F20.wireOp",EDGE,"E47.8.0.7")])]}),makeQuery(id+"F23.opExtrude","SWEPT_FACE",FACE,{"disambiguationData":[OSD([sQuery(id+"F22.wireOp",EDGE,"E73")])]})]});
            var Q86;
            Q86=makeQuery(id+"F23.boolean.opBoolean","INTERSECT",EDGE,{"derivedFrom":[makeQuery(id+"F21.opExtrude","SWEPT_FACE",FACE,{"disambiguationData":[OSD([sQuery(id+"F20.wireOp",EDGE,"E47.8.0.7")])]}),makeQuery(id+"F23.opExtrude","SWEPT_FACE",FACE,{"disambiguationData":[OSD([sQuery(id+"F22.wireOp",EDGE,"E74")])]})]});
            var Q87;
            Q87=makeQuery(id+"F23.boolean.opBoolean","INTERSECT",EDGE,{"derivedFrom":[makeQuery(id+"F21.opExtrude","SWEPT_FACE",FACE,{"disambiguationData":[OSD([sQuery(id+"F20.wireOp",EDGE,"E47.7.0.7")])]}),makeQuery(id+"F23.opExtrude","SWEPT_FACE",FACE,{"disambiguationData":[OSD([sQuery(id+"F22.wireOp",EDGE,"E74")])]})]});
            var Q88;
            Q88=makeQuery(id+"F23.boolean.opBoolean","INTERSECT",EDGE,{"derivedFrom":[makeQuery(id+"F21.opExtrude","SWEPT_FACE",FACE,{"disambiguationData":[OSD([sQuery(id+"F20.wireOp",EDGE,"E47.7.0.7")])]}),makeQuery(id+"F23.opExtrude","SWEPT_FACE",FACE,{"disambiguationData":[OSD([sQuery(id+"F22.wireOp",EDGE,"E73")])]})]});
            var Q89;
            Q89=makeQuery(id+"F23.boolean.opBoolean","INTERSECT",EDGE,{"derivedFrom":[makeQuery(id+"F21.opExtrude","SWEPT_FACE",FACE,{"disambiguationData":[OSD([sQuery(id+"F20.wireOp",EDGE,"E47.7.0.7")])]}),makeQuery(id+"F23.opExtrude","SWEPT_FACE",FACE,{"disambiguationData":[OSD([sQuery(id+"F22.wireOp",EDGE,"E68")])]})]});
            var Q90;
            Q90=makeQuery(id+"F23.boolean.opBoolean","INTERSECT",EDGE,{"derivedFrom":[makeQuery(id+"F21.opExtrude","SWEPT_FACE",FACE,{"disambiguationData":[OSD([sQuery(id+"F20.wireOp",EDGE,"E47.7.0.7")])]}),makeQuery(id+"F23.opExtrude","SWEPT_FACE",FACE,{"disambiguationData":[OSD([sQuery(id+"F22.wireOp",EDGE,"E67")])]})]});
            var Q91;
            Q91=makeQuery(id+"F23.boolean.opBoolean","INTERSECT",EDGE,{"derivedFrom":[makeQuery(id+"F21.opExtrude","SWEPT_FACE",FACE,{"disambiguationData":[OSD([sQuery(id+"F20.wireOp",EDGE,"E47.7.0.7")])]}),makeQuery(id+"F23.opExtrude","SWEPT_FACE",FACE,{"disambiguationData":[OSD([sQuery(id+"F22.wireOp",EDGE,"E62")])]})]});
            var Q92;
            Q92=makeQuery(id+"F23.boolean.opBoolean","INTERSECT",EDGE,{"derivedFrom":[makeQuery(id+"F21.opExtrude","SWEPT_FACE",FACE,{"disambiguationData":[OSD([sQuery(id+"F20.wireOp",EDGE,"E47.7.0.7")])]}),makeQuery(id+"F23.opExtrude","SWEPT_FACE",FACE,{"disambiguationData":[OSD([sQuery(id+"F22.wireOp",EDGE,"E61")])]})]});
            var Q93;
            Q93=makeQuery(id+"F23.boolean.opBoolean","INTERSECT",EDGE,{"derivedFrom":[makeQuery(id+"F21.opExtrude","SWEPT_FACE",FACE,{"disambiguationData":[OSD([sQuery(id+"F20.wireOp",EDGE,"E47.7.0.7")])]}),makeQuery(id+"F23.opExtrude","SWEPT_FACE",FACE,{"disambiguationData":[OSD([sQuery(id+"F22.wireOp",EDGE,"E57")])]})]});
            var Q94;
            Q94=makeQuery(id+"F23.boolean.opBoolean","INTERSECT",EDGE,{"derivedFrom":[makeQuery(id+"F21.opExtrude","SWEPT_FACE",FACE,{"disambiguationData":[OSD([sQuery(id+"F20.wireOp",EDGE,"E47.7.0.7")])]}),makeQuery(id+"F23.opExtrude","SWEPT_FACE",FACE,{"disambiguationData":[OSD([sQuery(id+"F22.wireOp",EDGE,"E56")])]})]});
            var Q95;
            Q95=makeQuery(id+"F23.boolean.opBoolean","INTERSECT",EDGE,{"derivedFrom":[makeQuery(id+"F21.opExtrude","SWEPT_FACE",FACE,{"disambiguationData":[OSD([sQuery(id+"F20.wireOp",EDGE,"E47.7.0.7")])]}),makeQuery(id+"F23.opExtrude","SWEPT_FACE",FACE,{"disambiguationData":[OSD([sQuery(id+"F22.wireOp",EDGE,"E49")])]})]});
            var Q96;
            Q96=makeQuery(id+"F23.boolean.opBoolean","INTERSECT",EDGE,{"derivedFrom":[makeQuery(id+"F21.opExtrude","SWEPT_FACE",FACE,{"disambiguationData":[OSD([sQuery(id+"F20.wireOp",EDGE,"E47.7.0.7")])]}),makeQuery(id+"F23.opExtrude","SWEPT_FACE",FACE,{"disambiguationData":[OSD([sQuery(id+"F22.wireOp",EDGE,"E48")])]})]});
            var Q97;
            Q97=makeQuery(id+"F23.boolean.opBoolean","INTERSECT",EDGE,{"derivedFrom":[makeQuery(id+"F21.opExtrude","SWEPT_FACE",FACE,{"disambiguationData":[OSD([sQuery(id+"F20.wireOp",EDGE,"E47.6.0.7")])]}),makeQuery(id+"F23.opExtrude","SWEPT_FACE",FACE,{"disambiguationData":[OSD([sQuery(id+"F22.wireOp",EDGE,"E48")])]})]});
            var Q98;
            Q98=makeQuery(id+"F23.boolean.opBoolean","INTERSECT",EDGE,{"derivedFrom":[makeQuery(id+"F21.opExtrude","SWEPT_FACE",FACE,{"disambiguationData":[OSD([sQuery(id+"F20.wireOp",EDGE,"E47.6.0.7")])]}),makeQuery(id+"F23.opExtrude","SWEPT_FACE",FACE,{"disambiguationData":[OSD([sQuery(id+"F22.wireOp",EDGE,"E49")])]})]});
            var Q99;
            Q99=makeQuery(id+"F23.boolean.opBoolean","INTERSECT",EDGE,{"derivedFrom":[makeQuery(id+"F21.opExtrude","SWEPT_FACE",FACE,{"disambiguationData":[OSD([sQuery(id+"F20.wireOp",EDGE,"E47.6.0.7")])]}),makeQuery(id+"F23.opExtrude","SWEPT_FACE",FACE,{"disambiguationData":[OSD([sQuery(id+"F22.wireOp",EDGE,"E56")])]})]});
            var Q100;
            Q100=makeQuery(id+"F23.boolean.opBoolean","INTERSECT",EDGE,{"derivedFrom":[makeQuery(id+"F21.opExtrude","SWEPT_FACE",FACE,{"disambiguationData":[OSD([sQuery(id+"F20.wireOp",EDGE,"E47.6.0.7")])]}),makeQuery(id+"F23.opExtrude","SWEPT_FACE",FACE,{"disambiguationData":[OSD([sQuery(id+"F22.wireOp",EDGE,"E57")])]})]});
            var Q101;
            Q101=makeQuery(id+"F23.boolean.opBoolean","INTERSECT",EDGE,{"derivedFrom":[makeQuery(id+"F21.opExtrude","SWEPT_FACE",FACE,{"disambiguationData":[OSD([sQuery(id+"F20.wireOp",EDGE,"E47.6.0.7")])]}),makeQuery(id+"F23.opExtrude","SWEPT_FACE",FACE,{"disambiguationData":[OSD([sQuery(id+"F22.wireOp",EDGE,"E61")])]})]});
            var Q102;
            Q102=makeQuery(id+"F23.boolean.opBoolean","INTERSECT",EDGE,{"derivedFrom":[makeQuery(id+"F21.opExtrude","SWEPT_FACE",FACE,{"disambiguationData":[OSD([sQuery(id+"F20.wireOp",EDGE,"E47.6.0.7")])]}),makeQuery(id+"F23.opExtrude","SWEPT_FACE",FACE,{"disambiguationData":[OSD([sQuery(id+"F22.wireOp",EDGE,"E62")])]})]});
            var Q103;
            Q103=makeQuery(id+"F23.boolean.opBoolean","INTERSECT",EDGE,{"derivedFrom":[makeQuery(id+"F21.opExtrude","SWEPT_FACE",FACE,{"disambiguationData":[OSD([sQuery(id+"F20.wireOp",EDGE,"E47.6.0.7")])]}),makeQuery(id+"F23.opExtrude","SWEPT_FACE",FACE,{"disambiguationData":[OSD([sQuery(id+"F22.wireOp",EDGE,"E67")])]})]});
            var Q104;
            Q104=makeQuery(id+"F23.boolean.opBoolean","INTERSECT",EDGE,{"derivedFrom":[makeQuery(id+"F21.opExtrude","SWEPT_FACE",FACE,{"disambiguationData":[OSD([sQuery(id+"F20.wireOp",EDGE,"E47.6.0.7")])]}),makeQuery(id+"F23.opExtrude","SWEPT_FACE",FACE,{"disambiguationData":[OSD([sQuery(id+"F22.wireOp",EDGE,"E68")])]})]});
            var Q105;
            Q105=makeQuery(id+"F23.boolean.opBoolean","INTERSECT",EDGE,{"derivedFrom":[makeQuery(id+"F21.opExtrude","SWEPT_FACE",FACE,{"disambiguationData":[OSD([sQuery(id+"F20.wireOp",EDGE,"E47.6.0.7")])]}),makeQuery(id+"F23.opExtrude","SWEPT_FACE",FACE,{"disambiguationData":[OSD([sQuery(id+"F22.wireOp",EDGE,"E73")])]})]});
            var Q106;
            Q106=makeQuery(id+"F23.boolean.opBoolean","INTERSECT",EDGE,{"derivedFrom":[makeQuery(id+"F21.opExtrude","SWEPT_FACE",FACE,{"disambiguationData":[OSD([sQuery(id+"F20.wireOp",EDGE,"E47.6.0.7")])]}),makeQuery(id+"F23.opExtrude","SWEPT_FACE",FACE,{"disambiguationData":[OSD([sQuery(id+"F22.wireOp",EDGE,"E74")])]})]});
            var Q107;
            Q107=makeQuery(id+"F23.boolean.opBoolean","INTERSECT",EDGE,{"derivedFrom":[makeQuery(id+"F21.opExtrude","SWEPT_FACE",FACE,{"disambiguationData":[OSD([sQuery(id+"F20.wireOp",EDGE,"E47.5.0.7")])]}),makeQuery(id+"F23.opExtrude","SWEPT_FACE",FACE,{"disambiguationData":[OSD([sQuery(id+"F22.wireOp",EDGE,"E74")])]})]});
            var Q108;
            Q108=makeQuery(id+"F23.boolean.opBoolean","INTERSECT",EDGE,{"derivedFrom":[makeQuery(id+"F21.opExtrude","SWEPT_FACE",FACE,{"disambiguationData":[OSD([sQuery(id+"F20.wireOp",EDGE,"E47.5.0.7")])]}),makeQuery(id+"F23.opExtrude","SWEPT_FACE",FACE,{"disambiguationData":[OSD([sQuery(id+"F22.wireOp",EDGE,"E73")])]})]});
            var Q109;
            Q109=makeQuery(id+"F23.boolean.opBoolean","INTERSECT",EDGE,{"derivedFrom":[makeQuery(id+"F21.opExtrude","SWEPT_FACE",FACE,{"disambiguationData":[OSD([sQuery(id+"F20.wireOp",EDGE,"E47.5.0.7")])]}),makeQuery(id+"F23.opExtrude","SWEPT_FACE",FACE,{"disambiguationData":[OSD([sQuery(id+"F22.wireOp",EDGE,"E68")])]})]});
            var Q110;
            Q110=makeQuery(id+"F23.boolean.opBoolean","INTERSECT",EDGE,{"derivedFrom":[makeQuery(id+"F21.opExtrude","SWEPT_FACE",FACE,{"disambiguationData":[OSD([sQuery(id+"F20.wireOp",EDGE,"E47.5.0.7")])]}),makeQuery(id+"F23.opExtrude","SWEPT_FACE",FACE,{"disambiguationData":[OSD([sQuery(id+"F22.wireOp",EDGE,"E67")])]})]});
            var Q111;
            Q111=makeQuery(id+"F23.boolean.opBoolean","INTERSECT",EDGE,{"derivedFrom":[makeQuery(id+"F21.opExtrude","SWEPT_FACE",FACE,{"disambiguationData":[OSD([sQuery(id+"F20.wireOp",EDGE,"E47.5.0.7")])]}),makeQuery(id+"F23.opExtrude","SWEPT_FACE",FACE,{"disambiguationData":[OSD([sQuery(id+"F22.wireOp",EDGE,"E62")])]})]});
            var Q112;
            Q112=makeQuery(id+"F23.boolean.opBoolean","INTERSECT",EDGE,{"derivedFrom":[makeQuery(id+"F21.opExtrude","SWEPT_FACE",FACE,{"disambiguationData":[OSD([sQuery(id+"F20.wireOp",EDGE,"E47.5.0.7")])]}),makeQuery(id+"F23.opExtrude","SWEPT_FACE",FACE,{"disambiguationData":[OSD([sQuery(id+"F22.wireOp",EDGE,"E61")])]})]});
            var Q113;
            Q113=makeQuery(id+"F23.boolean.opBoolean","INTERSECT",EDGE,{"derivedFrom":[makeQuery(id+"F21.opExtrude","SWEPT_FACE",FACE,{"disambiguationData":[OSD([sQuery(id+"F20.wireOp",EDGE,"E47.5.0.7")])]}),makeQuery(id+"F23.opExtrude","SWEPT_FACE",FACE,{"disambiguationData":[OSD([sQuery(id+"F22.wireOp",EDGE,"E57")])]})]});
            var Q114;
            Q114=makeQuery(id+"F23.boolean.opBoolean","INTERSECT",EDGE,{"derivedFrom":[makeQuery(id+"F21.opExtrude","SWEPT_FACE",FACE,{"disambiguationData":[OSD([sQuery(id+"F20.wireOp",EDGE,"E47.5.0.7")])]}),makeQuery(id+"F23.opExtrude","SWEPT_FACE",FACE,{"disambiguationData":[OSD([sQuery(id+"F22.wireOp",EDGE,"E56")])]})]});
            var Q115;
            Q115=makeQuery(id+"F23.boolean.opBoolean","INTERSECT",EDGE,{"derivedFrom":[makeQuery(id+"F21.opExtrude","SWEPT_FACE",FACE,{"disambiguationData":[OSD([sQuery(id+"F20.wireOp",EDGE,"E47.5.0.7")])]}),makeQuery(id+"F23.opExtrude","SWEPT_FACE",FACE,{"disambiguationData":[OSD([sQuery(id+"F22.wireOp",EDGE,"E49")])]})]});
            var Q116;
            Q116=makeQuery(id+"F23.boolean.opBoolean","INTERSECT",EDGE,{"derivedFrom":[makeQuery(id+"F21.opExtrude","SWEPT_FACE",FACE,{"disambiguationData":[OSD([sQuery(id+"F20.wireOp",EDGE,"E47.5.0.7")])]}),makeQuery(id+"F23.opExtrude","SWEPT_FACE",FACE,{"disambiguationData":[OSD([sQuery(id+"F22.wireOp",EDGE,"E48")])]})]});
            var Q117;
            Q117=makeQuery(id+"F23.boolean.opBoolean","INTERSECT",EDGE,{"derivedFrom":[makeQuery(id+"F21.opExtrude","SWEPT_FACE",FACE,{"disambiguationData":[OSD([sQuery(id+"F20.wireOp",EDGE,"E47.4.0.7")])]}),makeQuery(id+"F23.opExtrude","SWEPT_FACE",FACE,{"disambiguationData":[OSD([sQuery(id+"F22.wireOp",EDGE,"E48")])]})]});
            var Q118;
            Q118=makeQuery(id+"F23.boolean.opBoolean","INTERSECT",EDGE,{"derivedFrom":[makeQuery(id+"F21.opExtrude","SWEPT_FACE",FACE,{"disambiguationData":[OSD([sQuery(id+"F20.wireOp",EDGE,"E47.4.0.7")])]}),makeQuery(id+"F23.opExtrude","SWEPT_FACE",FACE,{"disambiguationData":[OSD([sQuery(id+"F22.wireOp",EDGE,"E49")])]})]});
            var Q119;
            Q119=makeQuery(id+"F23.boolean.opBoolean","INTERSECT",EDGE,{"derivedFrom":[makeQuery(id+"F21.opExtrude","SWEPT_FACE",FACE,{"disambiguationData":[OSD([sQuery(id+"F20.wireOp",EDGE,"E47.4.0.7")])]}),makeQuery(id+"F23.opExtrude","SWEPT_FACE",FACE,{"disambiguationData":[OSD([sQuery(id+"F22.wireOp",EDGE,"E56")])]})]});
            var Q120;
            Q120=makeQuery(id+"F23.boolean.opBoolean","INTERSECT",EDGE,{"derivedFrom":[makeQuery(id+"F21.opExtrude","SWEPT_FACE",FACE,{"disambiguationData":[OSD([sQuery(id+"F20.wireOp",EDGE,"E47.4.0.7")])]}),makeQuery(id+"F23.opExtrude","SWEPT_FACE",FACE,{"disambiguationData":[OSD([sQuery(id+"F22.wireOp",EDGE,"E57")])]})]});
            var Q121;
            Q121=makeQuery(id+"F23.boolean.opBoolean","INTERSECT",EDGE,{"derivedFrom":[makeQuery(id+"F21.opExtrude","SWEPT_FACE",FACE,{"disambiguationData":[OSD([sQuery(id+"F20.wireOp",EDGE,"E47.4.0.7")])]}),makeQuery(id+"F23.opExtrude","SWEPT_FACE",FACE,{"disambiguationData":[OSD([sQuery(id+"F22.wireOp",EDGE,"E61")])]})]});
            var Q122;
            Q122=makeQuery(id+"F23.boolean.opBoolean","INTERSECT",EDGE,{"derivedFrom":[makeQuery(id+"F21.opExtrude","SWEPT_FACE",FACE,{"disambiguationData":[OSD([sQuery(id+"F20.wireOp",EDGE,"E47.4.0.7")])]}),makeQuery(id+"F23.opExtrude","SWEPT_FACE",FACE,{"disambiguationData":[OSD([sQuery(id+"F22.wireOp",EDGE,"E62")])]})]});
            var Q123;
            Q123=makeQuery(id+"F23.boolean.opBoolean","INTERSECT",EDGE,{"derivedFrom":[makeQuery(id+"F21.opExtrude","SWEPT_FACE",FACE,{"disambiguationData":[OSD([sQuery(id+"F20.wireOp",EDGE,"E47.4.0.7")])]}),makeQuery(id+"F23.opExtrude","SWEPT_FACE",FACE,{"disambiguationData":[OSD([sQuery(id+"F22.wireOp",EDGE,"E67")])]})]});
            var Q124;
            Q124=makeQuery(id+"F23.boolean.opBoolean","INTERSECT",EDGE,{"derivedFrom":[makeQuery(id+"F21.opExtrude","SWEPT_FACE",FACE,{"disambiguationData":[OSD([sQuery(id+"F20.wireOp",EDGE,"E47.4.0.7")])]}),makeQuery(id+"F23.opExtrude","SWEPT_FACE",FACE,{"disambiguationData":[OSD([sQuery(id+"F22.wireOp",EDGE,"E68")])]})]});
            var Q125;
            Q125=makeQuery(id+"F23.boolean.opBoolean","INTERSECT",EDGE,{"derivedFrom":[makeQuery(id+"F21.opExtrude","SWEPT_FACE",FACE,{"disambiguationData":[OSD([sQuery(id+"F20.wireOp",EDGE,"E47.4.0.7")])]}),makeQuery(id+"F23.opExtrude","SWEPT_FACE",FACE,{"disambiguationData":[OSD([sQuery(id+"F22.wireOp",EDGE,"E73")])]})]});
            var Q126;
            Q126=makeQuery(id+"F23.boolean.opBoolean","INTERSECT",EDGE,{"derivedFrom":[makeQuery(id+"F21.opExtrude","SWEPT_FACE",FACE,{"disambiguationData":[OSD([sQuery(id+"F20.wireOp",EDGE,"E47.4.0.7")])]}),makeQuery(id+"F23.opExtrude","SWEPT_FACE",FACE,{"disambiguationData":[OSD([sQuery(id+"F22.wireOp",EDGE,"E74")])]})]});
            var Q127;
            Q127=makeQuery(id+"F23.boolean.opBoolean","INTERSECT",EDGE,{"derivedFrom":[makeQuery(id+"F21.opExtrude","SWEPT_FACE",FACE,{"disambiguationData":[OSD([sQuery(id+"F20.wireOp",EDGE,"E47.3.0.7")])]}),makeQuery(id+"F23.opExtrude","SWEPT_FACE",FACE,{"disambiguationData":[OSD([sQuery(id+"F22.wireOp",EDGE,"E48")])]})]});
            var Q128;
            Q128=makeQuery(id+"F23.boolean.opBoolean","INTERSECT",EDGE,{"derivedFrom":[makeQuery(id+"F21.opExtrude","SWEPT_FACE",FACE,{"disambiguationData":[OSD([sQuery(id+"F20.wireOp",EDGE,"E47.3.0.7")])]}),makeQuery(id+"F23.opExtrude","SWEPT_FACE",FACE,{"disambiguationData":[OSD([sQuery(id+"F22.wireOp",EDGE,"E49")])]})]});
            var Q129;
            Q129=makeQuery(id+"F23.boolean.opBoolean","INTERSECT",EDGE,{"derivedFrom":[makeQuery(id+"F21.opExtrude","SWEPT_FACE",FACE,{"disambiguationData":[OSD([sQuery(id+"F20.wireOp",EDGE,"E47.3.0.7")])]}),makeQuery(id+"F23.opExtrude","SWEPT_FACE",FACE,{"disambiguationData":[OSD([sQuery(id+"F22.wireOp",EDGE,"E56")])]})]});
            var Q130;
            Q130=makeQuery(id+"F23.boolean.opBoolean","INTERSECT",EDGE,{"derivedFrom":[makeQuery(id+"F21.opExtrude","SWEPT_FACE",FACE,{"disambiguationData":[OSD([sQuery(id+"F20.wireOp",EDGE,"E47.3.0.7")])]}),makeQuery(id+"F23.opExtrude","SWEPT_FACE",FACE,{"disambiguationData":[OSD([sQuery(id+"F22.wireOp",EDGE,"E57")])]})]});
            var Q131;
            Q131=makeQuery(id+"F23.boolean.opBoolean","INTERSECT",EDGE,{"derivedFrom":[makeQuery(id+"F21.opExtrude","SWEPT_FACE",FACE,{"disambiguationData":[OSD([sQuery(id+"F20.wireOp",EDGE,"E47.3.0.7")])]}),makeQuery(id+"F23.opExtrude","SWEPT_FACE",FACE,{"disambiguationData":[OSD([sQuery(id+"F22.wireOp",EDGE,"E61")])]})]});
            var Q132;
            Q132=makeQuery(id+"F23.boolean.opBoolean","INTERSECT",EDGE,{"derivedFrom":[makeQuery(id+"F21.opExtrude","SWEPT_FACE",FACE,{"disambiguationData":[OSD([sQuery(id+"F20.wireOp",EDGE,"E47.3.0.7")])]}),makeQuery(id+"F23.opExtrude","SWEPT_FACE",FACE,{"disambiguationData":[OSD([sQuery(id+"F22.wireOp",EDGE,"E62")])]})]});
            var Q133;
            Q133=makeQuery(id+"F23.boolean.opBoolean","INTERSECT",EDGE,{"derivedFrom":[makeQuery(id+"F21.opExtrude","SWEPT_FACE",FACE,{"disambiguationData":[OSD([sQuery(id+"F20.wireOp",EDGE,"E47.3.0.7")])]}),makeQuery(id+"F23.opExtrude","SWEPT_FACE",FACE,{"disambiguationData":[OSD([sQuery(id+"F22.wireOp",EDGE,"E67")])]})]});
            var Q134;
            Q134=makeQuery(id+"F23.boolean.opBoolean","INTERSECT",EDGE,{"derivedFrom":[makeQuery(id+"F21.opExtrude","SWEPT_FACE",FACE,{"disambiguationData":[OSD([sQuery(id+"F20.wireOp",EDGE,"E47.3.0.7")])]}),makeQuery(id+"F23.opExtrude","SWEPT_FACE",FACE,{"disambiguationData":[OSD([sQuery(id+"F22.wireOp",EDGE,"E68")])]})]});
            var Q135;
            Q135=makeQuery(id+"F23.boolean.opBoolean","INTERSECT",EDGE,{"derivedFrom":[makeQuery(id+"F21.opExtrude","SWEPT_FACE",FACE,{"disambiguationData":[OSD([sQuery(id+"F20.wireOp",EDGE,"E47.3.0.7")])]}),makeQuery(id+"F23.opExtrude","SWEPT_FACE",FACE,{"disambiguationData":[OSD([sQuery(id+"F22.wireOp",EDGE,"E73")])]})]});
            var Q136;
            Q136=makeQuery(id+"F23.boolean.opBoolean","INTERSECT",EDGE,{"derivedFrom":[makeQuery(id+"F21.opExtrude","SWEPT_FACE",FACE,{"disambiguationData":[OSD([sQuery(id+"F20.wireOp",EDGE,"E47.3.0.7")])]}),makeQuery(id+"F23.opExtrude","SWEPT_FACE",FACE,{"disambiguationData":[OSD([sQuery(id+"F22.wireOp",EDGE,"E74")])]})]});
            var Q137;
            Q137=makeQuery(id+"F23.boolean.opBoolean","INTERSECT",EDGE,{"derivedFrom":[makeQuery(id+"F21.opExtrude","SWEPT_FACE",FACE,{"disambiguationData":[OSD([sQuery(id+"F20.wireOp",EDGE,"E47.2.0.7")])]}),makeQuery(id+"F23.opExtrude","SWEPT_FACE",FACE,{"disambiguationData":[OSD([sQuery(id+"F22.wireOp",EDGE,"E74")])]})]});
            var Q138;
            Q138=makeQuery(id+"F23.boolean.opBoolean","INTERSECT",EDGE,{"derivedFrom":[makeQuery(id+"F21.opExtrude","SWEPT_FACE",FACE,{"disambiguationData":[OSD([sQuery(id+"F20.wireOp",EDGE,"E47.2.0.7")])]}),makeQuery(id+"F23.opExtrude","SWEPT_FACE",FACE,{"disambiguationData":[OSD([sQuery(id+"F22.wireOp",EDGE,"E73")])]})]});
            var Q139;
            Q139=makeQuery(id+"F23.boolean.opBoolean","INTERSECT",EDGE,{"derivedFrom":[makeQuery(id+"F21.opExtrude","SWEPT_FACE",FACE,{"disambiguationData":[OSD([sQuery(id+"F20.wireOp",EDGE,"E47.2.0.7")])]}),makeQuery(id+"F23.opExtrude","SWEPT_FACE",FACE,{"disambiguationData":[OSD([sQuery(id+"F22.wireOp",EDGE,"E68")])]})]});
            var Q140;
            Q140=makeQuery(id+"F23.boolean.opBoolean","INTERSECT",EDGE,{"derivedFrom":[makeQuery(id+"F21.opExtrude","SWEPT_FACE",FACE,{"disambiguationData":[OSD([sQuery(id+"F20.wireOp",EDGE,"E47.2.0.7")])]}),makeQuery(id+"F23.opExtrude","SWEPT_FACE",FACE,{"disambiguationData":[OSD([sQuery(id+"F22.wireOp",EDGE,"E67")])]})]});
            var Q141;
            Q141=makeQuery(id+"F23.boolean.opBoolean","INTERSECT",EDGE,{"derivedFrom":[makeQuery(id+"F21.opExtrude","SWEPT_FACE",FACE,{"disambiguationData":[OSD([sQuery(id+"F20.wireOp",EDGE,"E47.2.0.7")])]}),makeQuery(id+"F23.opExtrude","SWEPT_FACE",FACE,{"disambiguationData":[OSD([sQuery(id+"F22.wireOp",EDGE,"E62")])]})]});
            var Q142;
            Q142=makeQuery(id+"F23.boolean.opBoolean","INTERSECT",EDGE,{"derivedFrom":[makeQuery(id+"F21.opExtrude","SWEPT_FACE",FACE,{"disambiguationData":[OSD([sQuery(id+"F20.wireOp",EDGE,"E47.2.0.7")])]}),makeQuery(id+"F23.opExtrude","SWEPT_FACE",FACE,{"disambiguationData":[OSD([sQuery(id+"F22.wireOp",EDGE,"E61")])]})]});
            var Q143;
            Q143=makeQuery(id+"F23.boolean.opBoolean","INTERSECT",EDGE,{"derivedFrom":[makeQuery(id+"F21.opExtrude","SWEPT_FACE",FACE,{"disambiguationData":[OSD([sQuery(id+"F20.wireOp",EDGE,"E47.2.0.7")])]}),makeQuery(id+"F23.opExtrude","SWEPT_FACE",FACE,{"disambiguationData":[OSD([sQuery(id+"F22.wireOp",EDGE,"E57")])]})]});
            var Q144;
            Q144=makeQuery(id+"F23.boolean.opBoolean","INTERSECT",EDGE,{"derivedFrom":[makeQuery(id+"F21.opExtrude","SWEPT_FACE",FACE,{"disambiguationData":[OSD([sQuery(id+"F20.wireOp",EDGE,"E47.2.0.7")])]}),makeQuery(id+"F23.opExtrude","SWEPT_FACE",FACE,{"disambiguationData":[OSD([sQuery(id+"F22.wireOp",EDGE,"E56")])]})]});
            var Q145;
            Q145=makeQuery(id+"F23.boolean.opBoolean","INTERSECT",EDGE,{"derivedFrom":[makeQuery(id+"F21.opExtrude","SWEPT_FACE",FACE,{"disambiguationData":[OSD([sQuery(id+"F20.wireOp",EDGE,"E47.2.0.7")])]}),makeQuery(id+"F23.opExtrude","SWEPT_FACE",FACE,{"disambiguationData":[OSD([sQuery(id+"F22.wireOp",EDGE,"E49")])]})]});
            var Q146;
            Q146=makeQuery(id+"F23.boolean.opBoolean","INTERSECT",EDGE,{"derivedFrom":[makeQuery(id+"F21.opExtrude","SWEPT_FACE",FACE,{"disambiguationData":[OSD([sQuery(id+"F20.wireOp",EDGE,"E47.2.0.7")])]}),makeQuery(id+"F23.opExtrude","SWEPT_FACE",FACE,{"disambiguationData":[OSD([sQuery(id+"F22.wireOp",EDGE,"E48")])]})]});
            var Q147;
            Q147=makeQuery(id+"F23.boolean.opBoolean","INTERSECT",EDGE,{"derivedFrom":[makeQuery(id+"F21.opExtrude","SWEPT_FACE",FACE,{"disambiguationData":[OSD([sQuery(id+"F20.wireOp",EDGE,"E47.1.0.7")])]}),makeQuery(id+"F23.opExtrude","SWEPT_FACE",FACE,{"disambiguationData":[OSD([sQuery(id+"F22.wireOp",EDGE,"E48")])]})]});
            var Q148;
            Q148=makeQuery(id+"F23.boolean.opBoolean","INTERSECT",EDGE,{"derivedFrom":[makeQuery(id+"F21.opExtrude","SWEPT_FACE",FACE,{"disambiguationData":[OSD([sQuery(id+"F20.wireOp",EDGE,"E47.1.0.7")])]}),makeQuery(id+"F23.opExtrude","SWEPT_FACE",FACE,{"disambiguationData":[OSD([sQuery(id+"F22.wireOp",EDGE,"E49")])]})]});
            var Q149;
            Q149=makeQuery(id+"F23.boolean.opBoolean","INTERSECT",EDGE,{"derivedFrom":[makeQuery(id+"F21.opExtrude","SWEPT_FACE",FACE,{"disambiguationData":[OSD([sQuery(id+"F20.wireOp",EDGE,"E47.1.0.7")])]}),makeQuery(id+"F23.opExtrude","SWEPT_FACE",FACE,{"disambiguationData":[OSD([sQuery(id+"F22.wireOp",EDGE,"E56")])]})]});
            var Q150;
            Q150=makeQuery(id+"F23.boolean.opBoolean","INTERSECT",EDGE,{"derivedFrom":[makeQuery(id+"F21.opExtrude","SWEPT_FACE",FACE,{"disambiguationData":[OSD([sQuery(id+"F20.wireOp",EDGE,"E47.1.0.7")])]}),makeQuery(id+"F23.opExtrude","SWEPT_FACE",FACE,{"disambiguationData":[OSD([sQuery(id+"F22.wireOp",EDGE,"E57")])]})]});
            var Q151;
            Q151=makeQuery(id+"F23.boolean.opBoolean","INTERSECT",EDGE,{"derivedFrom":[makeQuery(id+"F21.opExtrude","SWEPT_FACE",FACE,{"disambiguationData":[OSD([sQuery(id+"F20.wireOp",EDGE,"E47.1.0.7")])]}),makeQuery(id+"F23.opExtrude","SWEPT_FACE",FACE,{"disambiguationData":[OSD([sQuery(id+"F22.wireOp",EDGE,"E61")])]})]});
            var Q152;
            Q152=makeQuery(id+"F23.boolean.opBoolean","INTERSECT",EDGE,{"derivedFrom":[makeQuery(id+"F21.opExtrude","SWEPT_FACE",FACE,{"disambiguationData":[OSD([sQuery(id+"F20.wireOp",EDGE,"E47.1.0.7")])]}),makeQuery(id+"F23.opExtrude","SWEPT_FACE",FACE,{"disambiguationData":[OSD([sQuery(id+"F22.wireOp",EDGE,"E62")])]})]});
            var Q153;
            Q153=makeQuery(id+"F23.boolean.opBoolean","INTERSECT",EDGE,{"derivedFrom":[makeQuery(id+"F21.opExtrude","SWEPT_FACE",FACE,{"disambiguationData":[OSD([sQuery(id+"F20.wireOp",EDGE,"E47.1.0.7")])]}),makeQuery(id+"F23.opExtrude","SWEPT_FACE",FACE,{"disambiguationData":[OSD([sQuery(id+"F22.wireOp",EDGE,"E67")])]})]});
            var Q154;
            Q154=makeQuery(id+"F23.boolean.opBoolean","INTERSECT",EDGE,{"derivedFrom":[makeQuery(id+"F21.opExtrude","SWEPT_FACE",FACE,{"disambiguationData":[OSD([sQuery(id+"F20.wireOp",EDGE,"E47.1.0.7")])]}),makeQuery(id+"F23.opExtrude","SWEPT_FACE",FACE,{"disambiguationData":[OSD([sQuery(id+"F22.wireOp",EDGE,"E68")])]})]});
            var Q155;
            Q155=makeQuery(id+"F23.boolean.opBoolean","INTERSECT",EDGE,{"derivedFrom":[makeQuery(id+"F21.opExtrude","SWEPT_FACE",FACE,{"disambiguationData":[OSD([sQuery(id+"F20.wireOp",EDGE,"E47.1.0.7")])]}),makeQuery(id+"F23.opExtrude","SWEPT_FACE",FACE,{"disambiguationData":[OSD([sQuery(id+"F22.wireOp",EDGE,"E73")])]})]});
            var Q156;
            Q156=makeQuery(id+"F23.boolean.opBoolean","INTERSECT",EDGE,{"derivedFrom":[makeQuery(id+"F21.opExtrude","SWEPT_FACE",FACE,{"disambiguationData":[OSD([sQuery(id+"F20.wireOp",EDGE,"E47.1.0.7")])]}),makeQuery(id+"F23.opExtrude","SWEPT_FACE",FACE,{"disambiguationData":[OSD([sQuery(id+"F22.wireOp",EDGE,"E74")])]})]});
            var Q157;
            Q157=makeQuery(id+"F23.boolean.opBoolean","INTERSECT",EDGE,{"derivedFrom":[makeQuery(id+"F21.opExtrude","SWEPT_FACE",FACE,{"disambiguationData":[OSD([sQuery(id+"F20.wireOp",EDGE,"E39")])]}),makeQuery(id+"F23.opExtrude","SWEPT_FACE",FACE,{"disambiguationData":[OSD([sQuery(id+"F22.wireOp",EDGE,"E74")])]})]});
            var Q158;
            Q158=makeQuery(id+"F23.boolean.opBoolean","INTERSECT",EDGE,{"derivedFrom":[makeQuery(id+"F21.opExtrude","SWEPT_FACE",FACE,{"disambiguationData":[OSD([sQuery(id+"F20.wireOp",EDGE,"E39")])]}),makeQuery(id+"F23.opExtrude","SWEPT_FACE",FACE,{"disambiguationData":[OSD([sQuery(id+"F22.wireOp",EDGE,"E73")])]})]});
            var Q159;
            Q159=makeQuery(id+"F23.boolean.opBoolean","INTERSECT",EDGE,{"derivedFrom":[makeQuery(id+"F21.opExtrude","SWEPT_FACE",FACE,{"disambiguationData":[OSD([sQuery(id+"F20.wireOp",EDGE,"E39")])]}),makeQuery(id+"F23.opExtrude","SWEPT_FACE",FACE,{"disambiguationData":[OSD([sQuery(id+"F22.wireOp",EDGE,"E68")])]})]});
            var Q160;
            Q160=makeQuery(id+"F23.boolean.opBoolean","INTERSECT",EDGE,{"derivedFrom":[makeQuery(id+"F21.opExtrude","SWEPT_FACE",FACE,{"disambiguationData":[OSD([sQuery(id+"F20.wireOp",EDGE,"E39")])]}),makeQuery(id+"F23.opExtrude","SWEPT_FACE",FACE,{"disambiguationData":[OSD([sQuery(id+"F22.wireOp",EDGE,"E67")])]})]});
            var Q161;
            Q161=makeQuery(id+"F23.boolean.opBoolean","INTERSECT",EDGE,{"derivedFrom":[makeQuery(id+"F21.opExtrude","SWEPT_FACE",FACE,{"disambiguationData":[OSD([sQuery(id+"F20.wireOp",EDGE,"E39")])]}),makeQuery(id+"F23.opExtrude","SWEPT_FACE",FACE,{"disambiguationData":[OSD([sQuery(id+"F22.wireOp",EDGE,"E62")])]})]});
            var Q162;
            Q162=makeQuery(id+"F23.boolean.opBoolean","INTERSECT",EDGE,{"derivedFrom":[makeQuery(id+"F21.opExtrude","SWEPT_FACE",FACE,{"disambiguationData":[OSD([sQuery(id+"F20.wireOp",EDGE,"E39")])]}),makeQuery(id+"F23.opExtrude","SWEPT_FACE",FACE,{"disambiguationData":[OSD([sQuery(id+"F22.wireOp",EDGE,"E61")])]})]});
            var Q163;
            Q163=makeQuery(id+"F23.boolean.opBoolean","INTERSECT",EDGE,{"derivedFrom":[makeQuery(id+"F21.opExtrude","SWEPT_FACE",FACE,{"disambiguationData":[OSD([sQuery(id+"F20.wireOp",EDGE,"E39")])]}),makeQuery(id+"F23.opExtrude","SWEPT_FACE",FACE,{"disambiguationData":[OSD([sQuery(id+"F22.wireOp",EDGE,"E57")])]})]});
            var Q164;
            Q164=makeQuery(id+"F23.boolean.opBoolean","INTERSECT",EDGE,{"derivedFrom":[makeQuery(id+"F21.opExtrude","SWEPT_FACE",FACE,{"disambiguationData":[OSD([sQuery(id+"F20.wireOp",EDGE,"E39")])]}),makeQuery(id+"F23.opExtrude","SWEPT_FACE",FACE,{"disambiguationData":[OSD([sQuery(id+"F22.wireOp",EDGE,"E56")])]})]});
            var Q165;
            Q165=makeQuery(id+"F23.boolean.opBoolean","INTERSECT",EDGE,{"derivedFrom":[makeQuery(id+"F21.opExtrude","SWEPT_FACE",FACE,{"disambiguationData":[OSD([sQuery(id+"F20.wireOp",EDGE,"E39")])]}),makeQuery(id+"F23.opExtrude","SWEPT_FACE",FACE,{"disambiguationData":[OSD([sQuery(id+"F22.wireOp",EDGE,"E49")])]})]});
            var Q166;
            Q166=makeQuery(id+"F23.boolean.opBoolean","INTERSECT",EDGE,{"derivedFrom":[makeQuery(id+"F21.opExtrude","SWEPT_FACE",FACE,{"disambiguationData":[OSD([sQuery(id+"F20.wireOp",EDGE,"E39")])]}),makeQuery(id+"F23.opExtrude","SWEPT_FACE",FACE,{"disambiguationData":[OSD([sQuery(id+"F22.wireOp",EDGE,"E48")])]})]});
            var Q167;
            Q167=makeQuery(id+"F23.boolean.opBoolean","INTERSECT",EDGE,{"derivedFrom":[makeQuery(id+"F21.opExtrude","SWEPT_FACE",FACE,{"disambiguationData":[OSD([sQuery(id+"F20.wireOp",EDGE,"E38")])]}),makeQuery(id+"F23.opExtrude","SWEPT_FACE",FACE,{"disambiguationData":[OSD([sQuery(id+"F22.wireOp",EDGE,"E74")])]})]});
            var Q168;
            Q168=makeQuery(id+"F23.boolean.opBoolean","INTERSECT",EDGE,{"derivedFrom":[makeQuery(id+"F21.opExtrude","SWEPT_FACE",FACE,{"disambiguationData":[OSD([sQuery(id+"F20.wireOp",EDGE,"E38")])]}),makeQuery(id+"F23.opExtrude","SWEPT_FACE",FACE,{"disambiguationData":[OSD([sQuery(id+"F22.wireOp",EDGE,"E73")])]})]});
            var Q169;
            Q169=makeQuery(id+"F23.boolean.opBoolean","INTERSECT",EDGE,{"derivedFrom":[makeQuery(id+"F21.opExtrude","SWEPT_FACE",FACE,{"disambiguationData":[OSD([sQuery(id+"F20.wireOp",EDGE,"E38")])]}),makeQuery(id+"F23.opExtrude","SWEPT_FACE",FACE,{"disambiguationData":[OSD([sQuery(id+"F22.wireOp",EDGE,"E68")])]})]});
            var Q170;
            Q170=makeQuery(id+"F23.boolean.opBoolean","INTERSECT",EDGE,{"derivedFrom":[makeQuery(id+"F21.opExtrude","SWEPT_FACE",FACE,{"disambiguationData":[OSD([sQuery(id+"F20.wireOp",EDGE,"E38")])]}),makeQuery(id+"F23.opExtrude","SWEPT_FACE",FACE,{"disambiguationData":[OSD([sQuery(id+"F22.wireOp",EDGE,"E67")])]})]});
            var Q171;
            Q171=makeQuery(id+"F23.boolean.opBoolean","INTERSECT",EDGE,{"derivedFrom":[makeQuery(id+"F21.opExtrude","SWEPT_FACE",FACE,{"disambiguationData":[OSD([sQuery(id+"F20.wireOp",EDGE,"E38")])]}),makeQuery(id+"F23.opExtrude","SWEPT_FACE",FACE,{"disambiguationData":[OSD([sQuery(id+"F22.wireOp",EDGE,"E62")])]})]});
            var Q172;
            Q172=makeQuery(id+"F23.boolean.opBoolean","INTERSECT",EDGE,{"derivedFrom":[makeQuery(id+"F21.opExtrude","SWEPT_FACE",FACE,{"disambiguationData":[OSD([sQuery(id+"F20.wireOp",EDGE,"E38")])]}),makeQuery(id+"F23.opExtrude","SWEPT_FACE",FACE,{"disambiguationData":[OSD([sQuery(id+"F22.wireOp",EDGE,"E61")])]})]});
            var Q173;
            Q173=makeQuery(id+"F23.boolean.opBoolean","INTERSECT",EDGE,{"derivedFrom":[makeQuery(id+"F21.opExtrude","SWEPT_FACE",FACE,{"disambiguationData":[OSD([sQuery(id+"F20.wireOp",EDGE,"E38")])]}),makeQuery(id+"F23.opExtrude","SWEPT_FACE",FACE,{"disambiguationData":[OSD([sQuery(id+"F22.wireOp",EDGE,"E57")])]})]});
            var Q174;
            Q174=makeQuery(id+"F23.boolean.opBoolean","INTERSECT",EDGE,{"derivedFrom":[makeQuery(id+"F21.opExtrude","SWEPT_FACE",FACE,{"disambiguationData":[OSD([sQuery(id+"F20.wireOp",EDGE,"E38")])]}),makeQuery(id+"F23.opExtrude","SWEPT_FACE",FACE,{"disambiguationData":[OSD([sQuery(id+"F22.wireOp",EDGE,"E56")])]})]});
            var Q175;
            Q175=makeQuery(id+"F23.boolean.opBoolean","INTERSECT",EDGE,{"derivedFrom":[makeQuery(id+"F21.opExtrude","SWEPT_FACE",FACE,{"disambiguationData":[OSD([sQuery(id+"F20.wireOp",EDGE,"E38")])]}),makeQuery(id+"F23.opExtrude","SWEPT_FACE",FACE,{"disambiguationData":[OSD([sQuery(id+"F22.wireOp",EDGE,"E49")])]})]});
            var Q176;
            Q176=makeQuery(id+"F23.boolean.opBoolean","INTERSECT",EDGE,{"derivedFrom":[makeQuery(id+"F21.opExtrude","SWEPT_FACE",FACE,{"disambiguationData":[OSD([sQuery(id+"F20.wireOp",EDGE,"E38")])]}),makeQuery(id+"F23.opExtrude","SWEPT_FACE",FACE,{"disambiguationData":[OSD([sQuery(id+"F22.wireOp",EDGE,"E48")])]})]});
            var Q177;
            Q177=makeQuery(id+"F23.boolean.opBoolean","INTERSECT",EDGE,{"derivedFrom":[makeQuery(id+"F21.opExtrude","SWEPT_FACE",FACE,{"disambiguationData":[OSD([sQuery(id+"F20.wireOp",EDGE,"E47.1.0.2")])]}),makeQuery(id+"F23.opExtrude","SWEPT_FACE",FACE,{"disambiguationData":[OSD([sQuery(id+"F22.wireOp",EDGE,"E48")])]})]});
            var Q178;
            Q178=makeQuery(id+"F23.boolean.opBoolean","INTERSECT",EDGE,{"derivedFrom":[makeQuery(id+"F21.opExtrude","SWEPT_FACE",FACE,{"disambiguationData":[OSD([sQuery(id+"F20.wireOp",EDGE,"E47.1.0.2")])]}),makeQuery(id+"F23.opExtrude","SWEPT_FACE",FACE,{"disambiguationData":[OSD([sQuery(id+"F22.wireOp",EDGE,"E49")])]})]});
            var Q179;
            Q179=makeQuery(id+"F23.boolean.opBoolean","INTERSECT",EDGE,{"derivedFrom":[makeQuery(id+"F21.opExtrude","SWEPT_FACE",FACE,{"disambiguationData":[OSD([sQuery(id+"F20.wireOp",EDGE,"E47.1.0.2")])]}),makeQuery(id+"F23.opExtrude","SWEPT_FACE",FACE,{"disambiguationData":[OSD([sQuery(id+"F22.wireOp",EDGE,"E56")])]})]});
            var Q180;
            Q180=makeQuery(id+"F23.boolean.opBoolean","INTERSECT",EDGE,{"derivedFrom":[makeQuery(id+"F21.opExtrude","SWEPT_FACE",FACE,{"disambiguationData":[OSD([sQuery(id+"F20.wireOp",EDGE,"E47.1.0.2")])]}),makeQuery(id+"F23.opExtrude","SWEPT_FACE",FACE,{"disambiguationData":[OSD([sQuery(id+"F22.wireOp",EDGE,"E57")])]})]});
            var Q181;
            Q181=makeQuery(id+"F23.boolean.opBoolean","INTERSECT",EDGE,{"derivedFrom":[makeQuery(id+"F21.opExtrude","SWEPT_FACE",FACE,{"disambiguationData":[OSD([sQuery(id+"F20.wireOp",EDGE,"E47.1.0.2")])]}),makeQuery(id+"F23.opExtrude","SWEPT_FACE",FACE,{"disambiguationData":[OSD([sQuery(id+"F22.wireOp",EDGE,"E61")])]})]});
            var Q182;
            Q182=makeQuery(id+"F23.boolean.opBoolean","INTERSECT",EDGE,{"derivedFrom":[makeQuery(id+"F21.opExtrude","SWEPT_FACE",FACE,{"disambiguationData":[OSD([sQuery(id+"F20.wireOp",EDGE,"E47.1.0.2")])]}),makeQuery(id+"F23.opExtrude","SWEPT_FACE",FACE,{"disambiguationData":[OSD([sQuery(id+"F22.wireOp",EDGE,"E62")])]})]});
            var Q183;
            Q183=makeQuery(id+"F23.boolean.opBoolean","INTERSECT",EDGE,{"derivedFrom":[makeQuery(id+"F21.opExtrude","SWEPT_FACE",FACE,{"disambiguationData":[OSD([sQuery(id+"F20.wireOp",EDGE,"E47.1.0.2")])]}),makeQuery(id+"F23.opExtrude","SWEPT_FACE",FACE,{"disambiguationData":[OSD([sQuery(id+"F22.wireOp",EDGE,"E67")])]})]});
            var Q184;
            Q184=makeQuery(id+"F23.boolean.opBoolean","INTERSECT",EDGE,{"derivedFrom":[makeQuery(id+"F21.opExtrude","SWEPT_FACE",FACE,{"disambiguationData":[OSD([sQuery(id+"F20.wireOp",EDGE,"E47.1.0.2")])]}),makeQuery(id+"F23.opExtrude","SWEPT_FACE",FACE,{"disambiguationData":[OSD([sQuery(id+"F22.wireOp",EDGE,"E68")])]})]});
            var Q185;
            Q185=makeQuery(id+"F23.boolean.opBoolean","INTERSECT",EDGE,{"derivedFrom":[makeQuery(id+"F21.opExtrude","SWEPT_FACE",FACE,{"disambiguationData":[OSD([sQuery(id+"F20.wireOp",EDGE,"E47.1.0.2")])]}),makeQuery(id+"F23.opExtrude","SWEPT_FACE",FACE,{"disambiguationData":[OSD([sQuery(id+"F22.wireOp",EDGE,"E73")])]})]});
            var Q186;
            Q186=makeQuery(id+"F23.boolean.opBoolean","INTERSECT",EDGE,{"derivedFrom":[makeQuery(id+"F21.opExtrude","SWEPT_FACE",FACE,{"disambiguationData":[OSD([sQuery(id+"F20.wireOp",EDGE,"E47.1.0.2")])]}),makeQuery(id+"F23.opExtrude","SWEPT_FACE",FACE,{"disambiguationData":[OSD([sQuery(id+"F22.wireOp",EDGE,"E74")])]})]});
            var Q187;
            Q187=makeQuery(id+"F23.boolean.opBoolean","INTERSECT",EDGE,{"derivedFrom":[makeQuery(id+"F21.opExtrude","SWEPT_FACE",FACE,{"disambiguationData":[OSD([sQuery(id+"F20.wireOp",EDGE,"E47.2.0.2")])]}),makeQuery(id+"F23.opExtrude","SWEPT_FACE",FACE,{"disambiguationData":[OSD([sQuery(id+"F22.wireOp",EDGE,"E74")])]})]});
            var Q188;
            Q188=makeQuery(id+"F23.boolean.opBoolean","INTERSECT",EDGE,{"derivedFrom":[makeQuery(id+"F21.opExtrude","SWEPT_FACE",FACE,{"disambiguationData":[OSD([sQuery(id+"F20.wireOp",EDGE,"E47.2.0.2")])]}),makeQuery(id+"F23.opExtrude","SWEPT_FACE",FACE,{"disambiguationData":[OSD([sQuery(id+"F22.wireOp",EDGE,"E73")])]})]});
            var Q189;
            Q189=makeQuery(id+"F23.boolean.opBoolean","INTERSECT",EDGE,{"derivedFrom":[makeQuery(id+"F21.opExtrude","SWEPT_FACE",FACE,{"disambiguationData":[OSD([sQuery(id+"F20.wireOp",EDGE,"E47.2.0.2")])]}),makeQuery(id+"F23.opExtrude","SWEPT_FACE",FACE,{"disambiguationData":[OSD([sQuery(id+"F22.wireOp",EDGE,"E68")])]})]});
            var Q190;
            Q190=makeQuery(id+"F23.boolean.opBoolean","INTERSECT",EDGE,{"derivedFrom":[makeQuery(id+"F21.opExtrude","SWEPT_FACE",FACE,{"disambiguationData":[OSD([sQuery(id+"F20.wireOp",EDGE,"E47.2.0.2")])]}),makeQuery(id+"F23.opExtrude","SWEPT_FACE",FACE,{"disambiguationData":[OSD([sQuery(id+"F22.wireOp",EDGE,"E67")])]})]});
            var Q191;
            Q191=makeQuery(id+"F23.boolean.opBoolean","INTERSECT",EDGE,{"derivedFrom":[makeQuery(id+"F21.opExtrude","SWEPT_FACE",FACE,{"disambiguationData":[OSD([sQuery(id+"F20.wireOp",EDGE,"E47.2.0.2")])]}),makeQuery(id+"F23.opExtrude","SWEPT_FACE",FACE,{"disambiguationData":[OSD([sQuery(id+"F22.wireOp",EDGE,"E62")])]})]});
            var Q192;
            Q192=makeQuery(id+"F23.boolean.opBoolean","INTERSECT",EDGE,{"derivedFrom":[makeQuery(id+"F21.opExtrude","SWEPT_FACE",FACE,{"disambiguationData":[OSD([sQuery(id+"F20.wireOp",EDGE,"E47.2.0.2")])]}),makeQuery(id+"F23.opExtrude","SWEPT_FACE",FACE,{"disambiguationData":[OSD([sQuery(id+"F22.wireOp",EDGE,"E61")])]})]});
            var Q193;
            Q193=makeQuery(id+"F23.boolean.opBoolean","INTERSECT",EDGE,{"derivedFrom":[makeQuery(id+"F21.opExtrude","SWEPT_FACE",FACE,{"disambiguationData":[OSD([sQuery(id+"F20.wireOp",EDGE,"E47.2.0.2")])]}),makeQuery(id+"F23.opExtrude","SWEPT_FACE",FACE,{"disambiguationData":[OSD([sQuery(id+"F22.wireOp",EDGE,"E57")])]})]});
            var Q194;
            Q194=makeQuery(id+"F23.boolean.opBoolean","INTERSECT",EDGE,{"derivedFrom":[makeQuery(id+"F21.opExtrude","SWEPT_FACE",FACE,{"disambiguationData":[OSD([sQuery(id+"F20.wireOp",EDGE,"E47.2.0.2")])]}),makeQuery(id+"F23.opExtrude","SWEPT_FACE",FACE,{"disambiguationData":[OSD([sQuery(id+"F22.wireOp",EDGE,"E56")])]})]});
            var Q195;
            Q195=makeQuery(id+"F23.boolean.opBoolean","INTERSECT",EDGE,{"derivedFrom":[makeQuery(id+"F21.opExtrude","SWEPT_FACE",FACE,{"disambiguationData":[OSD([sQuery(id+"F20.wireOp",EDGE,"E47.2.0.2")])]}),makeQuery(id+"F23.opExtrude","SWEPT_FACE",FACE,{"disambiguationData":[OSD([sQuery(id+"F22.wireOp",EDGE,"E49")])]})]});
            var Q196;
            Q196=makeQuery(id+"F23.boolean.opBoolean","INTERSECT",EDGE,{"derivedFrom":[makeQuery(id+"F21.opExtrude","SWEPT_FACE",FACE,{"disambiguationData":[OSD([sQuery(id+"F20.wireOp",EDGE,"E47.2.0.2")])]}),makeQuery(id+"F23.opExtrude","SWEPT_FACE",FACE,{"disambiguationData":[OSD([sQuery(id+"F22.wireOp",EDGE,"E48")])]})]});
            var Q197;
            Q197=makeQuery(id+"F23.boolean.opBoolean","INTERSECT",EDGE,{"derivedFrom":[makeQuery(id+"F21.opExtrude","SWEPT_FACE",FACE,{"disambiguationData":[OSD([sQuery(id+"F20.wireOp",EDGE,"E47.3.0.2")])]}),makeQuery(id+"F23.opExtrude","SWEPT_FACE",FACE,{"disambiguationData":[OSD([sQuery(id+"F22.wireOp",EDGE,"E48")])]})]});
            var Q198;
            Q198=makeQuery(id+"F23.boolean.opBoolean","INTERSECT",EDGE,{"derivedFrom":[makeQuery(id+"F21.opExtrude","SWEPT_FACE",FACE,{"disambiguationData":[OSD([sQuery(id+"F20.wireOp",EDGE,"E47.3.0.2")])]}),makeQuery(id+"F23.opExtrude","SWEPT_FACE",FACE,{"disambiguationData":[OSD([sQuery(id+"F22.wireOp",EDGE,"E49")])]})]});
            var Q199;
            Q199=makeQuery(id+"F23.boolean.opBoolean","INTERSECT",EDGE,{"derivedFrom":[makeQuery(id+"F21.opExtrude","SWEPT_FACE",FACE,{"disambiguationData":[OSD([sQuery(id+"F20.wireOp",EDGE,"E47.3.0.2")])]}),makeQuery(id+"F23.opExtrude","SWEPT_FACE",FACE,{"disambiguationData":[OSD([sQuery(id+"F22.wireOp",EDGE,"E56")])]})]});
            var Q200;
            Q200=makeQuery(id+"F23.boolean.opBoolean","INTERSECT",EDGE,{"derivedFrom":[makeQuery(id+"F21.opExtrude","SWEPT_FACE",FACE,{"disambiguationData":[OSD([sQuery(id+"F20.wireOp",EDGE,"E47.3.0.2")])]}),makeQuery(id+"F23.opExtrude","SWEPT_FACE",FACE,{"disambiguationData":[OSD([sQuery(id+"F22.wireOp",EDGE,"E57")])]})]});
            var Q201;
            Q201=makeQuery(id+"F23.boolean.opBoolean","INTERSECT",EDGE,{"derivedFrom":[makeQuery(id+"F21.opExtrude","SWEPT_FACE",FACE,{"disambiguationData":[OSD([sQuery(id+"F20.wireOp",EDGE,"E47.3.0.2")])]}),makeQuery(id+"F23.opExtrude","SWEPT_FACE",FACE,{"disambiguationData":[OSD([sQuery(id+"F22.wireOp",EDGE,"E61")])]})]});
            var Q202;
            Q202=makeQuery(id+"F23.boolean.opBoolean","INTERSECT",EDGE,{"derivedFrom":[makeQuery(id+"F21.opExtrude","SWEPT_FACE",FACE,{"disambiguationData":[OSD([sQuery(id+"F20.wireOp",EDGE,"E47.3.0.2")])]}),makeQuery(id+"F23.opExtrude","SWEPT_FACE",FACE,{"disambiguationData":[OSD([sQuery(id+"F22.wireOp",EDGE,"E62")])]})]});
            var Q203;
            Q203=makeQuery(id+"F23.boolean.opBoolean","INTERSECT",EDGE,{"derivedFrom":[makeQuery(id+"F21.opExtrude","SWEPT_FACE",FACE,{"disambiguationData":[OSD([sQuery(id+"F20.wireOp",EDGE,"E47.3.0.2")])]}),makeQuery(id+"F23.opExtrude","SWEPT_FACE",FACE,{"disambiguationData":[OSD([sQuery(id+"F22.wireOp",EDGE,"E67")])]})]});
            var Q204;
            Q204=makeQuery(id+"F23.boolean.opBoolean","INTERSECT",EDGE,{"derivedFrom":[makeQuery(id+"F21.opExtrude","SWEPT_FACE",FACE,{"disambiguationData":[OSD([sQuery(id+"F20.wireOp",EDGE,"E47.3.0.2")])]}),makeQuery(id+"F23.opExtrude","SWEPT_FACE",FACE,{"disambiguationData":[OSD([sQuery(id+"F22.wireOp",EDGE,"E68")])]})]});
            var Q205;
            Q205=makeQuery(id+"F23.boolean.opBoolean","INTERSECT",EDGE,{"derivedFrom":[makeQuery(id+"F21.opExtrude","SWEPT_FACE",FACE,{"disambiguationData":[OSD([sQuery(id+"F20.wireOp",EDGE,"E47.3.0.2")])]}),makeQuery(id+"F23.opExtrude","SWEPT_FACE",FACE,{"disambiguationData":[OSD([sQuery(id+"F22.wireOp",EDGE,"E73")])]})]});
            var Q206;
            Q206=makeQuery(id+"F23.boolean.opBoolean","INTERSECT",EDGE,{"derivedFrom":[makeQuery(id+"F21.opExtrude","SWEPT_FACE",FACE,{"disambiguationData":[OSD([sQuery(id+"F20.wireOp",EDGE,"E47.3.0.2")])]}),makeQuery(id+"F23.opExtrude","SWEPT_FACE",FACE,{"disambiguationData":[OSD([sQuery(id+"F22.wireOp",EDGE,"E74")])]})]});
            var Q207;
            Q207=makeQuery(id+"F23.boolean.opBoolean","INTERSECT",EDGE,{"derivedFrom":[makeQuery(id+"F21.opExtrude","SWEPT_FACE",FACE,{"disambiguationData":[OSD([sQuery(id+"F20.wireOp",EDGE,"E47.4.0.2")])]}),makeQuery(id+"F23.opExtrude","SWEPT_FACE",FACE,{"disambiguationData":[OSD([sQuery(id+"F22.wireOp",EDGE,"E48")])]})]});
            var Q208;
            Q208=makeQuery(id+"F23.boolean.opBoolean","INTERSECT",EDGE,{"derivedFrom":[makeQuery(id+"F21.opExtrude","SWEPT_FACE",FACE,{"disambiguationData":[OSD([sQuery(id+"F20.wireOp",EDGE,"E47.4.0.2")])]}),makeQuery(id+"F23.opExtrude","SWEPT_FACE",FACE,{"disambiguationData":[OSD([sQuery(id+"F22.wireOp",EDGE,"E49")])]})]});
            var Q209;
            Q209=makeQuery(id+"F23.boolean.opBoolean","INTERSECT",EDGE,{"derivedFrom":[makeQuery(id+"F21.opExtrude","SWEPT_FACE",FACE,{"disambiguationData":[OSD([sQuery(id+"F20.wireOp",EDGE,"E47.4.0.2")])]}),makeQuery(id+"F23.opExtrude","SWEPT_FACE",FACE,{"disambiguationData":[OSD([sQuery(id+"F22.wireOp",EDGE,"E56")])]})]});
            var Q210;
            Q210=makeQuery(id+"F23.boolean.opBoolean","INTERSECT",EDGE,{"derivedFrom":[makeQuery(id+"F21.opExtrude","SWEPT_FACE",FACE,{"disambiguationData":[OSD([sQuery(id+"F20.wireOp",EDGE,"E47.4.0.2")])]}),makeQuery(id+"F23.opExtrude","SWEPT_FACE",FACE,{"disambiguationData":[OSD([sQuery(id+"F22.wireOp",EDGE,"E57")])]})]});
            var Q211;
            Q211=makeQuery(id+"F23.boolean.opBoolean","INTERSECT",EDGE,{"derivedFrom":[makeQuery(id+"F21.opExtrude","SWEPT_FACE",FACE,{"disambiguationData":[OSD([sQuery(id+"F20.wireOp",EDGE,"E47.4.0.2")])]}),makeQuery(id+"F23.opExtrude","SWEPT_FACE",FACE,{"disambiguationData":[OSD([sQuery(id+"F22.wireOp",EDGE,"E61")])]})]});
            var Q212;
            Q212=makeQuery(id+"F23.boolean.opBoolean","INTERSECT",EDGE,{"derivedFrom":[makeQuery(id+"F21.opExtrude","SWEPT_FACE",FACE,{"disambiguationData":[OSD([sQuery(id+"F20.wireOp",EDGE,"E47.4.0.2")])]}),makeQuery(id+"F23.opExtrude","SWEPT_FACE",FACE,{"disambiguationData":[OSD([sQuery(id+"F22.wireOp",EDGE,"E62")])]})]});
            var Q213;
            Q213=makeQuery(id+"F23.boolean.opBoolean","INTERSECT",EDGE,{"derivedFrom":[makeQuery(id+"F21.opExtrude","SWEPT_FACE",FACE,{"disambiguationData":[OSD([sQuery(id+"F20.wireOp",EDGE,"E47.4.0.2")])]}),makeQuery(id+"F23.opExtrude","SWEPT_FACE",FACE,{"disambiguationData":[OSD([sQuery(id+"F22.wireOp",EDGE,"E67")])]})]});
            var Q214;
            Q214=makeQuery(id+"F23.boolean.opBoolean","INTERSECT",EDGE,{"derivedFrom":[makeQuery(id+"F21.opExtrude","SWEPT_FACE",FACE,{"disambiguationData":[OSD([sQuery(id+"F20.wireOp",EDGE,"E47.4.0.2")])]}),makeQuery(id+"F23.opExtrude","SWEPT_FACE",FACE,{"disambiguationData":[OSD([sQuery(id+"F22.wireOp",EDGE,"E68")])]})]});
            var Q215;
            Q215=makeQuery(id+"F23.boolean.opBoolean","INTERSECT",EDGE,{"derivedFrom":[makeQuery(id+"F21.opExtrude","SWEPT_FACE",FACE,{"disambiguationData":[OSD([sQuery(id+"F20.wireOp",EDGE,"E47.4.0.2")])]}),makeQuery(id+"F23.opExtrude","SWEPT_FACE",FACE,{"disambiguationData":[OSD([sQuery(id+"F22.wireOp",EDGE,"E73")])]})]});
            var Q216;
            Q216=makeQuery(id+"F23.boolean.opBoolean","INTERSECT",EDGE,{"derivedFrom":[makeQuery(id+"F21.opExtrude","SWEPT_FACE",FACE,{"disambiguationData":[OSD([sQuery(id+"F20.wireOp",EDGE,"E47.4.0.2")])]}),makeQuery(id+"F23.opExtrude","SWEPT_FACE",FACE,{"disambiguationData":[OSD([sQuery(id+"F22.wireOp",EDGE,"E74")])]})]});
            var Q217;
            Q217=makeQuery(id+"F23.boolean.opBoolean","INTERSECT",EDGE,{"derivedFrom":[makeQuery(id+"F21.opExtrude","SWEPT_FACE",FACE,{"disambiguationData":[OSD([sQuery(id+"F20.wireOp",EDGE,"E47.5.0.2")])]}),makeQuery(id+"F23.opExtrude","SWEPT_FACE",FACE,{"disambiguationData":[OSD([sQuery(id+"F22.wireOp",EDGE,"E74")])]})]});
            var Q218;
            Q218=makeQuery(id+"F23.boolean.opBoolean","INTERSECT",EDGE,{"derivedFrom":[makeQuery(id+"F21.opExtrude","SWEPT_FACE",FACE,{"disambiguationData":[OSD([sQuery(id+"F20.wireOp",EDGE,"E47.5.0.2")])]}),makeQuery(id+"F23.opExtrude","SWEPT_FACE",FACE,{"disambiguationData":[OSD([sQuery(id+"F22.wireOp",EDGE,"E73")])]})]});
            var Q219;
            Q219=makeQuery(id+"F23.boolean.opBoolean","INTERSECT",EDGE,{"derivedFrom":[makeQuery(id+"F21.opExtrude","SWEPT_FACE",FACE,{"disambiguationData":[OSD([sQuery(id+"F20.wireOp",EDGE,"E47.5.0.2")])]}),makeQuery(id+"F23.opExtrude","SWEPT_FACE",FACE,{"disambiguationData":[OSD([sQuery(id+"F22.wireOp",EDGE,"E68")])]})]});
            var Q220;
            Q220=makeQuery(id+"F23.boolean.opBoolean","INTERSECT",EDGE,{"derivedFrom":[makeQuery(id+"F21.opExtrude","SWEPT_FACE",FACE,{"disambiguationData":[OSD([sQuery(id+"F20.wireOp",EDGE,"E47.5.0.2")])]}),makeQuery(id+"F23.opExtrude","SWEPT_FACE",FACE,{"disambiguationData":[OSD([sQuery(id+"F22.wireOp",EDGE,"E67")])]})]});
            var Q221;
            Q221=makeQuery(id+"F23.boolean.opBoolean","INTERSECT",EDGE,{"derivedFrom":[makeQuery(id+"F21.opExtrude","SWEPT_FACE",FACE,{"disambiguationData":[OSD([sQuery(id+"F20.wireOp",EDGE,"E47.5.0.2")])]}),makeQuery(id+"F23.opExtrude","SWEPT_FACE",FACE,{"disambiguationData":[OSD([sQuery(id+"F22.wireOp",EDGE,"E62")])]})]});
            var Q222;
            Q222=makeQuery(id+"F23.boolean.opBoolean","INTERSECT",EDGE,{"derivedFrom":[makeQuery(id+"F21.opExtrude","SWEPT_FACE",FACE,{"disambiguationData":[OSD([sQuery(id+"F20.wireOp",EDGE,"E47.5.0.2")])]}),makeQuery(id+"F23.opExtrude","SWEPT_FACE",FACE,{"disambiguationData":[OSD([sQuery(id+"F22.wireOp",EDGE,"E61")])]})]});
            var Q223;
            Q223=makeQuery(id+"F23.boolean.opBoolean","INTERSECT",EDGE,{"derivedFrom":[makeQuery(id+"F21.opExtrude","SWEPT_FACE",FACE,{"disambiguationData":[OSD([sQuery(id+"F20.wireOp",EDGE,"E47.5.0.2")])]}),makeQuery(id+"F23.opExtrude","SWEPT_FACE",FACE,{"disambiguationData":[OSD([sQuery(id+"F22.wireOp",EDGE,"E57")])]})]});
            var Q224;
            Q224=makeQuery(id+"F23.boolean.opBoolean","INTERSECT",EDGE,{"derivedFrom":[makeQuery(id+"F21.opExtrude","SWEPT_FACE",FACE,{"disambiguationData":[OSD([sQuery(id+"F20.wireOp",EDGE,"E47.5.0.2")])]}),makeQuery(id+"F23.opExtrude","SWEPT_FACE",FACE,{"disambiguationData":[OSD([sQuery(id+"F22.wireOp",EDGE,"E56")])]})]});
            var Q225;
            Q225=makeQuery(id+"F23.boolean.opBoolean","INTERSECT",EDGE,{"derivedFrom":[makeQuery(id+"F21.opExtrude","SWEPT_FACE",FACE,{"disambiguationData":[OSD([sQuery(id+"F20.wireOp",EDGE,"E47.5.0.2")])]}),makeQuery(id+"F23.opExtrude","SWEPT_FACE",FACE,{"disambiguationData":[OSD([sQuery(id+"F22.wireOp",EDGE,"E49")])]})]});
            var Q226;
            Q226=makeQuery(id+"F23.boolean.opBoolean","INTERSECT",EDGE,{"derivedFrom":[makeQuery(id+"F21.opExtrude","SWEPT_FACE",FACE,{"disambiguationData":[OSD([sQuery(id+"F20.wireOp",EDGE,"E47.5.0.2")])]}),makeQuery(id+"F23.opExtrude","SWEPT_FACE",FACE,{"disambiguationData":[OSD([sQuery(id+"F22.wireOp",EDGE,"E48")])]})]});
            var Q227;
            Q227=makeQuery(id+"F23.boolean.opBoolean","INTERSECT",EDGE,{"derivedFrom":[makeQuery(id+"F21.opExtrude","SWEPT_FACE",FACE,{"disambiguationData":[OSD([sQuery(id+"F20.wireOp",EDGE,"E47.6.0.2")])]}),makeQuery(id+"F23.opExtrude","SWEPT_FACE",FACE,{"disambiguationData":[OSD([sQuery(id+"F22.wireOp",EDGE,"E48")])]})]});
            var Q228;
            Q228=makeQuery(id+"F23.boolean.opBoolean","INTERSECT",EDGE,{"derivedFrom":[makeQuery(id+"F21.opExtrude","SWEPT_FACE",FACE,{"disambiguationData":[OSD([sQuery(id+"F20.wireOp",EDGE,"E47.6.0.2")])]}),makeQuery(id+"F23.opExtrude","SWEPT_FACE",FACE,{"disambiguationData":[OSD([sQuery(id+"F22.wireOp",EDGE,"E49")])]})]});
            var Q229;
            Q229=makeQuery(id+"F23.boolean.opBoolean","INTERSECT",EDGE,{"derivedFrom":[makeQuery(id+"F21.opExtrude","SWEPT_FACE",FACE,{"disambiguationData":[OSD([sQuery(id+"F20.wireOp",EDGE,"E47.6.0.2")])]}),makeQuery(id+"F23.opExtrude","SWEPT_FACE",FACE,{"disambiguationData":[OSD([sQuery(id+"F22.wireOp",EDGE,"E56")])]})]});
            var Q230;
            Q230=makeQuery(id+"F23.boolean.opBoolean","INTERSECT",EDGE,{"derivedFrom":[makeQuery(id+"F21.opExtrude","SWEPT_FACE",FACE,{"disambiguationData":[OSD([sQuery(id+"F20.wireOp",EDGE,"E47.6.0.2")])]}),makeQuery(id+"F23.opExtrude","SWEPT_FACE",FACE,{"disambiguationData":[OSD([sQuery(id+"F22.wireOp",EDGE,"E57")])]})]});
            var Q231;
            Q231=makeQuery(id+"F23.boolean.opBoolean","INTERSECT",EDGE,{"derivedFrom":[makeQuery(id+"F21.opExtrude","SWEPT_FACE",FACE,{"disambiguationData":[OSD([sQuery(id+"F20.wireOp",EDGE,"E47.6.0.2")])]}),makeQuery(id+"F23.opExtrude","SWEPT_FACE",FACE,{"disambiguationData":[OSD([sQuery(id+"F22.wireOp",EDGE,"E61")])]})]});
            var Q232;
            Q232=makeQuery(id+"F23.boolean.opBoolean","INTERSECT",EDGE,{"derivedFrom":[makeQuery(id+"F21.opExtrude","SWEPT_FACE",FACE,{"disambiguationData":[OSD([sQuery(id+"F20.wireOp",EDGE,"E47.6.0.2")])]}),makeQuery(id+"F23.opExtrude","SWEPT_FACE",FACE,{"disambiguationData":[OSD([sQuery(id+"F22.wireOp",EDGE,"E62")])]})]});
            var Q233;
            Q233=makeQuery(id+"F23.boolean.opBoolean","INTERSECT",EDGE,{"derivedFrom":[makeQuery(id+"F21.opExtrude","SWEPT_FACE",FACE,{"disambiguationData":[OSD([sQuery(id+"F20.wireOp",EDGE,"E47.6.0.2")])]}),makeQuery(id+"F23.opExtrude","SWEPT_FACE",FACE,{"disambiguationData":[OSD([sQuery(id+"F22.wireOp",EDGE,"E67")])]})]});
            var Q234;
            Q234=makeQuery(id+"F23.boolean.opBoolean","INTERSECT",EDGE,{"derivedFrom":[makeQuery(id+"F21.opExtrude","SWEPT_FACE",FACE,{"disambiguationData":[OSD([sQuery(id+"F20.wireOp",EDGE,"E47.6.0.2")])]}),makeQuery(id+"F23.opExtrude","SWEPT_FACE",FACE,{"disambiguationData":[OSD([sQuery(id+"F22.wireOp",EDGE,"E68")])]})]});
            var Q235;
            Q235=makeQuery(id+"F23.boolean.opBoolean","INTERSECT",EDGE,{"derivedFrom":[makeQuery(id+"F21.opExtrude","SWEPT_FACE",FACE,{"disambiguationData":[OSD([sQuery(id+"F20.wireOp",EDGE,"E47.6.0.2")])]}),makeQuery(id+"F23.opExtrude","SWEPT_FACE",FACE,{"disambiguationData":[OSD([sQuery(id+"F22.wireOp",EDGE,"E73")])]})]});
            var Q236;
            Q236=makeQuery(id+"F23.boolean.opBoolean","INTERSECT",EDGE,{"derivedFrom":[makeQuery(id+"F21.opExtrude","SWEPT_FACE",FACE,{"disambiguationData":[OSD([sQuery(id+"F20.wireOp",EDGE,"E47.6.0.2")])]}),makeQuery(id+"F23.opExtrude","SWEPT_FACE",FACE,{"disambiguationData":[OSD([sQuery(id+"F22.wireOp",EDGE,"E74")])]})]});
            var Q237;
            Q237=makeQuery(id+"F23.boolean.opBoolean","INTERSECT",EDGE,{"derivedFrom":[makeQuery(id+"F21.opExtrude","SWEPT_FACE",FACE,{"disambiguationData":[OSD([sQuery(id+"F20.wireOp",EDGE,"E47.7.0.2")])]}),makeQuery(id+"F23.opExtrude","SWEPT_FACE",FACE,{"disambiguationData":[OSD([sQuery(id+"F22.wireOp",EDGE,"E73")])]})]});
            var Q238;
            Q238=makeQuery(id+"F23.boolean.opBoolean","INTERSECT",EDGE,{"derivedFrom":[makeQuery(id+"F21.opExtrude","SWEPT_FACE",FACE,{"disambiguationData":[OSD([sQuery(id+"F20.wireOp",EDGE,"E47.7.0.2")])]}),makeQuery(id+"F23.opExtrude","SWEPT_FACE",FACE,{"disambiguationData":[OSD([sQuery(id+"F22.wireOp",EDGE,"E68")])]})]});
            var Q239;
            Q239=makeQuery(id+"F23.boolean.opBoolean","INTERSECT",EDGE,{"derivedFrom":[makeQuery(id+"F21.opExtrude","SWEPT_FACE",FACE,{"disambiguationData":[OSD([sQuery(id+"F20.wireOp",EDGE,"E47.7.0.2")])]}),makeQuery(id+"F23.opExtrude","SWEPT_FACE",FACE,{"disambiguationData":[OSD([sQuery(id+"F22.wireOp",EDGE,"E67")])]})]});
            var Q240;
            Q240=makeQuery(id+"F23.boolean.opBoolean","INTERSECT",EDGE,{"derivedFrom":[makeQuery(id+"F21.opExtrude","SWEPT_FACE",FACE,{"disambiguationData":[OSD([sQuery(id+"F20.wireOp",EDGE,"E47.7.0.2")])]}),makeQuery(id+"F23.opExtrude","SWEPT_FACE",FACE,{"disambiguationData":[OSD([sQuery(id+"F22.wireOp",EDGE,"E62")])]})]});
            var Q241;
            Q241=makeQuery(id+"F23.boolean.opBoolean","INTERSECT",EDGE,{"derivedFrom":[makeQuery(id+"F21.opExtrude","SWEPT_FACE",FACE,{"disambiguationData":[OSD([sQuery(id+"F20.wireOp",EDGE,"E47.7.0.2")])]}),makeQuery(id+"F23.opExtrude","SWEPT_FACE",FACE,{"disambiguationData":[OSD([sQuery(id+"F22.wireOp",EDGE,"E61")])]})]});
            var Q242;
            Q242=makeQuery(id+"F23.boolean.opBoolean","INTERSECT",EDGE,{"derivedFrom":[makeQuery(id+"F21.opExtrude","SWEPT_FACE",FACE,{"disambiguationData":[OSD([sQuery(id+"F20.wireOp",EDGE,"E47.7.0.2")])]}),makeQuery(id+"F23.opExtrude","SWEPT_FACE",FACE,{"disambiguationData":[OSD([sQuery(id+"F22.wireOp",EDGE,"E57")])]})]});
            var Q243;
            Q243=makeQuery(id+"F23.boolean.opBoolean","INTERSECT",EDGE,{"derivedFrom":[makeQuery(id+"F21.opExtrude","SWEPT_FACE",FACE,{"disambiguationData":[OSD([sQuery(id+"F20.wireOp",EDGE,"E47.7.0.2")])]}),makeQuery(id+"F23.opExtrude","SWEPT_FACE",FACE,{"disambiguationData":[OSD([sQuery(id+"F22.wireOp",EDGE,"E56")])]})]});
            var Q244;
            Q244=makeQuery(id+"F23.boolean.opBoolean","INTERSECT",EDGE,{"derivedFrom":[makeQuery(id+"F21.opExtrude","SWEPT_FACE",FACE,{"disambiguationData":[OSD([sQuery(id+"F20.wireOp",EDGE,"E47.7.0.2")])]}),makeQuery(id+"F23.opExtrude","SWEPT_FACE",FACE,{"disambiguationData":[OSD([sQuery(id+"F22.wireOp",EDGE,"E49")])]})]});
            var Q245;
            Q245=makeQuery(id+"F23.boolean.opBoolean","INTERSECT",EDGE,{"derivedFrom":[makeQuery(id+"F21.opExtrude","SWEPT_FACE",FACE,{"disambiguationData":[OSD([sQuery(id+"F20.wireOp",EDGE,"E47.7.0.2")])]}),makeQuery(id+"F23.opExtrude","SWEPT_FACE",FACE,{"disambiguationData":[OSD([sQuery(id+"F22.wireOp",EDGE,"E48")])]})]});
            var Q246;
            Q246=makeQuery(id+"F23.boolean.opBoolean","INTERSECT",EDGE,{"derivedFrom":[makeQuery(id+"F21.opExtrude","SWEPT_FACE",FACE,{"disambiguationData":[OSD([sQuery(id+"F20.wireOp",EDGE,"E47.8.0.2")])]}),makeQuery(id+"F23.opExtrude","SWEPT_FACE",FACE,{"disambiguationData":[OSD([sQuery(id+"F22.wireOp",EDGE,"E48")])]})]});
            var Q247;
            Q247=makeQuery(id+"F23.boolean.opBoolean","INTERSECT",EDGE,{"derivedFrom":[makeQuery(id+"F21.opExtrude","SWEPT_FACE",FACE,{"disambiguationData":[OSD([sQuery(id+"F20.wireOp",EDGE,"E47.8.0.2")])]}),makeQuery(id+"F23.opExtrude","SWEPT_FACE",FACE,{"disambiguationData":[OSD([sQuery(id+"F22.wireOp",EDGE,"E49")])]})]});
            var Q248;
            Q248=makeQuery(id+"F23.boolean.opBoolean","INTERSECT",EDGE,{"derivedFrom":[makeQuery(id+"F21.opExtrude","SWEPT_FACE",FACE,{"disambiguationData":[OSD([sQuery(id+"F20.wireOp",EDGE,"E47.8.0.2")])]}),makeQuery(id+"F23.opExtrude","SWEPT_FACE",FACE,{"disambiguationData":[OSD([sQuery(id+"F22.wireOp",EDGE,"E56")])]})]});
            var Q249;
            Q249=makeQuery(id+"F23.boolean.opBoolean","INTERSECT",EDGE,{"derivedFrom":[makeQuery(id+"F21.opExtrude","SWEPT_FACE",FACE,{"disambiguationData":[OSD([sQuery(id+"F20.wireOp",EDGE,"E47.8.0.2")])]}),makeQuery(id+"F23.opExtrude","SWEPT_FACE",FACE,{"disambiguationData":[OSD([sQuery(id+"F22.wireOp",EDGE,"E57")])]})]});
            var Q250;
            Q250=makeQuery(id+"F23.boolean.opBoolean","INTERSECT",EDGE,{"derivedFrom":[makeQuery(id+"F21.opExtrude","SWEPT_FACE",FACE,{"disambiguationData":[OSD([sQuery(id+"F20.wireOp",EDGE,"E47.8.0.2")])]}),makeQuery(id+"F23.opExtrude","SWEPT_FACE",FACE,{"disambiguationData":[OSD([sQuery(id+"F22.wireOp",EDGE,"E61")])]})]});
            var Q251;
            Q251=makeQuery(id+"F23.boolean.opBoolean","INTERSECT",EDGE,{"derivedFrom":[makeQuery(id+"F21.opExtrude","SWEPT_FACE",FACE,{"disambiguationData":[OSD([sQuery(id+"F20.wireOp",EDGE,"E47.8.0.2")])]}),makeQuery(id+"F23.opExtrude","SWEPT_FACE",FACE,{"disambiguationData":[OSD([sQuery(id+"F22.wireOp",EDGE,"E62")])]})]});
            var Q252;
            Q252=makeQuery(id+"F23.boolean.opBoolean","INTERSECT",EDGE,{"derivedFrom":[makeQuery(id+"F21.opExtrude","SWEPT_FACE",FACE,{"disambiguationData":[OSD([sQuery(id+"F20.wireOp",EDGE,"E47.8.0.2")])]}),makeQuery(id+"F23.opExtrude","SWEPT_FACE",FACE,{"disambiguationData":[OSD([sQuery(id+"F22.wireOp",EDGE,"E67")])]})]});
            var Q253;
            Q253=makeQuery(id+"F23.boolean.opBoolean","INTERSECT",EDGE,{"derivedFrom":[makeQuery(id+"F21.opExtrude","SWEPT_FACE",FACE,{"disambiguationData":[OSD([sQuery(id+"F20.wireOp",EDGE,"E47.8.0.2")])]}),makeQuery(id+"F23.opExtrude","SWEPT_FACE",FACE,{"disambiguationData":[OSD([sQuery(id+"F22.wireOp",EDGE,"E68")])]})]});
            var Q254;
            Q254=makeQuery(id+"F23.boolean.opBoolean","INTERSECT",EDGE,{"derivedFrom":[makeQuery(id+"F21.opExtrude","SWEPT_FACE",FACE,{"disambiguationData":[OSD([sQuery(id+"F20.wireOp",EDGE,"E47.8.0.2")])]}),makeQuery(id+"F23.opExtrude","SWEPT_FACE",FACE,{"disambiguationData":[OSD([sQuery(id+"F22.wireOp",EDGE,"E73")])]})]});
            var Q255;
            Q255=makeQuery(id+"F23.boolean.opBoolean","INTERSECT",EDGE,{"derivedFrom":[makeQuery(id+"F21.opExtrude","SWEPT_FACE",FACE,{"disambiguationData":[OSD([sQuery(id+"F20.wireOp",EDGE,"E47.8.0.2")])]}),makeQuery(id+"F23.opExtrude","SWEPT_FACE",FACE,{"disambiguationData":[OSD([sQuery(id+"F22.wireOp",EDGE,"E74")])]})]});
            var Q256;
            Q256=makeQuery(id+"F23.boolean.opBoolean","INTERSECT",EDGE,{"derivedFrom":[makeQuery(id+"F21.opExtrude","SWEPT_FACE",FACE,{"disambiguationData":[OSD([sQuery(id+"F20.wireOp",EDGE,"E47.9.0.2")])]}),makeQuery(id+"F23.opExtrude","SWEPT_FACE",FACE,{"disambiguationData":[OSD([sQuery(id+"F22.wireOp",EDGE,"E74")])]})]});
            var Q257;
            Q257=makeQuery(id+"F23.boolean.opBoolean","INTERSECT",EDGE,{"derivedFrom":[makeQuery(id+"F21.opExtrude","SWEPT_FACE",FACE,{"disambiguationData":[OSD([sQuery(id+"F20.wireOp",EDGE,"E47.9.0.2")])]}),makeQuery(id+"F23.opExtrude","SWEPT_FACE",FACE,{"disambiguationData":[OSD([sQuery(id+"F22.wireOp",EDGE,"E73")])]})]});
            var Q258;
            Q258=makeQuery(id+"F23.boolean.opBoolean","INTERSECT",EDGE,{"derivedFrom":[makeQuery(id+"F21.opExtrude","SWEPT_FACE",FACE,{"disambiguationData":[OSD([sQuery(id+"F20.wireOp",EDGE,"E47.9.0.2")])]}),makeQuery(id+"F23.opExtrude","SWEPT_FACE",FACE,{"disambiguationData":[OSD([sQuery(id+"F22.wireOp",EDGE,"E68")])]})]});
            var Q259;
            Q259=makeQuery(id+"F23.boolean.opBoolean","INTERSECT",EDGE,{"derivedFrom":[makeQuery(id+"F21.opExtrude","SWEPT_FACE",FACE,{"disambiguationData":[OSD([sQuery(id+"F20.wireOp",EDGE,"E47.9.0.2")])]}),makeQuery(id+"F23.opExtrude","SWEPT_FACE",FACE,{"disambiguationData":[OSD([sQuery(id+"F22.wireOp",EDGE,"E67")])]})]});
            var Q260;
            Q260=makeQuery(id+"F23.boolean.opBoolean","INTERSECT",EDGE,{"derivedFrom":[makeQuery(id+"F21.opExtrude","SWEPT_FACE",FACE,{"disambiguationData":[OSD([sQuery(id+"F20.wireOp",EDGE,"E47.9.0.2")])]}),makeQuery(id+"F23.opExtrude","SWEPT_FACE",FACE,{"disambiguationData":[OSD([sQuery(id+"F22.wireOp",EDGE,"E62")])]})]});
            var Q261;
            Q261=makeQuery(id+"F23.boolean.opBoolean","INTERSECT",EDGE,{"derivedFrom":[makeQuery(id+"F21.opExtrude","SWEPT_FACE",FACE,{"disambiguationData":[OSD([sQuery(id+"F20.wireOp",EDGE,"E47.9.0.2")])]}),makeQuery(id+"F23.opExtrude","SWEPT_FACE",FACE,{"disambiguationData":[OSD([sQuery(id+"F22.wireOp",EDGE,"E61")])]})]});
            var Q262;
            Q262=makeQuery(id+"F23.boolean.opBoolean","INTERSECT",EDGE,{"derivedFrom":[makeQuery(id+"F21.opExtrude","SWEPT_FACE",FACE,{"disambiguationData":[OSD([sQuery(id+"F20.wireOp",EDGE,"E47.9.0.2")])]}),makeQuery(id+"F23.opExtrude","SWEPT_FACE",FACE,{"disambiguationData":[OSD([sQuery(id+"F22.wireOp",EDGE,"E57")])]})]});
            var Q263;
            Q263=makeQuery(id+"F23.boolean.opBoolean","INTERSECT",EDGE,{"derivedFrom":[makeQuery(id+"F21.opExtrude","SWEPT_FACE",FACE,{"disambiguationData":[OSD([sQuery(id+"F20.wireOp",EDGE,"E47.9.0.2")])]}),makeQuery(id+"F23.opExtrude","SWEPT_FACE",FACE,{"disambiguationData":[OSD([sQuery(id+"F22.wireOp",EDGE,"E56")])]})]});
            var Q264;
            Q264=makeQuery(id+"F23.boolean.opBoolean","INTERSECT",EDGE,{"derivedFrom":[makeQuery(id+"F21.opExtrude","SWEPT_FACE",FACE,{"disambiguationData":[OSD([sQuery(id+"F20.wireOp",EDGE,"E47.9.0.2")])]}),makeQuery(id+"F23.opExtrude","SWEPT_FACE",FACE,{"disambiguationData":[OSD([sQuery(id+"F22.wireOp",EDGE,"E49")])]})]});
            var Q265;
            Q265=makeQuery(id+"F23.boolean.opBoolean","INTERSECT",EDGE,{"derivedFrom":[makeQuery(id+"F21.opExtrude","SWEPT_FACE",FACE,{"disambiguationData":[OSD([sQuery(id+"F20.wireOp",EDGE,"E47.9.0.2")])]}),makeQuery(id+"F23.opExtrude","SWEPT_FACE",FACE,{"disambiguationData":[OSD([sQuery(id+"F22.wireOp",EDGE,"E48")])]})]});
            var Q266;
            Q266=makeQuery(id+"F23.boolean.opBoolean","INTERSECT",EDGE,{"derivedFrom":[makeQuery(id+"F21.opExtrude","SWEPT_FACE",FACE,{"disambiguationData":[OSD([sQuery(id+"F20.wireOp",EDGE,"E47.10.0.2")])]}),makeQuery(id+"F23.opExtrude","SWEPT_FACE",FACE,{"disambiguationData":[OSD([sQuery(id+"F22.wireOp",EDGE,"E48")])]})]});
            var Q267;
            Q267=makeQuery(id+"F23.boolean.opBoolean","INTERSECT",EDGE,{"derivedFrom":[makeQuery(id+"F21.opExtrude","SWEPT_FACE",FACE,{"disambiguationData":[OSD([sQuery(id+"F20.wireOp",EDGE,"E47.10.0.2")])]}),makeQuery(id+"F23.opExtrude","SWEPT_FACE",FACE,{"disambiguationData":[OSD([sQuery(id+"F22.wireOp",EDGE,"E49")])]})]});
            var Q268;
            Q268=makeQuery(id+"F23.boolean.opBoolean","INTERSECT",EDGE,{"derivedFrom":[makeQuery(id+"F21.opExtrude","SWEPT_FACE",FACE,{"disambiguationData":[OSD([sQuery(id+"F20.wireOp",EDGE,"E47.10.0.2")])]}),makeQuery(id+"F23.opExtrude","SWEPT_FACE",FACE,{"disambiguationData":[OSD([sQuery(id+"F22.wireOp",EDGE,"E56")])]})]});
            var Q269;
            Q269=makeQuery(id+"F23.boolean.opBoolean","INTERSECT",EDGE,{"derivedFrom":[makeQuery(id+"F21.opExtrude","SWEPT_FACE",FACE,{"disambiguationData":[OSD([sQuery(id+"F20.wireOp",EDGE,"E47.10.0.2")])]}),makeQuery(id+"F23.opExtrude","SWEPT_FACE",FACE,{"disambiguationData":[OSD([sQuery(id+"F22.wireOp",EDGE,"E57")])]})]});
            var Q270;
            Q270=makeQuery(id+"F23.boolean.opBoolean","INTERSECT",EDGE,{"derivedFrom":[makeQuery(id+"F21.opExtrude","SWEPT_FACE",FACE,{"disambiguationData":[OSD([sQuery(id+"F20.wireOp",EDGE,"E47.10.0.2")])]}),makeQuery(id+"F23.opExtrude","SWEPT_FACE",FACE,{"disambiguationData":[OSD([sQuery(id+"F22.wireOp",EDGE,"E61")])]})]});
            var Q271;
            Q271=makeQuery(id+"F23.boolean.opBoolean","INTERSECT",EDGE,{"derivedFrom":[makeQuery(id+"F21.opExtrude","SWEPT_FACE",FACE,{"disambiguationData":[OSD([sQuery(id+"F20.wireOp",EDGE,"E47.10.0.2")])]}),makeQuery(id+"F23.opExtrude","SWEPT_FACE",FACE,{"disambiguationData":[OSD([sQuery(id+"F22.wireOp",EDGE,"E62")])]})]});
            var Q272;
            Q272=makeQuery(id+"F23.boolean.opBoolean","INTERSECT",EDGE,{"derivedFrom":[makeQuery(id+"F21.opExtrude","SWEPT_FACE",FACE,{"disambiguationData":[OSD([sQuery(id+"F20.wireOp",EDGE,"E47.10.0.2")])]}),makeQuery(id+"F23.opExtrude","SWEPT_FACE",FACE,{"disambiguationData":[OSD([sQuery(id+"F22.wireOp",EDGE,"E67")])]})]});
            var Q273;
            Q273=makeQuery(id+"F23.boolean.opBoolean","INTERSECT",EDGE,{"derivedFrom":[makeQuery(id+"F21.opExtrude","SWEPT_FACE",FACE,{"disambiguationData":[OSD([sQuery(id+"F20.wireOp",EDGE,"E47.10.0.2")])]}),makeQuery(id+"F23.opExtrude","SWEPT_FACE",FACE,{"disambiguationData":[OSD([sQuery(id+"F22.wireOp",EDGE,"E68")])]})]});
            var Q274;
            Q274=makeQuery(id+"F23.boolean.opBoolean","INTERSECT",EDGE,{"derivedFrom":[makeQuery(id+"F21.opExtrude","SWEPT_FACE",FACE,{"disambiguationData":[OSD([sQuery(id+"F20.wireOp",EDGE,"E47.10.0.2")])]}),makeQuery(id+"F23.opExtrude","SWEPT_FACE",FACE,{"disambiguationData":[OSD([sQuery(id+"F22.wireOp",EDGE,"E73")])]})]});
            var Q275;
            Q275=makeQuery(id+"F23.boolean.opBoolean","INTERSECT",EDGE,{"derivedFrom":[makeQuery(id+"F21.opExtrude","SWEPT_FACE",FACE,{"disambiguationData":[OSD([sQuery(id+"F20.wireOp",EDGE,"E47.10.0.2")])]}),makeQuery(id+"F23.opExtrude","SWEPT_FACE",FACE,{"disambiguationData":[OSD([sQuery(id+"F22.wireOp",EDGE,"E74")])]})]});
            var Q276;
            Q276=makeQuery(id+"F23.boolean.opBoolean","INTERSECT",EDGE,{"derivedFrom":[makeQuery(id+"F21.opExtrude","SWEPT_FACE",FACE,{"disambiguationData":[OSD([sQuery(id+"F20.wireOp",EDGE,"E47.11.0.2")])]}),makeQuery(id+"F23.opExtrude","SWEPT_FACE",FACE,{"disambiguationData":[OSD([sQuery(id+"F22.wireOp",EDGE,"E74")])]})]});
            var Q277;
            Q277=makeQuery(id+"F23.boolean.opBoolean","INTERSECT",EDGE,{"derivedFrom":[makeQuery(id+"F21.opExtrude","SWEPT_FACE",FACE,{"disambiguationData":[OSD([sQuery(id+"F20.wireOp",EDGE,"E47.11.0.2")])]}),makeQuery(id+"F23.opExtrude","SWEPT_FACE",FACE,{"disambiguationData":[OSD([sQuery(id+"F22.wireOp",EDGE,"E73")])]})]});
            var Q278;
            Q278=makeQuery(id+"F23.boolean.opBoolean","INTERSECT",EDGE,{"derivedFrom":[makeQuery(id+"F21.opExtrude","SWEPT_FACE",FACE,{"disambiguationData":[OSD([sQuery(id+"F20.wireOp",EDGE,"E47.11.0.2")])]}),makeQuery(id+"F23.opExtrude","SWEPT_FACE",FACE,{"disambiguationData":[OSD([sQuery(id+"F22.wireOp",EDGE,"E68")])]})]});
            var Q279;
            Q279=makeQuery(id+"F23.boolean.opBoolean","INTERSECT",EDGE,{"derivedFrom":[makeQuery(id+"F21.opExtrude","SWEPT_FACE",FACE,{"disambiguationData":[OSD([sQuery(id+"F20.wireOp",EDGE,"E47.11.0.2")])]}),makeQuery(id+"F23.opExtrude","SWEPT_FACE",FACE,{"disambiguationData":[OSD([sQuery(id+"F22.wireOp",EDGE,"E67")])]})]});
            var Q280;
            Q280=makeQuery(id+"F23.boolean.opBoolean","INTERSECT",EDGE,{"derivedFrom":[makeQuery(id+"F21.opExtrude","SWEPT_FACE",FACE,{"disambiguationData":[OSD([sQuery(id+"F20.wireOp",EDGE,"E47.11.0.2")])]}),makeQuery(id+"F23.opExtrude","SWEPT_FACE",FACE,{"disambiguationData":[OSD([sQuery(id+"F22.wireOp",EDGE,"E62")])]})]});
            var Q281;
            Q281=makeQuery(id+"F23.boolean.opBoolean","INTERSECT",EDGE,{"derivedFrom":[makeQuery(id+"F21.opExtrude","SWEPT_FACE",FACE,{"disambiguationData":[OSD([sQuery(id+"F20.wireOp",EDGE,"E47.11.0.2")])]}),makeQuery(id+"F23.opExtrude","SWEPT_FACE",FACE,{"disambiguationData":[OSD([sQuery(id+"F22.wireOp",EDGE,"E61")])]})]});
            var Q282;
            Q282=makeQuery(id+"F23.boolean.opBoolean","INTERSECT",EDGE,{"derivedFrom":[makeQuery(id+"F21.opExtrude","SWEPT_FACE",FACE,{"disambiguationData":[OSD([sQuery(id+"F20.wireOp",EDGE,"E47.11.0.2")])]}),makeQuery(id+"F23.opExtrude","SWEPT_FACE",FACE,{"disambiguationData":[OSD([sQuery(id+"F22.wireOp",EDGE,"E57")])]})]});
            var Q283;
            Q283=makeQuery(id+"F23.boolean.opBoolean","INTERSECT",EDGE,{"derivedFrom":[makeQuery(id+"F21.opExtrude","SWEPT_FACE",FACE,{"disambiguationData":[OSD([sQuery(id+"F20.wireOp",EDGE,"E47.11.0.2")])]}),makeQuery(id+"F23.opExtrude","SWEPT_FACE",FACE,{"disambiguationData":[OSD([sQuery(id+"F22.wireOp",EDGE,"E56")])]})]});
            var Q284;
            Q284=makeQuery(id+"F23.boolean.opBoolean","INTERSECT",EDGE,{"derivedFrom":[makeQuery(id+"F21.opExtrude","SWEPT_FACE",FACE,{"disambiguationData":[OSD([sQuery(id+"F20.wireOp",EDGE,"E47.11.0.2")])]}),makeQuery(id+"F23.opExtrude","SWEPT_FACE",FACE,{"disambiguationData":[OSD([sQuery(id+"F22.wireOp",EDGE,"E49")])]})]});
            var Q285;
            Q285=makeQuery(id+"F23.boolean.opBoolean","INTERSECT",EDGE,{"derivedFrom":[makeQuery(id+"F21.opExtrude","SWEPT_FACE",FACE,{"disambiguationData":[OSD([sQuery(id+"F20.wireOp",EDGE,"E47.11.0.2")])]}),makeQuery(id+"F23.opExtrude","SWEPT_FACE",FACE,{"disambiguationData":[OSD([sQuery(id+"F22.wireOp",EDGE,"E48")])]})]});
            var Q286;
            Q286=makeQuery(id+"F23.boolean.opBoolean","INTERSECT",EDGE,{"derivedFrom":[makeQuery(id+"F21.opExtrude","SWEPT_FACE",FACE,{"disambiguationData":[OSD([sQuery(id+"F20.wireOp",EDGE,"E47.12.0.2")])]}),makeQuery(id+"F23.opExtrude","SWEPT_FACE",FACE,{"disambiguationData":[OSD([sQuery(id+"F22.wireOp",EDGE,"E74")])]})]});
            var Q287;
            Q287=makeQuery(id+"F23.boolean.opBoolean","INTERSECT",EDGE,{"derivedFrom":[makeQuery(id+"F21.opExtrude","SWEPT_FACE",FACE,{"disambiguationData":[OSD([sQuery(id+"F20.wireOp",EDGE,"E47.12.0.2")])]}),makeQuery(id+"F23.opExtrude","SWEPT_FACE",FACE,{"disambiguationData":[OSD([sQuery(id+"F22.wireOp",EDGE,"E73")])]})]});
            var Q288;
            Q288=makeQuery(id+"F23.boolean.opBoolean","INTERSECT",EDGE,{"derivedFrom":[makeQuery(id+"F21.opExtrude","SWEPT_FACE",FACE,{"disambiguationData":[OSD([sQuery(id+"F20.wireOp",EDGE,"E47.12.0.2")])]}),makeQuery(id+"F23.opExtrude","SWEPT_FACE",FACE,{"disambiguationData":[OSD([sQuery(id+"F22.wireOp",EDGE,"E68")])]})]});
            var Q289;
            Q289=makeQuery(id+"F23.boolean.opBoolean","INTERSECT",EDGE,{"derivedFrom":[makeQuery(id+"F21.opExtrude","SWEPT_FACE",FACE,{"disambiguationData":[OSD([sQuery(id+"F20.wireOp",EDGE,"E47.12.0.2")])]}),makeQuery(id+"F23.opExtrude","SWEPT_FACE",FACE,{"disambiguationData":[OSD([sQuery(id+"F22.wireOp",EDGE,"E67")])]})]});
            var Q290;
            Q290=makeQuery(id+"F23.boolean.opBoolean","INTERSECT",EDGE,{"derivedFrom":[makeQuery(id+"F21.opExtrude","SWEPT_FACE",FACE,{"disambiguationData":[OSD([sQuery(id+"F20.wireOp",EDGE,"E47.12.0.2")])]}),makeQuery(id+"F23.opExtrude","SWEPT_FACE",FACE,{"disambiguationData":[OSD([sQuery(id+"F22.wireOp",EDGE,"E62")])]})]});
            var Q291;
            Q291=makeQuery(id+"F23.boolean.opBoolean","INTERSECT",EDGE,{"derivedFrom":[makeQuery(id+"F21.opExtrude","SWEPT_FACE",FACE,{"disambiguationData":[OSD([sQuery(id+"F20.wireOp",EDGE,"E47.12.0.2")])]}),makeQuery(id+"F23.opExtrude","SWEPT_FACE",FACE,{"disambiguationData":[OSD([sQuery(id+"F22.wireOp",EDGE,"E61")])]})]});
            var Q292;
            Q292=makeQuery(id+"F23.boolean.opBoolean","INTERSECT",EDGE,{"derivedFrom":[makeQuery(id+"F21.opExtrude","SWEPT_FACE",FACE,{"disambiguationData":[OSD([sQuery(id+"F20.wireOp",EDGE,"E47.12.0.2")])]}),makeQuery(id+"F23.opExtrude","SWEPT_FACE",FACE,{"disambiguationData":[OSD([sQuery(id+"F22.wireOp",EDGE,"E57")])]})]});
            var Q293;
            Q293=makeQuery(id+"F23.boolean.opBoolean","INTERSECT",EDGE,{"derivedFrom":[makeQuery(id+"F21.opExtrude","SWEPT_FACE",FACE,{"disambiguationData":[OSD([sQuery(id+"F20.wireOp",EDGE,"E47.12.0.2")])]}),makeQuery(id+"F23.opExtrude","SWEPT_FACE",FACE,{"disambiguationData":[OSD([sQuery(id+"F22.wireOp",EDGE,"E56")])]})]});
            var Q294;
            Q294=makeQuery(id+"F23.boolean.opBoolean","INTERSECT",EDGE,{"derivedFrom":[makeQuery(id+"F21.opExtrude","SWEPT_FACE",FACE,{"disambiguationData":[OSD([sQuery(id+"F20.wireOp",EDGE,"E47.12.0.2")])]}),makeQuery(id+"F23.opExtrude","SWEPT_FACE",FACE,{"disambiguationData":[OSD([sQuery(id+"F22.wireOp",EDGE,"E56")])]})]});
            var Q295;
            Q295=makeQuery(id+"F23.boolean.opBoolean","INTERSECT",EDGE,{"derivedFrom":[makeQuery(id+"F21.opExtrude","SWEPT_FACE",FACE,{"disambiguationData":[OSD([sQuery(id+"F20.wireOp",EDGE,"E47.12.0.2")])]}),makeQuery(id+"F23.opExtrude","SWEPT_FACE",FACE,{"disambiguationData":[OSD([sQuery(id+"F22.wireOp",EDGE,"E49")])]})]});
            var Q296;
            Q296=makeQuery(id+"F23.boolean.opBoolean","INTERSECT",EDGE,{"derivedFrom":[makeQuery(id+"F21.opExtrude","SWEPT_FACE",FACE,{"disambiguationData":[OSD([sQuery(id+"F20.wireOp",EDGE,"E47.12.0.2")])]}),makeQuery(id+"F23.opExtrude","SWEPT_FACE",FACE,{"disambiguationData":[OSD([sQuery(id+"F22.wireOp",EDGE,"E48")])]})]});
            var Q297;
            Q297=makeQuery(id+"F23.boolean.opBoolean","INTERSECT",EDGE,{"derivedFrom":[makeQuery(id+"F21.opExtrude","SWEPT_FACE",FACE,{"disambiguationData":[OSD([sQuery(id+"F20.wireOp",EDGE,"E47.13.0.2")])]}),makeQuery(id+"F23.opExtrude","SWEPT_FACE",FACE,{"disambiguationData":[OSD([sQuery(id+"F22.wireOp",EDGE,"E48")])]})]});
            var Q298;
            Q298=makeQuery(id+"F23.boolean.opBoolean","INTERSECT",EDGE,{"derivedFrom":[makeQuery(id+"F21.opExtrude","SWEPT_FACE",FACE,{"disambiguationData":[OSD([sQuery(id+"F20.wireOp",EDGE,"E47.13.0.2")])]}),makeQuery(id+"F23.opExtrude","SWEPT_FACE",FACE,{"disambiguationData":[OSD([sQuery(id+"F22.wireOp",EDGE,"E49")])]})]});
            var Q299;
            Q299=makeQuery(id+"F23.boolean.opBoolean","INTERSECT",EDGE,{"derivedFrom":[makeQuery(id+"F21.opExtrude","SWEPT_FACE",FACE,{"disambiguationData":[OSD([sQuery(id+"F20.wireOp",EDGE,"E47.13.0.2")])]}),makeQuery(id+"F23.opExtrude","SWEPT_FACE",FACE,{"disambiguationData":[OSD([sQuery(id+"F22.wireOp",EDGE,"E56")])]})]});
            var Q300;
            Q300=makeQuery(id+"F23.boolean.opBoolean","INTERSECT",EDGE,{"derivedFrom":[makeQuery(id+"F21.opExtrude","SWEPT_FACE",FACE,{"disambiguationData":[OSD([sQuery(id+"F20.wireOp",EDGE,"E47.13.0.2")])]}),makeQuery(id+"F23.opExtrude","SWEPT_FACE",FACE,{"disambiguationData":[OSD([sQuery(id+"F22.wireOp",EDGE,"E57")])]})]});
            var Q301;
            Q301=makeQuery(id+"F23.boolean.opBoolean","INTERSECT",EDGE,{"derivedFrom":[makeQuery(id+"F21.opExtrude","SWEPT_FACE",FACE,{"disambiguationData":[OSD([sQuery(id+"F20.wireOp",EDGE,"E47.13.0.2")])]}),makeQuery(id+"F23.opExtrude","SWEPT_FACE",FACE,{"disambiguationData":[OSD([sQuery(id+"F22.wireOp",EDGE,"E61")])]})]});
            var Q302;
            Q302=makeQuery(id+"F23.boolean.opBoolean","INTERSECT",EDGE,{"derivedFrom":[makeQuery(id+"F21.opExtrude","SWEPT_FACE",FACE,{"disambiguationData":[OSD([sQuery(id+"F20.wireOp",EDGE,"E47.13.0.2")])]}),makeQuery(id+"F23.opExtrude","SWEPT_FACE",FACE,{"disambiguationData":[OSD([sQuery(id+"F22.wireOp",EDGE,"E62")])]})]});
            var Q303;
            Q303=makeQuery(id+"F23.boolean.opBoolean","INTERSECT",EDGE,{"derivedFrom":[makeQuery(id+"F21.opExtrude","SWEPT_FACE",FACE,{"disambiguationData":[OSD([sQuery(id+"F20.wireOp",EDGE,"E47.13.0.2")])]}),makeQuery(id+"F23.opExtrude","SWEPT_FACE",FACE,{"disambiguationData":[OSD([sQuery(id+"F22.wireOp",EDGE,"E67")])]})]});
            var Q304;
            Q304=makeQuery(id+"F23.boolean.opBoolean","INTERSECT",EDGE,{"derivedFrom":[makeQuery(id+"F21.opExtrude","SWEPT_FACE",FACE,{"disambiguationData":[OSD([sQuery(id+"F20.wireOp",EDGE,"E47.13.0.2")])]}),makeQuery(id+"F23.opExtrude","SWEPT_FACE",FACE,{"disambiguationData":[OSD([sQuery(id+"F22.wireOp",EDGE,"E68")])]})]});
            var Q305;
            Q305=makeQuery(id+"F23.boolean.opBoolean","INTERSECT",EDGE,{"derivedFrom":[makeQuery(id+"F21.opExtrude","SWEPT_FACE",FACE,{"disambiguationData":[OSD([sQuery(id+"F20.wireOp",EDGE,"E47.13.0.2")])]}),makeQuery(id+"F23.opExtrude","SWEPT_FACE",FACE,{"disambiguationData":[OSD([sQuery(id+"F22.wireOp",EDGE,"E73")])]})]});
            var Q306;
            Q306=makeQuery(id+"F23.boolean.opBoolean","INTERSECT",EDGE,{"derivedFrom":[makeQuery(id+"F21.opExtrude","SWEPT_FACE",FACE,{"disambiguationData":[OSD([sQuery(id+"F20.wireOp",EDGE,"E47.13.0.2")])]}),makeQuery(id+"F23.opExtrude","SWEPT_FACE",FACE,{"disambiguationData":[OSD([sQuery(id+"F22.wireOp",EDGE,"E74")])]})]});
            var Q307;
            Q307=makeQuery(id+"F23.boolean.opBoolean","INTERSECT",EDGE,{"derivedFrom":[makeQuery(id+"F21.opExtrude","SWEPT_FACE",FACE,{"disambiguationData":[OSD([sQuery(id+"F20.wireOp",EDGE,"E47.14.0.2")])]}),makeQuery(id+"F23.opExtrude","SWEPT_FACE",FACE,{"disambiguationData":[OSD([sQuery(id+"F22.wireOp",EDGE,"E74")])]})]});
            var Q308;
            Q308=makeQuery(id+"F23.boolean.opBoolean","INTERSECT",EDGE,{"derivedFrom":[makeQuery(id+"F21.opExtrude","SWEPT_FACE",FACE,{"disambiguationData":[OSD([sQuery(id+"F20.wireOp",EDGE,"E47.14.0.2")])]}),makeQuery(id+"F23.opExtrude","SWEPT_FACE",FACE,{"disambiguationData":[OSD([sQuery(id+"F22.wireOp",EDGE,"E73")])]})]});
            var Q309;
            Q309=makeQuery(id+"F23.boolean.opBoolean","INTERSECT",EDGE,{"derivedFrom":[makeQuery(id+"F21.opExtrude","SWEPT_FACE",FACE,{"disambiguationData":[OSD([sQuery(id+"F20.wireOp",EDGE,"E47.14.0.2")])]}),makeQuery(id+"F23.opExtrude","SWEPT_FACE",FACE,{"disambiguationData":[OSD([sQuery(id+"F22.wireOp",EDGE,"E68")])]})]});
            var Q310;
            Q310=makeQuery(id+"F23.boolean.opBoolean","INTERSECT",EDGE,{"derivedFrom":[makeQuery(id+"F21.opExtrude","SWEPT_FACE",FACE,{"disambiguationData":[OSD([sQuery(id+"F20.wireOp",EDGE,"E47.14.0.2")])]}),makeQuery(id+"F23.opExtrude","SWEPT_FACE",FACE,{"disambiguationData":[OSD([sQuery(id+"F22.wireOp",EDGE,"E67")])]})]});
            var Q311;
            Q311=makeQuery(id+"F23.boolean.opBoolean","INTERSECT",EDGE,{"derivedFrom":[makeQuery(id+"F21.opExtrude","SWEPT_FACE",FACE,{"disambiguationData":[OSD([sQuery(id+"F20.wireOp",EDGE,"E47.14.0.2")])]}),makeQuery(id+"F23.opExtrude","SWEPT_FACE",FACE,{"disambiguationData":[OSD([sQuery(id+"F22.wireOp",EDGE,"E62")])]})]});
            var Q312;
            Q312=makeQuery(id+"F23.boolean.opBoolean","INTERSECT",EDGE,{"derivedFrom":[makeQuery(id+"F21.opExtrude","SWEPT_FACE",FACE,{"disambiguationData":[OSD([sQuery(id+"F20.wireOp",EDGE,"E47.14.0.2")])]}),makeQuery(id+"F23.opExtrude","SWEPT_FACE",FACE,{"disambiguationData":[OSD([sQuery(id+"F22.wireOp",EDGE,"E61")])]})]});
            var Q313;
            Q313=makeQuery(id+"F23.boolean.opBoolean","INTERSECT",EDGE,{"derivedFrom":[makeQuery(id+"F21.opExtrude","SWEPT_FACE",FACE,{"disambiguationData":[OSD([sQuery(id+"F20.wireOp",EDGE,"E47.14.0.2")])]}),makeQuery(id+"F23.opExtrude","SWEPT_FACE",FACE,{"disambiguationData":[OSD([sQuery(id+"F22.wireOp",EDGE,"E57")])]})]});
            var Q314;
            Q314=makeQuery(id+"F23.boolean.opBoolean","INTERSECT",EDGE,{"derivedFrom":[makeQuery(id+"F21.opExtrude","SWEPT_FACE",FACE,{"disambiguationData":[OSD([sQuery(id+"F20.wireOp",EDGE,"E47.14.0.2")])]}),makeQuery(id+"F23.opExtrude","SWEPT_FACE",FACE,{"disambiguationData":[OSD([sQuery(id+"F22.wireOp",EDGE,"E56")])]})]});
            var Q315;
            Q315=makeQuery(id+"F23.boolean.opBoolean","INTERSECT",EDGE,{"derivedFrom":[makeQuery(id+"F21.opExtrude","SWEPT_FACE",FACE,{"disambiguationData":[OSD([sQuery(id+"F20.wireOp",EDGE,"E47.14.0.2")])]}),makeQuery(id+"F23.opExtrude","SWEPT_FACE",FACE,{"disambiguationData":[OSD([sQuery(id+"F22.wireOp",EDGE,"E49")])]})]});
            var Q316;
            Q316=makeQuery(id+"F23.boolean.opBoolean","INTERSECT",EDGE,{"derivedFrom":[makeQuery(id+"F21.opExtrude","SWEPT_FACE",FACE,{"disambiguationData":[OSD([sQuery(id+"F20.wireOp",EDGE,"E47.14.0.2")])]}),makeQuery(id+"F23.opExtrude","SWEPT_FACE",FACE,{"disambiguationData":[OSD([sQuery(id+"F22.wireOp",EDGE,"E48")])]})]});
            var Q317;
            Q317=makeQuery(id+"F23.boolean.opBoolean","INTERSECT",EDGE,{"derivedFrom":[makeQuery(id+"F21.opExtrude","SWEPT_FACE",FACE,{"disambiguationData":[OSD([sQuery(id+"F20.wireOp",EDGE,"E47.7.0.2")])]}),makeQuery(id+"F23.opExtrude","SWEPT_FACE",FACE,{"disambiguationData":[OSD([sQuery(id+"F22.wireOp",EDGE,"E74")])]})]});
            fillet(context, id + "F24", {"entities" : qUnion([Q0, Q1, Q2, Q3, Q4, Q5, Q6, Q7, Q8, Q9, Q10, Q11, Q12, Q13, Q14, Q15, Q16, Q17, Q18, Q19, Q20, Q21, Q22, Q23, Q24, Q25, Q26, Q27, Q28, Q29, Q30, Q31, Q32, Q33, Q34, Q35, Q36, Q37, Q38, Q39, Q40, Q41, Q42, Q43, Q44, Q45, Q46, Q47, Q48, Q49, Q50, Q51, Q52, Q53, Q54, Q55, Q56, Q57, Q58, Q59, Q60, Q61, Q62, Q63, Q64, Q65, Q66, Q67, Q68, Q69, Q70, Q71, Q72, Q73, Q74, Q75, Q76, Q77, Q78, Q79, Q80, Q81, Q82, Q83, Q84, Q85, Q86, Q87, Q88, Q89, Q90, Q91, Q92, Q93, Q94, Q95, Q96, Q97, Q98, Q99, Q100, Q101, Q102, Q103, Q104, Q105, Q106, Q107, Q108, Q109, Q110, Q111, Q112, Q113, Q114, Q115, Q116, Q117, Q118, Q119, Q120, Q121, Q122, Q123, Q124, Q125, Q126, Q127, Q128, Q129, Q130, Q131, Q132, Q133, Q134, Q135, Q136, Q137, Q138, Q139, Q140, Q141, Q142, Q143, Q144, Q145, Q146, Q147, Q148, Q149, Q150, Q151, Q152, Q153, Q154, Q155, Q156, Q157, Q158, Q159, Q160, Q161, Q162, Q163, Q164, Q165, Q166, Q167, Q168, Q169, Q170, Q171, Q172, Q173, Q174, Q175, Q176, Q177, Q178, Q179, Q180, Q181, Q182, Q183, Q184, Q185, Q186, Q187, Q188, Q189, Q190, Q191, Q192, Q193, Q194, Q195, Q196, Q197, Q198, Q199, Q200, Q201, Q202, Q203, Q204, Q205, Q206, Q207, Q208, Q209, Q210, Q211, Q212, Q213, Q214, Q215, Q216, Q217, Q218, Q219, Q220, Q221, Q222, Q223, Q224, Q225, Q226, Q227, Q228, Q229, Q230, Q231, Q232, Q233, Q234, Q235, Q236, Q237, Q238, Q239, Q240, Q241, Q242, Q243, Q244, Q245, Q246, Q247, Q248, Q249, Q250, Q251, Q252, Q253, Q254, Q255, Q256, Q257, Q258, Q259, Q260, Q261, Q262, Q263, Q264, Q265, Q266, Q267, Q268, Q269, Q270, Q271, Q272, Q273, Q274, Q275, Q276, Q277, Q278, Q279, Q280, Q281, Q282, Q283, Q284, Q285, Q286, Q287, Q288, Q289, Q290, Q291, Q292, Q293, Q294, Q295, Q296, Q297, Q298, Q299, Q300, Q301, Q302, Q303, Q304, Q305, Q306, Q307, Q308, Q309, Q310, Q311, Q312, Q313, Q314, Q315, Q316, Q317]), "radius" : 0.5 * mm, "tangentPropagation" : true, "allowEdgeOverflow" : false});
        }
        {
            var Q0;
            Q0=makeQuery(id+"F1.opExtrude","CAP_EDGE",EDGE,{"disambiguationData":[OSD([sQuery(id+"F0.wireOp",EDGE,"E2.bottom")])],"isStart":true});
            var Q1;
            Q1=makeQuery(id+"F1.opExtrude","CAP_EDGE",EDGE,{"disambiguationData":[OSD([sQuery(id+"F0.wireOp",EDGE,"E2.bottom")])],"isStart":false});
            var Q2;
            {var subQ0=sQuery(id+"F0.wireOp",EDGE,"E2.right");var subQ1=sQuery(id+"F0.wireOp",EDGE,"E2.bottom");var subQ3=sQuery(id+"F20.wireOp",EDGE,"E47.5.0.10");var subQ8=sQuery(id+"F20.wireOp",EDGE,"E47.4.0.10");var subQ12=sQuery(id+"F20.wireOp",EDGE,"E47.3.0.10");var subQ16=sQuery(id+"F20.wireOp",EDGE,"E47.6.0.10");var subQ19=sQuery(id+"F20.wireOp",EDGE,"E47.2.0.10");var subQ21=sQuery(id+"F20.wireOp",EDGE,"E46.filletArc");var subQ22=sQuery(id+"F20.wireOp",EDGE,"E45.filletArc");var subQ25=sQuery(id+"F20.wireOp",EDGE,"E47.7.0.10");var subQ28=sQuery(id+"F20.wireOp",EDGE,"E47.1.0.10");var subQ31=sQuery(id+"F20.wireOp",EDGE,"E47.13.0.10");var subQ34=sQuery(id+"F20.wireOp",EDGE,"E47.8.0.10");var subQ37=sQuery(id+"F20.wireOp",EDGE,"E47.9.0.10");var subQ40=sQuery(id+"F20.wireOp",EDGE,"E47.10.0.10");var subQ43=sQuery(id+"F20.wireOp",EDGE,"E47.11.0.10");var subQ46=sQuery(id+"F20.wireOp",EDGE,"E47.12.0.10");var subQ49=sQuery(id+"F20.wireOp",EDGE,"E47.14.0.10");var subQ51=sQuery(id+"F20.wireOp",EDGE,"E47.15.0.10");var subQ53=makeQuery(id+"F1.opExtrude","SWEPT_EDGE",EDGE,{"disambiguationData":[OSD([subQ1,subQ0])]});Q2=makeQuery(id+"F23.boolean.opBoolean","MERGE",EDGE,{"derivedFrom":[makeQuery(id+"F21.boolean.opBoolean","SPLIT",EDGE,{"disambiguationData":[TD([makeQuery(id+"F21.opExtrude","SWEPT_FACE",FACE,{"disambiguationData":[OSD([subQ51])]})])],"derivedFrom":subQ53}),makeQuery(id+"F21.boolean.opBoolean","SPLIT",EDGE,{"disambiguationData":[TD([makeQuery(id+"F21.opExtrude","SWEPT_FACE",FACE,{"disambiguationData":[OSD([subQ22])]})])],"derivedFrom":subQ53}),makeQuery(id+"F21.boolean.opBoolean","SPLIT",EDGE,{"disambiguationData":[TD([makeQuery(id+"F21.opExtrude","SWEPT_FACE",FACE,{"disambiguationData":[OSD([subQ21])]})])],"derivedFrom":subQ53}),makeQuery(id+"F21.boolean.opBoolean","SPLIT",EDGE,{"disambiguationData":[TD([makeQuery(id+"F21.opExtrude","SWEPT_FACE",FACE,{"disambiguationData":[OSD([subQ28])]})])],"derivedFrom":subQ53}),makeQuery(id+"F21.boolean.opBoolean","SPLIT",EDGE,{"disambiguationData":[TD([makeQuery(id+"F21.opExtrude","SWEPT_FACE",FACE,{"disambiguationData":[OSD([subQ19])]})])],"derivedFrom":subQ53}),makeQuery(id+"F21.boolean.opBoolean","SPLIT",EDGE,{"disambiguationData":[TD([makeQuery(id+"F21.opExtrude","SWEPT_FACE",FACE,{"disambiguationData":[OSD([subQ12])]})])],"derivedFrom":subQ53}),makeQuery(id+"F21.boolean.opBoolean","SPLIT",EDGE,{"disambiguationData":[TD([makeQuery(id+"F21.opExtrude","SWEPT_FACE",FACE,{"disambiguationData":[OSD([subQ8])]})])],"derivedFrom":subQ53}),makeQuery(id+"F21.boolean.opBoolean","SPLIT",EDGE,{"disambiguationData":[TD([makeQuery(id+"F21.opExtrude","SWEPT_FACE",FACE,{"disambiguationData":[OSD([subQ3])]})])],"derivedFrom":subQ53}),makeQuery(id+"F21.boolean.opBoolean","SPLIT",EDGE,{"disambiguationData":[TD([makeQuery(id+"F21.opExtrude","SWEPT_FACE",FACE,{"disambiguationData":[OSD([subQ16])]})])],"derivedFrom":subQ53}),makeQuery(id+"F21.boolean.opBoolean","SPLIT",EDGE,{"disambiguationData":[TD([makeQuery(id+"F21.opExtrude","SWEPT_FACE",FACE,{"disambiguationData":[OSD([subQ25])]})])],"derivedFrom":subQ53}),makeQuery(id+"F21.boolean.opBoolean","SPLIT",EDGE,{"disambiguationData":[TD([makeQuery(id+"F21.opExtrude","SWEPT_FACE",FACE,{"disambiguationData":[OSD([subQ34])]})])],"derivedFrom":subQ53}),makeQuery(id+"F21.boolean.opBoolean","SPLIT",EDGE,{"disambiguationData":[TD([makeQuery(id+"F21.opExtrude","SWEPT_FACE",FACE,{"disambiguationData":[OSD([subQ37])]})])],"derivedFrom":subQ53}),makeQuery(id+"F21.boolean.opBoolean","SPLIT",EDGE,{"disambiguationData":[TD([makeQuery(id+"F21.opExtrude","SWEPT_FACE",FACE,{"disambiguationData":[OSD([subQ40])]})])],"derivedFrom":subQ53}),makeQuery(id+"F21.boolean.opBoolean","SPLIT",EDGE,{"disambiguationData":[TD([makeQuery(id+"F21.opExtrude","SWEPT_FACE",FACE,{"disambiguationData":[OSD([subQ43])]})])],"derivedFrom":subQ53}),makeQuery(id+"F21.boolean.opBoolean","SPLIT",EDGE,{"disambiguationData":[TD([makeQuery(id+"F21.opExtrude","SWEPT_FACE",FACE,{"disambiguationData":[OSD([subQ46])]})])],"derivedFrom":subQ53}),makeQuery(id+"F21.boolean.opBoolean","SPLIT",EDGE,{"disambiguationData":[TD([makeQuery(id+"F21.opExtrude","SWEPT_FACE",FACE,{"disambiguationData":[OSD([subQ31])]})])],"derivedFrom":subQ53}),makeQuery(id+"F21.boolean.opBoolean","SPLIT",EDGE,{"disambiguationData":[TD([makeQuery(id+"F21.opExtrude","SWEPT_FACE",FACE,{"disambiguationData":[OSD([subQ49])]})])],"derivedFrom":subQ53}),makeQuery(id+"F23.opExtrude","SWEPT_EDGE",EDGE,{"disambiguationData":[OSD([subQ1,subQ0,sQuery(id+"F22.wireOp",EDGE,"E83")])]})]});}
            var Q3;
            {var subQ0=sQuery(id+"F0.wireOp",EDGE,"E2.left");var subQ1=sQuery(id+"F0.wireOp",EDGE,"E2.bottom");var subQ3=sQuery(id+"F20.wireOp",EDGE,"E47.5.0.10");var subQ6=sQuery(id+"F20.wireOp",EDGE,"E47.4.0.10");var subQ10=sQuery(id+"F20.wireOp",EDGE,"E47.3.0.10");var subQ14=sQuery(id+"F20.wireOp",EDGE,"E47.1.0.10");var subQ17=sQuery(id+"F20.wireOp",EDGE,"E47.13.0.10");var subQ20=sQuery(id+"F20.wireOp",EDGE,"E47.2.0.10");var subQ22=sQuery(id+"F20.wireOp",EDGE,"E47.14.0.10");var subQ23=sQuery(id+"F20.wireOp",EDGE,"E46.filletArc");var subQ24=sQuery(id+"F20.wireOp",EDGE,"E45.filletArc");var subQ27=sQuery(id+"F20.wireOp",EDGE,"E47.6.0.10");var subQ30=sQuery(id+"F20.wireOp",EDGE,"E47.7.0.10");var subQ33=sQuery(id+"F20.wireOp",EDGE,"E47.8.0.10");var subQ36=sQuery(id+"F20.wireOp",EDGE,"E47.9.0.10");var subQ39=sQuery(id+"F20.wireOp",EDGE,"E47.10.0.10");var subQ42=sQuery(id+"F20.wireOp",EDGE,"E47.11.0.10");var subQ45=sQuery(id+"F20.wireOp",EDGE,"E47.12.0.10");var subQ50=sQuery(id+"F20.wireOp",EDGE,"E47.15.0.10");var subQ52=makeQuery(id+"F1.opExtrude","SWEPT_EDGE",EDGE,{"disambiguationData":[OSD([subQ1,subQ0])]});Q3=makeQuery(id+"F23.boolean.opBoolean","MERGE",EDGE,{"derivedFrom":[makeQuery(id+"F21.boolean.opBoolean","SPLIT",EDGE,{"disambiguationData":[TD([makeQuery(id+"F21.opExtrude","SWEPT_FACE",FACE,{"disambiguationData":[OSD([subQ50])]})])],"derivedFrom":subQ52}),makeQuery(id+"F21.boolean.opBoolean","SPLIT",EDGE,{"disambiguationData":[TD([makeQuery(id+"F21.opExtrude","SWEPT_FACE",FACE,{"disambiguationData":[OSD([subQ24])]})])],"derivedFrom":subQ52}),makeQuery(id+"F21.boolean.opBoolean","SPLIT",EDGE,{"disambiguationData":[TD([makeQuery(id+"F21.opExtrude","SWEPT_FACE",FACE,{"disambiguationData":[OSD([subQ23])]})])],"derivedFrom":subQ52}),makeQuery(id+"F21.boolean.opBoolean","SPLIT",EDGE,{"disambiguationData":[TD([makeQuery(id+"F21.opExtrude","SWEPT_FACE",FACE,{"disambiguationData":[OSD([subQ14])]})])],"derivedFrom":subQ52}),makeQuery(id+"F21.boolean.opBoolean","SPLIT",EDGE,{"disambiguationData":[TD([makeQuery(id+"F21.opExtrude","SWEPT_FACE",FACE,{"disambiguationData":[OSD([subQ20])]})])],"derivedFrom":subQ52}),makeQuery(id+"F21.boolean.opBoolean","SPLIT",EDGE,{"disambiguationData":[TD([makeQuery(id+"F21.opExtrude","SWEPT_FACE",FACE,{"disambiguationData":[OSD([subQ10])]})])],"derivedFrom":subQ52}),makeQuery(id+"F21.boolean.opBoolean","SPLIT",EDGE,{"disambiguationData":[TD([makeQuery(id+"F21.opExtrude","SWEPT_FACE",FACE,{"disambiguationData":[OSD([subQ6])]})])],"derivedFrom":subQ52}),makeQuery(id+"F21.boolean.opBoolean","SPLIT",EDGE,{"disambiguationData":[TD([makeQuery(id+"F21.opExtrude","SWEPT_FACE",FACE,{"disambiguationData":[OSD([subQ3])]})])],"derivedFrom":subQ52}),makeQuery(id+"F21.boolean.opBoolean","SPLIT",EDGE,{"disambiguationData":[TD([makeQuery(id+"F21.opExtrude","SWEPT_FACE",FACE,{"disambiguationData":[OSD([subQ27])]})])],"derivedFrom":subQ52}),makeQuery(id+"F21.boolean.opBoolean","SPLIT",EDGE,{"disambiguationData":[TD([makeQuery(id+"F21.opExtrude","SWEPT_FACE",FACE,{"disambiguationData":[OSD([subQ30])]})])],"derivedFrom":subQ52}),makeQuery(id+"F21.boolean.opBoolean","SPLIT",EDGE,{"disambiguationData":[TD([makeQuery(id+"F21.opExtrude","SWEPT_FACE",FACE,{"disambiguationData":[OSD([subQ33])]})])],"derivedFrom":subQ52}),makeQuery(id+"F21.boolean.opBoolean","SPLIT",EDGE,{"disambiguationData":[TD([makeQuery(id+"F21.opExtrude","SWEPT_FACE",FACE,{"disambiguationData":[OSD([subQ36])]})])],"derivedFrom":subQ52}),makeQuery(id+"F21.boolean.opBoolean","SPLIT",EDGE,{"disambiguationData":[TD([makeQuery(id+"F21.opExtrude","SWEPT_FACE",FACE,{"disambiguationData":[OSD([subQ39])]})])],"derivedFrom":subQ52}),makeQuery(id+"F21.boolean.opBoolean","SPLIT",EDGE,{"disambiguationData":[TD([makeQuery(id+"F21.opExtrude","SWEPT_FACE",FACE,{"disambiguationData":[OSD([subQ42])]})])],"derivedFrom":subQ52}),makeQuery(id+"F21.boolean.opBoolean","SPLIT",EDGE,{"disambiguationData":[TD([makeQuery(id+"F21.opExtrude","SWEPT_FACE",FACE,{"disambiguationData":[OSD([subQ45])]})])],"derivedFrom":subQ52}),makeQuery(id+"F21.boolean.opBoolean","SPLIT",EDGE,{"disambiguationData":[TD([makeQuery(id+"F21.opExtrude","SWEPT_FACE",FACE,{"disambiguationData":[OSD([subQ17])]})])],"derivedFrom":subQ52}),makeQuery(id+"F21.boolean.opBoolean","SPLIT",EDGE,{"disambiguationData":[TD([makeQuery(id+"F21.opExtrude","SWEPT_FACE",FACE,{"disambiguationData":[OSD([subQ22])]})])],"derivedFrom":subQ52}),makeQuery(id+"F23.opExtrude","SWEPT_EDGE",EDGE,{"disambiguationData":[OSD([subQ1,subQ0,sQuery(id+"F22.wireOp",EDGE,"E55")])]})]});}
            var Q4;
            {var subQ0=sQuery(id+"F0.wireOp",EDGE,"E0");var subQ1=makeQuery(id+"F1.opExtrude","SWEPT_FACE",FACE,{"disambiguationData":[OSD([subQ0])]});var subQ2=sQuery(id+"F0.wireOp",EDGE,"E2.left");Q4=makeQuery(id+"F6.boolean.opBoolean","SPLIT",EDGE,{"disambiguationData":[topologyDisambiguationEdgeConnected([subQ1])],"derivedFrom":makeQuery(id+"F5.boolean.opBoolean","SPLIT",EDGE,{"disambiguationData":[topologyDisambiguationEdgeConnected([subQ1])],"derivedFrom":makeQuery(id+"F1.opExtrude","SWEPT_EDGE",EDGE,{"disambiguationData":[OSD([subQ0,subQ2])]})})});}
            var Q5;
            Q5=makeQuery(id+"F17.boolean.opBoolean","COPY",EDGE,{"derivedFrom":makeQuery(id+"F17.opExtrude","SWEPT_EDGE",EDGE,{"disambiguationData":[OSD([sQuery(id+"F16.wireOp",EDGE,"E30"),sQuery(id+"F16.wireOp",EDGE,"E32")])]})});
            var Q6;
            Q6=makeQuery(id+"F19.boolean.opBoolean","COPY",EDGE,{"derivedFrom":makeQuery(id+"F19.opExtrude","SWEPT_EDGE",EDGE,{"disambiguationData":[OSD([sQuery(id+"F18.wireOp",EDGE,"E35"),sQuery(id+"F18.wireOp",EDGE,"E36")])]})});
            var Q7;
            Q7=makeQuery(id+"F17.boolean.opBoolean","COPY",EDGE,{"derivedFrom":makeQuery(id+"F17.opExtrude","SWEPT_EDGE",EDGE,{"disambiguationData":[OSD([sQuery(id+"F4.wireOp",EDGE,"E6"),sQuery(id+"F16.wireOp",EDGE,"E32"),sQuery(id+"F16.wireOp",EDGE,"E33")])]})});
            var Q8;
            Q8=makeQuery(id+"F19.boolean.opBoolean","COPY",EDGE,{"derivedFrom":makeQuery(id+"F19.opExtrude","SWEPT_EDGE",EDGE,{"disambiguationData":[OSD([sQuery(id+"F3.wireOp",EDGE,"E5"),sQuery(id+"F18.wireOp",EDGE,"E34"),sQuery(id+"F18.wireOp",EDGE,"E36")])]})});
            fillet(context, id + "F25", {"entities" : qUnion([Q0, Q1, Q2, Q3, Q4, Q5, Q6, Q7, Q8]), "radius" : 0.5 * mm, "tangentPropagation" : true, "allowEdgeOverflow" : false});
        }
        {
            var Q0;
            Q0=makeQuery(id+"F15.boolean.opBoolean","INTERSECT",EDGE,{"derivedFrom":[makeQuery(id+"F12.opExtrude","SWEPT_FACE",FACE,{"disambiguationData":[OSD([sQuery(id+"F11.wireOp",EDGE,"E22")])]}),makeQuery(id+"F15.opExtrude","SWEPT_FACE",FACE,{"disambiguationData":[OSD([sQuery(id+"F14.wireOp",EDGE,"E25")])]})]});
            var Q1;
            Q1=makeQuery(id+"F15.boolean.opBoolean","INTERSECT",EDGE,{"derivedFrom":[makeQuery(id+"F12.opExtrude","SWEPT_FACE",FACE,{"disambiguationData":[OSD([sQuery(id+"F11.wireOp",EDGE,"E22")])]}),makeQuery(id+"F15.opExtrude","SWEPT_FACE",FACE,{"disambiguationData":[OSD([sQuery(id+"F14.wireOp",EDGE,"E24")])]})]});
            var Q2;
            Q2=makeQuery(id+"F15.boolean.opBoolean","INTERSECT",EDGE,{"derivedFrom":[makeQuery(id+"F12.opExtrude","SWEPT_FACE",FACE,{"disambiguationData":[OSD([sQuery(id+"F11.wireOp",EDGE,"E18")])]}),makeQuery(id+"F15.opExtrude","SWEPT_FACE",FACE,{"disambiguationData":[OSD([sQuery(id+"F14.wireOp",EDGE,"E24")])]})]});
            var Q3;
            Q3=makeQuery(id+"F15.boolean.opBoolean","INTERSECT",EDGE,{"derivedFrom":[makeQuery(id+"F12.opExtrude","SWEPT_FACE",FACE,{"disambiguationData":[OSD([sQuery(id+"F11.wireOp",EDGE,"E18")])]}),makeQuery(id+"F15.opExtrude","SWEPT_FACE",FACE,{"disambiguationData":[OSD([sQuery(id+"F14.wireOp",EDGE,"E25")])]})]});
            var Q4;
            Q4=makeQuery(id+"F15.boolean.opBoolean","INTERSECT",EDGE,{"derivedFrom":[makeQuery(id+"F12.opExtrude","SWEPT_FACE",FACE,{"disambiguationData":[OSD([sQuery(id+"F11.wireOp",EDGE,"E23")])]}),makeQuery(id+"F15.opExtrude","SWEPT_FACE",FACE,{"disambiguationData":[OSD([sQuery(id+"F14.wireOp",EDGE,"E25")])]})]});
            var Q5;
            Q5=makeQuery(id+"F12.opExtrude","SWEPT_EDGE",EDGE,{"disambiguationData":[OSD([sQuery(id+"F11.wireOp",EDGE,"E18"),sQuery(id+"F11.wireOp",EDGE,"E23")])]});
            var Q6;
            Q6=makeQuery(id+"F15.boolean.opBoolean","INTERSECT",EDGE,{"derivedFrom":[makeQuery(id+"F12.opExtrude","SWEPT_FACE",FACE,{"disambiguationData":[OSD([sQuery(id+"F11.wireOp",EDGE,"E23")])]}),makeQuery(id+"F15.opExtrude","SWEPT_FACE",FACE,{"disambiguationData":[OSD([sQuery(id+"F14.wireOp",EDGE,"E24")])]})]});
            var Q7;
            Q7=makeQuery(id+"F12.opExtrude","SWEPT_EDGE",EDGE,{"disambiguationData":[OSD([sQuery(id+"F11.wireOp",EDGE,"E22"),sQuery(id+"F11.wireOp",EDGE,"E23")])]});
            fillet(context, id + "F26", {"entities" : qUnion([Q0, Q1, Q2, Q3, Q4, Q5, Q6, Q7]), "radius" : 1 * mm, "tangentPropagation" : true, "allowEdgeOverflow" : false});
        }
    });
